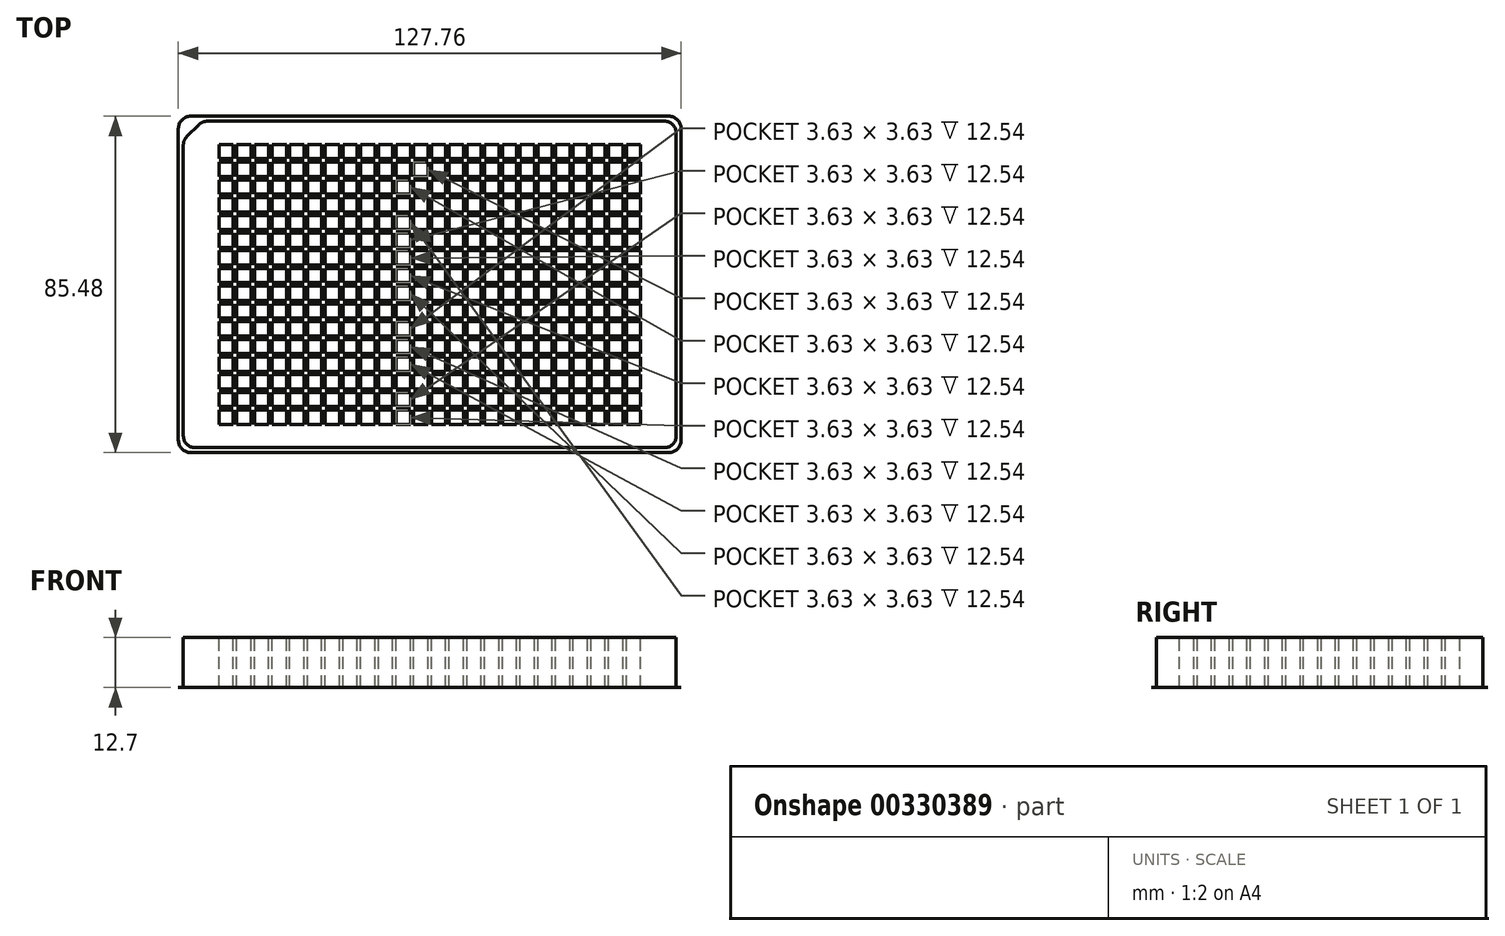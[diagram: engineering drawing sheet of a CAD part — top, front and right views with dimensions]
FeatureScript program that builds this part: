
annotation { "Feature Type Name" : "Feature", "Feature Type Description" : "" }
export const myFeature = defineFeature(function(context is Context, id is Id, definition is map)
    precondition{}
    {
        {
            var Q0;
            Q0=qCreatedBy(makeId("Top.planeOp"),FACE);
            var sketch = newSketch(context, id + "F0", { "sketchPlane" : qUnion([Q0])});
            skLineSegment(sketch, "E0.bottom", {"start": v(-60.7, 42.74) * mm, "end": v(60.7, 42.74) * mm});
            skLineSegment(sketch, "E0.top", {"start": v(-60.7, -42.74) * mm, "end": v(60.7, -42.74) * mm});
            skLineSegment(sketch, "E0.left", {"start": v(-63.88, 39.56) * mm, "end": v(-63.88, -39.56) * mm});
            skLineSegment(sketch, "E0.right", {"start": v(63.88, 39.56) * mm, "end": v(63.88, -39.56) * mm});
            skLineSegment(sketch, "E1", {"start": v(-63.88, 42.74) * mm, "end": v(63.88, -42.74) * mm, "construction": true});
            skPoint(sketch, "E2.visualSharp", {"position": v(-63.88, 42.74) * mm});
            skArc(sketch, "E2.filletArc", {"start": v(-60.7, 42.74) * mm, "mid": v(-62.95, 41.8) * mm, "end": v(-63.88, 39.56) * mm});
            skPoint(sketch, "E3.visualSharp", {"position": v(-63.88, -42.74) * mm});
            skArc(sketch, "E3.filletArc", {"start": v(-63.88, -39.56) * mm, "mid": v(-62.95, -41.8) * mm, "end": v(-60.7, -42.74) * mm});
            skPoint(sketch, "E4.visualSharp", {"position": v(63.88, 42.74) * mm});
            skArc(sketch, "E4.filletArc", {"start": v(63.88, 39.56) * mm, "mid": v(62.95, 41.8) * mm, "end": v(60.7, 42.74) * mm});
            skPoint(sketch, "E5.visualSharp", {"position": v(63.88, -42.74) * mm});
            skArc(sketch, "E5.filletArc", {"start": v(60.7, -42.74) * mm, "mid": v(62.95, -41.8) * mm, "end": v(63.88, -39.56) * mm});
            skSolve(sketch);
        }
        {
            var Q0;
            Q0=makeQuery(id+"F0.imprint","IMPRINT",FACE,{"disambiguationData":[TD([[makeQuery(id+"F0.imprint","IMPRINT",EDGE,{"derivedFrom":sQuery(id+"F0.wireOp",EDGE,"E0.bottom")}),-1.0]])]});
            extrude(context, id + "F1", {"entities" : qUnion([Q0]), "depth" : 3 / 812.8 * mm});
        }
        {
            var Q0;
            Q0=qCreatedBy(makeId("Top.planeOp"),FACE);
            var sketch = newSketch(context, id + "F2", { "sketchPlane" : qUnion([Q0])});
            skLineSegment(sketch, "E6.bottom", {"start": v(59.61, -41.47) * mm, "end": v(-59.6, -41.47) * mm});
            skLineSegment(sketch, "E6.top", {"start": v(59.61, 41.47) * mm, "end": v(-56.54, 41.47) * mm});
            skLineSegment(sketch, "E6.left", {"start": v(62.61, -38.47) * mm, "end": v(62.61, 38.47) * mm});
            skLineSegment(sketch, "E6.right", {"start": v(-62.6, -38.47) * mm, "end": v(-62.61, 35.4) * mm});
            skPoint(sketch, "E7.visualSharp", {"position": v(-62.61, -41.47) * mm});
            skArc(sketch, "E7.filletArc", {"start": v(-62.6, -38.47) * mm, "mid": v(-61.73, -40.6) * mm, "end": v(-59.6, -41.47) * mm});
            skPoint(sketch, "E8.visualSharp", {"position": v(62.6, -41.47) * mm});
            skArc(sketch, "E8.filletArc", {"start": v(59.61, -41.47) * mm, "mid": v(61.73, -40.6) * mm, "end": v(62.61, -38.47) * mm});
            skPoint(sketch, "E9.visualSharp", {"position": v(62.61, 41.47) * mm});
            skArc(sketch, "E9.filletArc", {"start": v(62.61, 38.47) * mm, "mid": v(61.73, 40.6) * mm, "end": v(59.61, 41.47) * mm});
            skLineSegment(sketch, "E10", {"start": v(-61.73, 37.52) * mm, "end": v(-58.66, 40.6) * mm});
            skPoint(sketch, "E11.orphan", {"position": v(-62.61, 41.47) * mm});
            skPoint(sketch, "E12.visualSharp", {"position": v(-62.61, 36.64) * mm});
            skArc(sketch, "E12.filletArc", {"start": v(-61.73, 37.52) * mm, "mid": v(-62.38, 36.55) * mm, "end": v(-62.61, 35.4) * mm});
            skPoint(sketch, "E13.visualSharp", {"position": v(-57.78, 41.47) * mm});
            skArc(sketch, "E13.filletArc", {"start": v(-56.54, 41.47) * mm, "mid": v(-57.69, 41.24) * mm, "end": v(-58.66, 40.6) * mm});
            skSolve(sketch);
        }
        {
            var Q0;
            Q0=qSketchRegion(id+"F2",true);
            extrude(context, id + "F3", {"entities" : qUnion([Q0]), "operationType" : NewBodyOperationType.ADD, "depth" : 12.7 * mm});
        }
        {
            var Q0;
            Q0=makeQuery(id+"F3.opExtrude","CAP_FACE",FACE,{"disambiguationData":[OSD([sQuery(id+"F2.wireOp",EDGE,"E6.bottom"),sQuery(id+"F2.wireOp",EDGE,"E6.top"),sQuery(id+"F2.wireOp",EDGE,"E6.left"),sQuery(id+"F2.wireOp",EDGE,"E6.right"),sQuery(id+"F2.wireOp",EDGE,"E7.filletArc"),sQuery(id+"F2.wireOp",EDGE,"E8.filletArc"),sQuery(id+"F2.wireOp",EDGE,"E9.filletArc"),sQuery(id+"F2.wireOp",EDGE,"E10"),sQuery(id+"F2.wireOp",EDGE,"E12.filletArc"),sQuery(id+"F2.wireOp",EDGE,"E13.filletArc")])],"isStart":false});
            var sketch = newSketch(context, id + "F4", { "sketchPlane" : qUnion([Q0])});
            skLineSegment(sketch, "E14.rect.bottom", {"start": v(-49.94, 31.93) * mm, "end": v(-53.57, 31.93) * mm});
            skLineSegment(sketch, "E14.rect.top", {"start": v(-49.94, 35.56) * mm, "end": v(-53.57, 35.56) * mm});
            skLineSegment(sketch, "E14.rect.left", {"start": v(-49.94, 31.93) * mm, "end": v(-49.94, 35.56) * mm});
            skLineSegment(sketch, "E14.rect.right", {"start": v(-53.57, 31.93) * mm, "end": v(-53.57, 35.56) * mm});
            skPoint(sketch, "E14.rect.middle", {"position": v(-51.75, 33.75) * mm});
            skLineSegment(sketch, "E15.1.0.0", {"start": v(-49.94, 27.43) * mm, "end": v(-49.94, 31.06) * mm});
            skLineSegment(sketch, "E15.1.0.1", {"start": v(-49.94, 27.43) * mm, "end": v(-53.57, 27.43) * mm});
            skLineSegment(sketch, "E15.1.0.2", {"start": v(-53.57, 27.43) * mm, "end": v(-53.57, 31.06) * mm});
            skLineSegment(sketch, "E15.1.0.3", {"start": v(-49.94, 31.06) * mm, "end": v(-53.57, 31.06) * mm});
            skLineSegment(sketch, "E15.2.0.0", {"start": v(-49.94, 22.93) * mm, "end": v(-49.94, 26.56) * mm});
            skLineSegment(sketch, "E15.2.0.1", {"start": v(-49.94, 22.93) * mm, "end": v(-53.57, 22.93) * mm});
            skLineSegment(sketch, "E15.2.0.2", {"start": v(-53.57, 22.93) * mm, "end": v(-53.57, 26.56) * mm});
            skLineSegment(sketch, "E15.2.0.3", {"start": v(-49.94, 26.56) * mm, "end": v(-53.57, 26.56) * mm});
            skLineSegment(sketch, "E15.direction1", {"start": v(-49.94, 31.93) * mm, "end": v(-49.94, 27.43) * mm, "construction": true});
            skLineSegment(sketch, "E16.0.3.0", {"start": v(-49.94, 18.43) * mm, "end": v(-49.94, 22.06) * mm});
            skLineSegment(sketch, "E16.3.3.0", {"start": v(-49.94, 18.43) * mm, "end": v(-53.57, 18.43) * mm});
            skLineSegment(sketch, "E16.6.3.0", {"start": v(-53.57, 18.43) * mm, "end": v(-53.57, 22.06) * mm});
            skLineSegment(sketch, "E16.9.3.0", {"start": v(-49.94, 22.06) * mm, "end": v(-53.57, 22.06) * mm});
            skLineSegment(sketch, "E16.0.4.0", {"start": v(-49.94, 13.93) * mm, "end": v(-49.94, 17.56) * mm});
            skLineSegment(sketch, "E16.3.4.0", {"start": v(-49.94, 13.93) * mm, "end": v(-53.57, 13.93) * mm});
            skLineSegment(sketch, "E16.6.4.0", {"start": v(-53.57, 13.93) * mm, "end": v(-53.57, 17.56) * mm});
            skLineSegment(sketch, "E16.9.4.0", {"start": v(-49.94, 17.56) * mm, "end": v(-53.57, 17.56) * mm});
            skLineSegment(sketch, "E16.0.5.0", {"start": v(-49.94, 9.43) * mm, "end": v(-49.94, 13.06) * mm});
            skLineSegment(sketch, "E16.3.5.0", {"start": v(-49.94, 9.43) * mm, "end": v(-53.57, 9.43) * mm});
            skLineSegment(sketch, "E16.6.5.0", {"start": v(-53.57, 9.43) * mm, "end": v(-53.57, 13.06) * mm});
            skLineSegment(sketch, "E16.9.5.0", {"start": v(-49.94, 13.06) * mm, "end": v(-53.57, 13.06) * mm});
            skLineSegment(sketch, "E16.0.6.0", {"start": v(-49.94, 4.93) * mm, "end": v(-49.94, 8.56) * mm});
            skLineSegment(sketch, "E16.3.6.0", {"start": v(-49.94, 4.93) * mm, "end": v(-53.57, 4.93) * mm});
            skLineSegment(sketch, "E16.6.6.0", {"start": v(-53.57, 4.93) * mm, "end": v(-53.57, 8.56) * mm});
            skLineSegment(sketch, "E16.9.6.0", {"start": v(-49.94, 8.56) * mm, "end": v(-53.57, 8.56) * mm});
            skLineSegment(sketch, "E16.0.7.0", {"start": v(-49.94, 0.43) * mm, "end": v(-49.94, 4.06) * mm});
            skLineSegment(sketch, "E16.3.7.0", {"start": v(-49.94, 0.43) * mm, "end": v(-53.57, 0.43) * mm});
            skLineSegment(sketch, "E16.6.7.0", {"start": v(-53.57, 0.43) * mm, "end": v(-53.57, 4.06) * mm});
            skLineSegment(sketch, "E16.9.7.0", {"start": v(-49.94, 4.06) * mm, "end": v(-53.57, 4.06) * mm});
            skLineSegment(sketch, "E16.0.8.0", {"start": v(-49.94, -4.07) * mm, "end": v(-49.94, -0.44) * mm});
            skLineSegment(sketch, "E16.3.8.0", {"start": v(-49.94, -4.07) * mm, "end": v(-53.57, -4.07) * mm});
            skLineSegment(sketch, "E16.6.8.0", {"start": v(-53.57, -4.07) * mm, "end": v(-53.57, -0.44) * mm});
            skLineSegment(sketch, "E16.9.8.0", {"start": v(-49.94, -0.44) * mm, "end": v(-53.57, -0.44) * mm});
            skLineSegment(sketch, "E16.0.9.0", {"start": v(-49.94, -8.57) * mm, "end": v(-49.94, -4.94) * mm});
            skLineSegment(sketch, "E16.3.9.0", {"start": v(-49.94, -8.57) * mm, "end": v(-53.57, -8.57) * mm});
            skLineSegment(sketch, "E16.6.9.0", {"start": v(-53.57, -8.57) * mm, "end": v(-53.57, -4.94) * mm});
            skLineSegment(sketch, "E16.9.9.0", {"start": v(-49.94, -4.94) * mm, "end": v(-53.57, -4.94) * mm});
            skLineSegment(sketch, "E16.0.10.0", {"start": v(-49.94, -13.07) * mm, "end": v(-49.94, -9.44) * mm});
            skLineSegment(sketch, "E16.3.10.0", {"start": v(-49.94, -13.07) * mm, "end": v(-53.57, -13.07) * mm});
            skLineSegment(sketch, "E16.6.10.0", {"start": v(-53.57, -13.07) * mm, "end": v(-53.57, -9.44) * mm});
            skLineSegment(sketch, "E16.9.10.0", {"start": v(-49.94, -9.44) * mm, "end": v(-53.57, -9.44) * mm});
            skLineSegment(sketch, "E16.0.11.0", {"start": v(-49.94, -17.57) * mm, "end": v(-49.94, -13.94) * mm});
            skLineSegment(sketch, "E16.3.11.0", {"start": v(-49.94, -17.57) * mm, "end": v(-53.57, -17.57) * mm});
            skLineSegment(sketch, "E16.6.11.0", {"start": v(-53.57, -17.57) * mm, "end": v(-53.57, -13.94) * mm});
            skLineSegment(sketch, "E16.9.11.0", {"start": v(-49.94, -13.94) * mm, "end": v(-53.57, -13.94) * mm});
            skLineSegment(sketch, "E16.0.12.0", {"start": v(-49.94, -22.07) * mm, "end": v(-49.94, -18.44) * mm});
            skLineSegment(sketch, "E16.3.12.0", {"start": v(-49.94, -22.07) * mm, "end": v(-53.57, -22.07) * mm});
            skLineSegment(sketch, "E16.6.12.0", {"start": v(-53.57, -22.07) * mm, "end": v(-53.57, -18.44) * mm});
            skLineSegment(sketch, "E16.9.12.0", {"start": v(-49.94, -18.44) * mm, "end": v(-53.57, -18.44) * mm});
            skLineSegment(sketch, "E16.0.13.0", {"start": v(-49.94, -26.57) * mm, "end": v(-49.94, -22.94) * mm});
            skLineSegment(sketch, "E16.3.13.0", {"start": v(-49.94, -26.57) * mm, "end": v(-53.57, -26.57) * mm});
            skLineSegment(sketch, "E16.6.13.0", {"start": v(-53.57, -26.57) * mm, "end": v(-53.57, -22.94) * mm});
            skLineSegment(sketch, "E16.9.13.0", {"start": v(-49.94, -22.94) * mm, "end": v(-53.57, -22.94) * mm});
            skLineSegment(sketch, "E16.0.14.0", {"start": v(-49.94, -31.07) * mm, "end": v(-49.94, -27.44) * mm});
            skLineSegment(sketch, "E16.3.14.0", {"start": v(-49.94, -31.07) * mm, "end": v(-53.57, -31.07) * mm});
            skLineSegment(sketch, "E16.6.14.0", {"start": v(-53.57, -31.07) * mm, "end": v(-53.57, -27.44) * mm});
            skLineSegment(sketch, "E16.9.14.0", {"start": v(-49.94, -27.44) * mm, "end": v(-53.57, -27.44) * mm});
            skLineSegment(sketch, "E16.0.15.0", {"start": v(-49.94, -35.57) * mm, "end": v(-49.94, -31.94) * mm});
            skLineSegment(sketch, "E16.3.15.0", {"start": v(-49.94, -35.57) * mm, "end": v(-53.57, -35.57) * mm});
            skLineSegment(sketch, "E16.6.15.0", {"start": v(-53.57, -35.57) * mm, "end": v(-53.57, -31.94) * mm});
            skLineSegment(sketch, "E16.9.15.0", {"start": v(-49.94, -31.94) * mm, "end": v(-53.57, -31.94) * mm});
            skLineSegment(sketch, "E17.1.0.0", {"start": v(-49.07, 27.43) * mm, "end": v(-49.07, 31.06) * mm});
            skLineSegment(sketch, "E17.1.0.1", {"start": v(-45.44, 27.43) * mm, "end": v(-45.44, 31.06) * mm});
            skLineSegment(sketch, "E17.1.0.2", {"start": v(-45.44, -13.07) * mm, "end": v(-45.44, -9.44) * mm});
            skLineSegment(sketch, "E17.1.0.3", {"start": v(-49.07, 9.43) * mm, "end": v(-49.07, 13.06) * mm});
            skLineSegment(sketch, "E17.1.0.4", {"start": v(-49.07, -13.07) * mm, "end": v(-49.07, -9.44) * mm});
            skLineSegment(sketch, "E17.1.0.5", {"start": v(-49.07, -31.07) * mm, "end": v(-49.07, -27.44) * mm});
            skPoint(sketch, "E17.1.0.6", {"position": v(-47.25, 33.75) * mm});
            skLineSegment(sketch, "E17.1.0.7", {"start": v(-45.44, 9.43) * mm, "end": v(-45.44, 13.06) * mm});
            skLineSegment(sketch, "E17.1.0.8", {"start": v(-45.44, -31.07) * mm, "end": v(-45.44, -27.44) * mm});
            skLineSegment(sketch, "E17.1.0.9", {"start": v(-45.44, 31.93) * mm, "end": v(-45.44, 27.43) * mm, "construction": true});
            skLineSegment(sketch, "E17.1.0.10", {"start": v(-45.44, 31.06) * mm, "end": v(-49.07, 31.06) * mm});
            skLineSegment(sketch, "E17.1.0.11", {"start": v(-45.44, 4.93) * mm, "end": v(-49.07, 4.93) * mm});
            skLineSegment(sketch, "E17.1.0.12", {"start": v(-45.44, -13.07) * mm, "end": v(-49.07, -13.07) * mm});
            skLineSegment(sketch, "E17.1.0.13", {"start": v(-45.44, -31.07) * mm, "end": v(-49.07, -31.07) * mm});
            skLineSegment(sketch, "E17.1.0.14", {"start": v(-49.07, 31.93) * mm, "end": v(-49.07, 35.56) * mm});
            skLineSegment(sketch, "E17.1.0.15", {"start": v(-45.44, 31.93) * mm, "end": v(-45.44, 35.56) * mm});
            skLineSegment(sketch, "E17.1.0.16", {"start": v(-45.44, 31.93) * mm, "end": v(-49.07, 31.93) * mm});
            skLineSegment(sketch, "E17.1.0.17", {"start": v(-49.07, 18.43) * mm, "end": v(-49.07, 22.06) * mm});
            skLineSegment(sketch, "E17.1.0.18", {"start": v(-45.44, 13.06) * mm, "end": v(-49.07, 13.06) * mm});
            skLineSegment(sketch, "E17.1.0.19", {"start": v(-45.44, -4.94) * mm, "end": v(-49.07, -4.94) * mm});
            skLineSegment(sketch, "E17.1.0.20", {"start": v(-45.44, -22.94) * mm, "end": v(-49.07, -22.94) * mm});
            skLineSegment(sketch, "E17.1.0.21", {"start": v(-45.44, -26.57) * mm, "end": v(-45.44, -22.94) * mm});
            skLineSegment(sketch, "E17.1.0.22", {"start": v(-49.07, -8.57) * mm, "end": v(-49.07, -4.94) * mm});
            skLineSegment(sketch, "E17.1.0.23", {"start": v(-49.07, -26.57) * mm, "end": v(-49.07, -22.94) * mm});
            skLineSegment(sketch, "E17.1.0.24", {"start": v(-45.44, 17.56) * mm, "end": v(-49.07, 17.56) * mm});
            skLineSegment(sketch, "E17.1.0.25", {"start": v(-45.44, -0.44) * mm, "end": v(-49.07, -0.44) * mm});
            skLineSegment(sketch, "E17.1.0.26", {"start": v(-45.44, -9.44) * mm, "end": v(-49.07, -9.44) * mm});
            skLineSegment(sketch, "E17.1.0.27", {"start": v(-49.07, -22.07) * mm, "end": v(-49.07, -18.44) * mm});
            skLineSegment(sketch, "E17.1.0.28", {"start": v(-49.07, 13.93) * mm, "end": v(-49.07, 17.56) * mm});
            skLineSegment(sketch, "E17.1.0.29", {"start": v(-49.07, -4.07) * mm, "end": v(-49.07, -0.44) * mm});
            skLineSegment(sketch, "E17.1.0.30", {"start": v(-45.44, 13.93) * mm, "end": v(-49.07, 13.93) * mm});
            skLineSegment(sketch, "E17.1.0.31", {"start": v(-45.44, -4.07) * mm, "end": v(-49.07, -4.07) * mm});
            skLineSegment(sketch, "E17.1.0.32", {"start": v(-45.44, -17.57) * mm, "end": v(-49.07, -17.57) * mm});
            skLineSegment(sketch, "E17.1.0.33", {"start": v(-45.44, -27.44) * mm, "end": v(-49.07, -27.44) * mm});
            skLineSegment(sketch, "E17.1.0.34", {"start": v(-45.44, -35.57) * mm, "end": v(-49.07, -35.57) * mm});
            skLineSegment(sketch, "E17.1.0.35", {"start": v(-45.44, 0.43) * mm, "end": v(-49.07, 0.43) * mm});
            skLineSegment(sketch, "E17.1.0.36", {"start": v(-45.44, 13.93) * mm, "end": v(-45.44, 17.56) * mm});
            skLineSegment(sketch, "E17.1.0.37", {"start": v(-45.44, -22.07) * mm, "end": v(-45.44, -18.44) * mm});
            skLineSegment(sketch, "E17.1.0.38", {"start": v(-45.44, -17.57) * mm, "end": v(-45.44, -13.94) * mm});
            skLineSegment(sketch, "E17.1.0.39", {"start": v(-49.07, 4.93) * mm, "end": v(-49.07, 8.56) * mm});
            skLineSegment(sketch, "E17.1.0.40", {"start": v(-45.44, 26.56) * mm, "end": v(-49.07, 26.56) * mm});
            skLineSegment(sketch, "E17.1.0.41", {"start": v(-45.44, 9.43) * mm, "end": v(-49.07, 9.43) * mm});
            skLineSegment(sketch, "E17.1.0.42", {"start": v(-49.07, 22.93) * mm, "end": v(-49.07, 26.56) * mm});
            skLineSegment(sketch, "E17.1.0.43", {"start": v(-45.44, -13.94) * mm, "end": v(-49.07, -13.94) * mm});
            skLineSegment(sketch, "E17.1.0.44", {"start": v(-45.44, -31.94) * mm, "end": v(-49.07, -31.94) * mm});
            skLineSegment(sketch, "E17.1.0.45", {"start": v(-45.44, 22.06) * mm, "end": v(-49.07, 22.06) * mm});
            skLineSegment(sketch, "E17.1.0.46", {"start": v(-45.44, 4.06) * mm, "end": v(-49.07, 4.06) * mm});
            skLineSegment(sketch, "E17.1.0.47", {"start": v(-49.07, 0.43) * mm, "end": v(-49.07, 4.06) * mm});
            skLineSegment(sketch, "E17.1.0.48", {"start": v(-49.07, -35.57) * mm, "end": v(-49.07, -31.94) * mm});
            skLineSegment(sketch, "E17.1.0.49", {"start": v(-45.44, 0.43) * mm, "end": v(-45.44, 4.06) * mm});
            skLineSegment(sketch, "E17.1.0.50", {"start": v(-45.44, -26.57) * mm, "end": v(-49.07, -26.57) * mm});
            skLineSegment(sketch, "E17.1.0.51", {"start": v(-45.44, -35.57) * mm, "end": v(-45.44, -31.94) * mm});
            skLineSegment(sketch, "E17.1.0.52", {"start": v(-45.44, -4.07) * mm, "end": v(-45.44, -0.44) * mm});
            skLineSegment(sketch, "E17.1.0.53", {"start": v(-45.44, -22.07) * mm, "end": v(-49.07, -22.07) * mm});
            skLineSegment(sketch, "E17.1.0.54", {"start": v(-45.44, 18.43) * mm, "end": v(-45.44, 22.06) * mm});
            skLineSegment(sketch, "E17.1.0.55", {"start": v(-45.44, -18.44) * mm, "end": v(-49.07, -18.44) * mm});
            skLineSegment(sketch, "E17.1.0.56", {"start": v(-45.44, -8.57) * mm, "end": v(-45.44, -4.94) * mm});
            skLineSegment(sketch, "E17.1.0.57", {"start": v(-45.44, 18.43) * mm, "end": v(-49.07, 18.43) * mm});
            skLineSegment(sketch, "E17.1.0.58", {"start": v(-45.44, 35.56) * mm, "end": v(-49.07, 35.56) * mm});
            skLineSegment(sketch, "E17.1.0.59", {"start": v(-45.44, 4.93) * mm, "end": v(-45.44, 8.56) * mm});
            skLineSegment(sketch, "E17.1.0.60", {"start": v(-45.44, 27.43) * mm, "end": v(-49.07, 27.43) * mm});
            skLineSegment(sketch, "E17.1.0.61", {"start": v(-45.44, -8.57) * mm, "end": v(-49.07, -8.57) * mm});
            skLineSegment(sketch, "E17.1.0.62", {"start": v(-45.44, 8.56) * mm, "end": v(-49.07, 8.56) * mm});
            skLineSegment(sketch, "E17.1.0.63", {"start": v(-49.07, -17.57) * mm, "end": v(-49.07, -13.94) * mm});
            skLineSegment(sketch, "E17.1.0.64", {"start": v(-45.44, 22.93) * mm, "end": v(-49.07, 22.93) * mm});
            skLineSegment(sketch, "E17.1.0.65", {"start": v(-45.44, 22.93) * mm, "end": v(-45.44, 26.56) * mm});
            skLineSegment(sketch, "E17.2.0.0", {"start": v(-44.57, 27.43) * mm, "end": v(-44.57, 31.06) * mm});
            skLineSegment(sketch, "E17.2.0.1", {"start": v(-40.94, 27.43) * mm, "end": v(-40.94, 31.06) * mm});
            skLineSegment(sketch, "E17.2.0.2", {"start": v(-40.94, -13.07) * mm, "end": v(-40.94, -9.44) * mm});
            skLineSegment(sketch, "E17.2.0.3", {"start": v(-44.57, 9.43) * mm, "end": v(-44.57, 13.06) * mm});
            skLineSegment(sketch, "E17.2.0.4", {"start": v(-44.56, -13.07) * mm, "end": v(-44.56, -9.44) * mm});
            skLineSegment(sketch, "E17.2.0.5", {"start": v(-44.56, -31.07) * mm, "end": v(-44.56, -27.44) * mm});
            skPoint(sketch, "E17.2.0.6", {"position": v(-42.75, 33.75) * mm});
            skLineSegment(sketch, "E17.2.0.7", {"start": v(-40.94, 9.43) * mm, "end": v(-40.94, 13.06) * mm});
            skLineSegment(sketch, "E17.2.0.8", {"start": v(-40.94, -31.07) * mm, "end": v(-40.94, -27.44) * mm});
            skLineSegment(sketch, "E17.2.0.9", {"start": v(-40.94, 31.93) * mm, "end": v(-40.94, 27.43) * mm, "construction": true});
            skLineSegment(sketch, "E17.2.0.10", {"start": v(-40.94, 31.06) * mm, "end": v(-44.57, 31.06) * mm});
            skLineSegment(sketch, "E17.2.0.11", {"start": v(-40.94, 4.93) * mm, "end": v(-44.57, 4.93) * mm});
            skLineSegment(sketch, "E17.2.0.12", {"start": v(-40.94, -13.07) * mm, "end": v(-44.57, -13.07) * mm});
            skLineSegment(sketch, "E17.2.0.13", {"start": v(-40.94, -31.07) * mm, "end": v(-44.57, -31.07) * mm});
            skLineSegment(sketch, "E17.2.0.14", {"start": v(-44.57, 31.93) * mm, "end": v(-44.57, 35.56) * mm});
            skLineSegment(sketch, "E17.2.0.15", {"start": v(-40.94, 31.93) * mm, "end": v(-40.94, 35.56) * mm});
            skLineSegment(sketch, "E17.2.0.16", {"start": v(-40.94, 31.93) * mm, "end": v(-44.57, 31.93) * mm});
            skLineSegment(sketch, "E17.2.0.17", {"start": v(-44.57, 18.43) * mm, "end": v(-44.57, 22.06) * mm});
            skLineSegment(sketch, "E17.2.0.18", {"start": v(-40.94, 13.06) * mm, "end": v(-44.57, 13.06) * mm});
            skLineSegment(sketch, "E17.2.0.19", {"start": v(-40.94, -4.94) * mm, "end": v(-44.57, -4.94) * mm});
            skLineSegment(sketch, "E17.2.0.20", {"start": v(-40.94, -22.94) * mm, "end": v(-44.57, -22.94) * mm});
            skLineSegment(sketch, "E17.2.0.21", {"start": v(-40.94, -26.57) * mm, "end": v(-40.94, -22.94) * mm});
            skLineSegment(sketch, "E17.2.0.22", {"start": v(-44.56, -8.57) * mm, "end": v(-44.56, -4.94) * mm});
            skLineSegment(sketch, "E17.2.0.23", {"start": v(-44.56, -26.57) * mm, "end": v(-44.56, -22.94) * mm});
            skLineSegment(sketch, "E17.2.0.24", {"start": v(-40.94, 17.56) * mm, "end": v(-44.57, 17.56) * mm});
            skLineSegment(sketch, "E17.2.0.25", {"start": v(-40.94, -0.44) * mm, "end": v(-44.57, -0.44) * mm});
            skLineSegment(sketch, "E17.2.0.26", {"start": v(-40.94, -9.44) * mm, "end": v(-44.57, -9.44) * mm});
            skLineSegment(sketch, "E17.2.0.27", {"start": v(-44.56, -22.07) * mm, "end": v(-44.56, -18.44) * mm});
            skLineSegment(sketch, "E17.2.0.28", {"start": v(-44.57, 13.93) * mm, "end": v(-44.57, 17.56) * mm});
            skLineSegment(sketch, "E17.2.0.29", {"start": v(-44.56, -4.07) * mm, "end": v(-44.56, -0.44) * mm});
            skLineSegment(sketch, "E17.2.0.30", {"start": v(-40.94, 13.93) * mm, "end": v(-44.57, 13.93) * mm});
            skLineSegment(sketch, "E17.2.0.31", {"start": v(-40.94, -4.07) * mm, "end": v(-44.57, -4.07) * mm});
            skLineSegment(sketch, "E17.2.0.32", {"start": v(-40.94, -17.57) * mm, "end": v(-44.57, -17.57) * mm});
            skLineSegment(sketch, "E17.2.0.33", {"start": v(-40.94, -27.44) * mm, "end": v(-44.57, -27.44) * mm});
            skLineSegment(sketch, "E17.2.0.34", {"start": v(-40.94, -35.57) * mm, "end": v(-44.57, -35.57) * mm});
            skLineSegment(sketch, "E17.2.0.35", {"start": v(-40.94, 0.43) * mm, "end": v(-44.57, 0.43) * mm});
            skLineSegment(sketch, "E17.2.0.36", {"start": v(-40.94, 13.93) * mm, "end": v(-40.94, 17.56) * mm});
            skLineSegment(sketch, "E17.2.0.37", {"start": v(-40.94, -22.07) * mm, "end": v(-40.94, -18.44) * mm});
            skLineSegment(sketch, "E17.2.0.38", {"start": v(-40.94, -17.57) * mm, "end": v(-40.94, -13.94) * mm});
            skLineSegment(sketch, "E17.2.0.39", {"start": v(-44.57, 4.93) * mm, "end": v(-44.57, 8.56) * mm});
            skLineSegment(sketch, "E17.2.0.40", {"start": v(-40.94, 26.56) * mm, "end": v(-44.57, 26.56) * mm});
            skLineSegment(sketch, "E17.2.0.41", {"start": v(-40.94, 9.43) * mm, "end": v(-44.57, 9.43) * mm});
            skLineSegment(sketch, "E17.2.0.42", {"start": v(-44.57, 22.93) * mm, "end": v(-44.57, 26.56) * mm});
            skLineSegment(sketch, "E17.2.0.43", {"start": v(-40.94, -13.94) * mm, "end": v(-44.57, -13.94) * mm});
            skLineSegment(sketch, "E17.2.0.44", {"start": v(-40.94, -31.94) * mm, "end": v(-44.57, -31.94) * mm});
            skLineSegment(sketch, "E17.2.0.45", {"start": v(-40.94, 22.06) * mm, "end": v(-44.57, 22.06) * mm});
            skLineSegment(sketch, "E17.2.0.46", {"start": v(-40.94, 4.06) * mm, "end": v(-44.57, 4.06) * mm});
            skLineSegment(sketch, "E17.2.0.47", {"start": v(-44.56, 0.43) * mm, "end": v(-44.56, 4.06) * mm});
            skLineSegment(sketch, "E17.2.0.48", {"start": v(-44.56, -35.57) * mm, "end": v(-44.56, -31.94) * mm});
            skLineSegment(sketch, "E17.2.0.49", {"start": v(-40.94, 0.43) * mm, "end": v(-40.94, 4.06) * mm});
            skLineSegment(sketch, "E17.2.0.50", {"start": v(-40.94, -26.57) * mm, "end": v(-44.57, -26.57) * mm});
            skLineSegment(sketch, "E17.2.0.51", {"start": v(-40.94, -35.57) * mm, "end": v(-40.94, -31.94) * mm});
            skLineSegment(sketch, "E17.2.0.52", {"start": v(-40.94, -4.07) * mm, "end": v(-40.94, -0.44) * mm});
            skLineSegment(sketch, "E17.2.0.53", {"start": v(-40.94, -22.07) * mm, "end": v(-44.57, -22.07) * mm});
            skLineSegment(sketch, "E17.2.0.54", {"start": v(-40.94, 18.43) * mm, "end": v(-40.94, 22.06) * mm});
            skLineSegment(sketch, "E17.2.0.55", {"start": v(-40.94, -18.44) * mm, "end": v(-44.57, -18.44) * mm});
            skLineSegment(sketch, "E17.2.0.56", {"start": v(-40.94, -8.57) * mm, "end": v(-40.94, -4.94) * mm});
            skLineSegment(sketch, "E17.2.0.57", {"start": v(-40.94, 18.43) * mm, "end": v(-44.57, 18.43) * mm});
            skLineSegment(sketch, "E17.2.0.58", {"start": v(-40.94, 35.56) * mm, "end": v(-44.57, 35.56) * mm});
            skLineSegment(sketch, "E17.2.0.59", {"start": v(-40.94, 4.93) * mm, "end": v(-40.94, 8.56) * mm});
            skLineSegment(sketch, "E17.2.0.60", {"start": v(-40.94, 27.43) * mm, "end": v(-44.57, 27.43) * mm});
            skLineSegment(sketch, "E17.2.0.61", {"start": v(-40.94, -8.57) * mm, "end": v(-44.57, -8.57) * mm});
            skLineSegment(sketch, "E17.2.0.62", {"start": v(-40.94, 8.56) * mm, "end": v(-44.57, 8.56) * mm});
            skLineSegment(sketch, "E17.2.0.63", {"start": v(-44.56, -17.57) * mm, "end": v(-44.56, -13.94) * mm});
            skLineSegment(sketch, "E17.2.0.64", {"start": v(-40.94, 22.93) * mm, "end": v(-44.57, 22.93) * mm});
            skLineSegment(sketch, "E17.2.0.65", {"start": v(-40.94, 22.93) * mm, "end": v(-40.94, 26.56) * mm});
            skLineSegment(sketch, "E17.3.0.0", {"start": v(-40.07, 27.43) * mm, "end": v(-40.07, 31.06) * mm});
            skLineSegment(sketch, "E17.3.0.1", {"start": v(-36.43, 27.43) * mm, "end": v(-36.43, 31.06) * mm});
            skLineSegment(sketch, "E17.3.0.2", {"start": v(-36.43, -13.07) * mm, "end": v(-36.43, -9.44) * mm});
            skLineSegment(sketch, "E17.3.0.3", {"start": v(-40.07, 9.43) * mm, "end": v(-40.07, 13.06) * mm});
            skLineSegment(sketch, "E17.3.0.4", {"start": v(-40.06, -13.07) * mm, "end": v(-40.06, -9.44) * mm});
            skLineSegment(sketch, "E17.3.0.5", {"start": v(-40.06, -31.07) * mm, "end": v(-40.06, -27.44) * mm});
            skPoint(sketch, "E17.3.0.6", {"position": v(-38.25, 33.75) * mm});
            skLineSegment(sketch, "E17.3.0.7", {"start": v(-36.44, 9.43) * mm, "end": v(-36.44, 13.06) * mm});
            skLineSegment(sketch, "E17.3.0.8", {"start": v(-36.43, -31.07) * mm, "end": v(-36.43, -27.44) * mm});
            skLineSegment(sketch, "E17.3.0.9", {"start": v(-36.44, 31.93) * mm, "end": v(-36.44, 27.43) * mm, "construction": true});
            skLineSegment(sketch, "E17.3.0.10", {"start": v(-36.44, 31.06) * mm, "end": v(-40.07, 31.06) * mm});
            skLineSegment(sketch, "E17.3.0.11", {"start": v(-36.44, 4.93) * mm, "end": v(-40.07, 4.93) * mm});
            skLineSegment(sketch, "E17.3.0.12", {"start": v(-36.44, -13.07) * mm, "end": v(-40.07, -13.07) * mm});
            skLineSegment(sketch, "E17.3.0.13", {"start": v(-36.44, -31.07) * mm, "end": v(-40.07, -31.07) * mm});
            skLineSegment(sketch, "E17.3.0.14", {"start": v(-40.07, 31.93) * mm, "end": v(-40.07, 35.56) * mm});
            skLineSegment(sketch, "E17.3.0.15", {"start": v(-36.44, 31.93) * mm, "end": v(-36.44, 35.56) * mm});
            skLineSegment(sketch, "E17.3.0.16", {"start": v(-36.44, 31.93) * mm, "end": v(-40.07, 31.93) * mm});
            skLineSegment(sketch, "E17.3.0.17", {"start": v(-40.07, 18.43) * mm, "end": v(-40.07, 22.06) * mm});
            skLineSegment(sketch, "E17.3.0.18", {"start": v(-36.44, 13.06) * mm, "end": v(-40.07, 13.06) * mm});
            skLineSegment(sketch, "E17.3.0.19", {"start": v(-36.44, -4.94) * mm, "end": v(-40.07, -4.94) * mm});
            skLineSegment(sketch, "E17.3.0.20", {"start": v(-36.44, -22.94) * mm, "end": v(-40.07, -22.94) * mm});
            skLineSegment(sketch, "E17.3.0.21", {"start": v(-36.43, -26.57) * mm, "end": v(-36.43, -22.94) * mm});
            skLineSegment(sketch, "E17.3.0.22", {"start": v(-40.06, -8.57) * mm, "end": v(-40.06, -4.94) * mm});
            skLineSegment(sketch, "E17.3.0.23", {"start": v(-40.06, -26.57) * mm, "end": v(-40.06, -22.94) * mm});
            skLineSegment(sketch, "E17.3.0.24", {"start": v(-36.44, 17.56) * mm, "end": v(-40.07, 17.56) * mm});
            skLineSegment(sketch, "E17.3.0.25", {"start": v(-36.44, -0.44) * mm, "end": v(-40.07, -0.44) * mm});
            skLineSegment(sketch, "E17.3.0.26", {"start": v(-36.44, -9.44) * mm, "end": v(-40.07, -9.44) * mm});
            skLineSegment(sketch, "E17.3.0.27", {"start": v(-40.06, -22.07) * mm, "end": v(-40.06, -18.44) * mm});
            skLineSegment(sketch, "E17.3.0.28", {"start": v(-40.07, 13.93) * mm, "end": v(-40.07, 17.56) * mm});
            skLineSegment(sketch, "E17.3.0.29", {"start": v(-40.06, -4.07) * mm, "end": v(-40.06, -0.44) * mm});
            skLineSegment(sketch, "E17.3.0.30", {"start": v(-36.44, 13.93) * mm, "end": v(-40.07, 13.93) * mm});
            skLineSegment(sketch, "E17.3.0.31", {"start": v(-36.44, -4.07) * mm, "end": v(-40.07, -4.07) * mm});
            skLineSegment(sketch, "E17.3.0.32", {"start": v(-36.44, -17.57) * mm, "end": v(-40.07, -17.57) * mm});
            skLineSegment(sketch, "E17.3.0.33", {"start": v(-36.44, -27.44) * mm, "end": v(-40.07, -27.44) * mm});
            skLineSegment(sketch, "E17.3.0.34", {"start": v(-36.44, -35.57) * mm, "end": v(-40.07, -35.57) * mm});
            skLineSegment(sketch, "E17.3.0.35", {"start": v(-36.44, 0.43) * mm, "end": v(-40.07, 0.43) * mm});
            skLineSegment(sketch, "E17.3.0.36", {"start": v(-36.44, 13.93) * mm, "end": v(-36.44, 17.56) * mm});
            skLineSegment(sketch, "E17.3.0.37", {"start": v(-36.43, -22.07) * mm, "end": v(-36.43, -18.44) * mm});
            skLineSegment(sketch, "E17.3.0.38", {"start": v(-36.43, -17.57) * mm, "end": v(-36.43, -13.94) * mm});
            skLineSegment(sketch, "E17.3.0.39", {"start": v(-40.07, 4.93) * mm, "end": v(-40.07, 8.56) * mm});
            skLineSegment(sketch, "E17.3.0.40", {"start": v(-36.44, 26.56) * mm, "end": v(-40.07, 26.56) * mm});
            skLineSegment(sketch, "E17.3.0.41", {"start": v(-36.44, 9.43) * mm, "end": v(-40.07, 9.43) * mm});
            skLineSegment(sketch, "E17.3.0.42", {"start": v(-40.07, 22.93) * mm, "end": v(-40.07, 26.56) * mm});
            skLineSegment(sketch, "E17.3.0.43", {"start": v(-36.44, -13.94) * mm, "end": v(-40.07, -13.94) * mm});
            skLineSegment(sketch, "E17.3.0.44", {"start": v(-36.44, -31.94) * mm, "end": v(-40.07, -31.94) * mm});
            skLineSegment(sketch, "E17.3.0.45", {"start": v(-36.44, 22.06) * mm, "end": v(-40.07, 22.06) * mm});
            skLineSegment(sketch, "E17.3.0.46", {"start": v(-36.44, 4.06) * mm, "end": v(-40.07, 4.06) * mm});
            skLineSegment(sketch, "E17.3.0.47", {"start": v(-40.06, 0.43) * mm, "end": v(-40.06, 4.06) * mm});
            skLineSegment(sketch, "E17.3.0.48", {"start": v(-40.06, -35.57) * mm, "end": v(-40.06, -31.94) * mm});
            skLineSegment(sketch, "E17.3.0.49", {"start": v(-36.43, 0.43) * mm, "end": v(-36.43, 4.06) * mm});
            skLineSegment(sketch, "E17.3.0.50", {"start": v(-36.44, -26.57) * mm, "end": v(-40.07, -26.57) * mm});
            skLineSegment(sketch, "E17.3.0.51", {"start": v(-36.43, -35.57) * mm, "end": v(-36.43, -31.94) * mm});
            skLineSegment(sketch, "E17.3.0.52", {"start": v(-36.43, -4.07) * mm, "end": v(-36.43, -0.44) * mm});
            skLineSegment(sketch, "E17.3.0.53", {"start": v(-36.44, -22.07) * mm, "end": v(-40.07, -22.07) * mm});
            skLineSegment(sketch, "E17.3.0.54", {"start": v(-36.44, 18.43) * mm, "end": v(-36.44, 22.06) * mm});
            skLineSegment(sketch, "E17.3.0.55", {"start": v(-36.44, -18.44) * mm, "end": v(-40.07, -18.44) * mm});
            skLineSegment(sketch, "E17.3.0.56", {"start": v(-36.43, -8.57) * mm, "end": v(-36.43, -4.94) * mm});
            skLineSegment(sketch, "E17.3.0.57", {"start": v(-36.44, 18.43) * mm, "end": v(-40.07, 18.43) * mm});
            skLineSegment(sketch, "E17.3.0.58", {"start": v(-36.44, 35.56) * mm, "end": v(-40.07, 35.56) * mm});
            skLineSegment(sketch, "E17.3.0.59", {"start": v(-36.44, 4.93) * mm, "end": v(-36.44, 8.56) * mm});
            skLineSegment(sketch, "E17.3.0.60", {"start": v(-36.44, 27.43) * mm, "end": v(-40.07, 27.43) * mm});
            skLineSegment(sketch, "E17.3.0.61", {"start": v(-36.44, -8.57) * mm, "end": v(-40.07, -8.57) * mm});
            skLineSegment(sketch, "E17.3.0.62", {"start": v(-36.44, 8.56) * mm, "end": v(-40.07, 8.56) * mm});
            skLineSegment(sketch, "E17.3.0.63", {"start": v(-40.06, -17.57) * mm, "end": v(-40.06, -13.94) * mm});
            skLineSegment(sketch, "E17.3.0.64", {"start": v(-36.44, 22.93) * mm, "end": v(-40.07, 22.93) * mm});
            skLineSegment(sketch, "E17.3.0.65", {"start": v(-36.44, 22.93) * mm, "end": v(-36.44, 26.56) * mm});
            skLineSegment(sketch, "E17.4.0.0", {"start": v(-35.56, 27.43) * mm, "end": v(-35.56, 31.06) * mm});
            skLineSegment(sketch, "E17.4.0.1", {"start": v(-31.93, 27.43) * mm, "end": v(-31.93, 31.06) * mm});
            skLineSegment(sketch, "E17.4.0.2", {"start": v(-31.93, -13.07) * mm, "end": v(-31.93, -9.44) * mm});
            skLineSegment(sketch, "E17.4.0.3", {"start": v(-35.56, 9.43) * mm, "end": v(-35.56, 13.06) * mm});
            skLineSegment(sketch, "E17.4.0.4", {"start": v(-35.56, -13.07) * mm, "end": v(-35.56, -9.44) * mm});
            skLineSegment(sketch, "E17.4.0.5", {"start": v(-35.56, -31.07) * mm, "end": v(-35.56, -27.44) * mm});
            skPoint(sketch, "E17.4.0.6", {"position": v(-33.75, 33.75) * mm});
            skLineSegment(sketch, "E17.4.0.7", {"start": v(-31.93, 9.43) * mm, "end": v(-31.93, 13.06) * mm});
            skLineSegment(sketch, "E17.4.0.8", {"start": v(-31.93, -31.07) * mm, "end": v(-31.93, -27.44) * mm});
            skLineSegment(sketch, "E17.4.0.9", {"start": v(-31.93, 31.93) * mm, "end": v(-31.93, 27.43) * mm, "construction": true});
            skLineSegment(sketch, "E17.4.0.10", {"start": v(-31.93, 31.06) * mm, "end": v(-35.56, 31.06) * mm});
            skLineSegment(sketch, "E17.4.0.11", {"start": v(-31.94, 4.93) * mm, "end": v(-35.57, 4.93) * mm});
            skLineSegment(sketch, "E17.4.0.12", {"start": v(-31.93, -13.07) * mm, "end": v(-35.56, -13.07) * mm});
            skLineSegment(sketch, "E17.4.0.13", {"start": v(-31.93, -31.07) * mm, "end": v(-35.56, -31.07) * mm});
            skLineSegment(sketch, "E17.4.0.14", {"start": v(-35.56, 31.93) * mm, "end": v(-35.56, 35.56) * mm});
            skLineSegment(sketch, "E17.4.0.15", {"start": v(-31.93, 31.93) * mm, "end": v(-31.93, 35.56) * mm});
            skLineSegment(sketch, "E17.4.0.16", {"start": v(-31.94, 31.93) * mm, "end": v(-35.57, 31.93) * mm});
            skLineSegment(sketch, "E17.4.0.17", {"start": v(-35.56, 18.43) * mm, "end": v(-35.56, 22.06) * mm});
            skLineSegment(sketch, "E17.4.0.18", {"start": v(-31.94, 13.06) * mm, "end": v(-35.57, 13.06) * mm});
            skLineSegment(sketch, "E17.4.0.19", {"start": v(-31.93, -4.94) * mm, "end": v(-35.56, -4.94) * mm});
            skLineSegment(sketch, "E17.4.0.20", {"start": v(-31.93, -22.94) * mm, "end": v(-35.56, -22.94) * mm});
            skLineSegment(sketch, "E17.4.0.21", {"start": v(-31.93, -26.57) * mm, "end": v(-31.93, -22.94) * mm});
            skLineSegment(sketch, "E17.4.0.22", {"start": v(-35.56, -8.57) * mm, "end": v(-35.56, -4.94) * mm});
            skLineSegment(sketch, "E17.4.0.23", {"start": v(-35.56, -26.57) * mm, "end": v(-35.56, -22.94) * mm});
            skLineSegment(sketch, "E17.4.0.24", {"start": v(-31.94, 17.56) * mm, "end": v(-35.57, 17.56) * mm});
            skLineSegment(sketch, "E17.4.0.25", {"start": v(-31.93, -0.44) * mm, "end": v(-35.56, -0.44) * mm});
            skLineSegment(sketch, "E17.4.0.26", {"start": v(-31.93, -9.44) * mm, "end": v(-35.56, -9.44) * mm});
            skLineSegment(sketch, "E17.4.0.27", {"start": v(-35.56, -22.07) * mm, "end": v(-35.56, -18.44) * mm});
            skLineSegment(sketch, "E17.4.0.28", {"start": v(-35.56, 13.93) * mm, "end": v(-35.56, 17.56) * mm});
            skLineSegment(sketch, "E17.4.0.29", {"start": v(-35.56, -4.07) * mm, "end": v(-35.56, -0.44) * mm});
            skLineSegment(sketch, "E17.4.0.30", {"start": v(-31.94, 13.93) * mm, "end": v(-35.57, 13.93) * mm});
            skLineSegment(sketch, "E17.4.0.31", {"start": v(-31.93, -4.07) * mm, "end": v(-35.56, -4.07) * mm});
            skLineSegment(sketch, "E17.4.0.32", {"start": v(-31.93, -17.57) * mm, "end": v(-35.56, -17.57) * mm});
            skLineSegment(sketch, "E17.4.0.33", {"start": v(-31.93, -27.44) * mm, "end": v(-35.56, -27.44) * mm});
            skLineSegment(sketch, "E17.4.0.34", {"start": v(-31.93, -35.57) * mm, "end": v(-35.56, -35.57) * mm});
            skLineSegment(sketch, "E17.4.0.35", {"start": v(-31.93, 0.43) * mm, "end": v(-35.56, 0.43) * mm});
            skLineSegment(sketch, "E17.4.0.36", {"start": v(-31.93, 13.93) * mm, "end": v(-31.93, 17.56) * mm});
            skLineSegment(sketch, "E17.4.0.37", {"start": v(-31.93, -22.07) * mm, "end": v(-31.93, -18.44) * mm});
            skLineSegment(sketch, "E17.4.0.38", {"start": v(-31.93, -17.57) * mm, "end": v(-31.93, -13.94) * mm});
            skLineSegment(sketch, "E17.4.0.39", {"start": v(-35.56, 4.93) * mm, "end": v(-35.56, 8.56) * mm});
            skLineSegment(sketch, "E17.4.0.40", {"start": v(-31.93, 26.56) * mm, "end": v(-35.56, 26.56) * mm});
            skLineSegment(sketch, "E17.4.0.41", {"start": v(-31.94, 9.43) * mm, "end": v(-35.57, 9.43) * mm});
            skLineSegment(sketch, "E17.4.0.42", {"start": v(-35.56, 22.93) * mm, "end": v(-35.56, 26.56) * mm});
            skLineSegment(sketch, "E17.4.0.43", {"start": v(-31.93, -13.94) * mm, "end": v(-35.56, -13.94) * mm});
            skLineSegment(sketch, "E17.4.0.44", {"start": v(-31.93, -31.94) * mm, "end": v(-35.56, -31.94) * mm});
            skLineSegment(sketch, "E17.4.0.45", {"start": v(-31.94, 22.06) * mm, "end": v(-35.57, 22.06) * mm});
            skLineSegment(sketch, "E17.4.0.46", {"start": v(-31.93, 4.06) * mm, "end": v(-35.56, 4.06) * mm});
            skLineSegment(sketch, "E17.4.0.47", {"start": v(-35.56, 0.43) * mm, "end": v(-35.56, 4.06) * mm});
            skLineSegment(sketch, "E17.4.0.48", {"start": v(-35.56, -35.57) * mm, "end": v(-35.56, -31.94) * mm});
            skLineSegment(sketch, "E17.4.0.49", {"start": v(-31.93, 0.43) * mm, "end": v(-31.93, 4.06) * mm});
            skLineSegment(sketch, "E17.4.0.50", {"start": v(-31.93, -26.57) * mm, "end": v(-35.56, -26.57) * mm});
            skLineSegment(sketch, "E17.4.0.51", {"start": v(-31.93, -35.57) * mm, "end": v(-31.93, -31.94) * mm});
            skLineSegment(sketch, "E17.4.0.52", {"start": v(-31.93, -4.07) * mm, "end": v(-31.93, -0.44) * mm});
            skLineSegment(sketch, "E17.4.0.53", {"start": v(-31.93, -22.07) * mm, "end": v(-35.56, -22.07) * mm});
            skLineSegment(sketch, "E17.4.0.54", {"start": v(-31.93, 18.43) * mm, "end": v(-31.93, 22.06) * mm});
            skLineSegment(sketch, "E17.4.0.55", {"start": v(-31.93, -18.44) * mm, "end": v(-35.56, -18.44) * mm});
            skLineSegment(sketch, "E17.4.0.56", {"start": v(-31.93, -8.57) * mm, "end": v(-31.93, -4.94) * mm});
            skLineSegment(sketch, "E17.4.0.57", {"start": v(-31.94, 18.43) * mm, "end": v(-35.57, 18.43) * mm});
            skLineSegment(sketch, "E17.4.0.58", {"start": v(-31.94, 35.56) * mm, "end": v(-35.57, 35.56) * mm});
            skLineSegment(sketch, "E17.4.0.59", {"start": v(-31.93, 4.93) * mm, "end": v(-31.93, 8.56) * mm});
            skLineSegment(sketch, "E17.4.0.60", {"start": v(-31.93, 27.43) * mm, "end": v(-35.56, 27.43) * mm});
            skLineSegment(sketch, "E17.4.0.61", {"start": v(-31.93, -8.57) * mm, "end": v(-35.56, -8.57) * mm});
            skLineSegment(sketch, "E17.4.0.62", {"start": v(-31.94, 8.56) * mm, "end": v(-35.57, 8.56) * mm});
            skLineSegment(sketch, "E17.4.0.63", {"start": v(-35.56, -17.57) * mm, "end": v(-35.56, -13.94) * mm});
            skLineSegment(sketch, "E17.4.0.64", {"start": v(-31.93, 22.93) * mm, "end": v(-35.56, 22.93) * mm});
            skLineSegment(sketch, "E17.4.0.65", {"start": v(-31.93, 22.93) * mm, "end": v(-31.93, 26.56) * mm});
            skLineSegment(sketch, "E17.5.0.0", {"start": v(-31.06, 27.43) * mm, "end": v(-31.06, 31.06) * mm});
            skLineSegment(sketch, "E17.5.0.1", {"start": v(-27.43, 27.43) * mm, "end": v(-27.43, 31.06) * mm});
            skLineSegment(sketch, "E17.5.0.2", {"start": v(-27.43, -13.07) * mm, "end": v(-27.43, -9.44) * mm});
            skLineSegment(sketch, "E17.5.0.3", {"start": v(-31.06, 9.43) * mm, "end": v(-31.06, 13.06) * mm});
            skLineSegment(sketch, "E17.5.0.4", {"start": v(-31.06, -13.07) * mm, "end": v(-31.06, -9.44) * mm});
            skLineSegment(sketch, "E17.5.0.5", {"start": v(-31.06, -31.07) * mm, "end": v(-31.06, -27.44) * mm});
            skPoint(sketch, "E17.5.0.6", {"position": v(-29.25, 33.75) * mm});
            skLineSegment(sketch, "E17.5.0.7", {"start": v(-27.43, 9.43) * mm, "end": v(-27.43, 13.06) * mm});
            skLineSegment(sketch, "E17.5.0.8", {"start": v(-27.43, -31.07) * mm, "end": v(-27.43, -27.44) * mm});
            skLineSegment(sketch, "E17.5.0.9", {"start": v(-27.43, 31.93) * mm, "end": v(-27.43, 27.43) * mm, "construction": true});
            skLineSegment(sketch, "E17.5.0.10", {"start": v(-27.43, 31.06) * mm, "end": v(-31.06, 31.06) * mm});
            skLineSegment(sketch, "E17.5.0.11", {"start": v(-27.44, 4.93) * mm, "end": v(-31.07, 4.93) * mm});
            skLineSegment(sketch, "E17.5.0.12", {"start": v(-27.43, -13.07) * mm, "end": v(-31.06, -13.07) * mm});
            skLineSegment(sketch, "E17.5.0.13", {"start": v(-27.43, -31.07) * mm, "end": v(-31.06, -31.07) * mm});
            skLineSegment(sketch, "E17.5.0.14", {"start": v(-31.06, 31.93) * mm, "end": v(-31.06, 35.56) * mm});
            skLineSegment(sketch, "E17.5.0.15", {"start": v(-27.43, 31.93) * mm, "end": v(-27.43, 35.56) * mm});
            skLineSegment(sketch, "E17.5.0.16", {"start": v(-27.44, 31.93) * mm, "end": v(-31.07, 31.93) * mm});
            skLineSegment(sketch, "E17.5.0.17", {"start": v(-31.06, 18.43) * mm, "end": v(-31.06, 22.06) * mm});
            skLineSegment(sketch, "E17.5.0.18", {"start": v(-27.44, 13.06) * mm, "end": v(-31.07, 13.06) * mm});
            skLineSegment(sketch, "E17.5.0.19", {"start": v(-27.43, -4.94) * mm, "end": v(-31.06, -4.94) * mm});
            skLineSegment(sketch, "E17.5.0.20", {"start": v(-27.43, -22.94) * mm, "end": v(-31.06, -22.94) * mm});
            skLineSegment(sketch, "E17.5.0.21", {"start": v(-27.43, -26.57) * mm, "end": v(-27.43, -22.94) * mm});
            skLineSegment(sketch, "E17.5.0.22", {"start": v(-31.06, -8.57) * mm, "end": v(-31.06, -4.94) * mm});
            skLineSegment(sketch, "E17.5.0.23", {"start": v(-31.06, -26.57) * mm, "end": v(-31.06, -22.94) * mm});
            skLineSegment(sketch, "E17.5.0.24", {"start": v(-27.44, 17.56) * mm, "end": v(-31.07, 17.56) * mm});
            skLineSegment(sketch, "E17.5.0.25", {"start": v(-27.43, -0.44) * mm, "end": v(-31.06, -0.44) * mm});
            skLineSegment(sketch, "E17.5.0.26", {"start": v(-27.43, -9.44) * mm, "end": v(-31.06, -9.44) * mm});
            skLineSegment(sketch, "E17.5.0.27", {"start": v(-31.06, -22.07) * mm, "end": v(-31.06, -18.44) * mm});
            skLineSegment(sketch, "E17.5.0.28", {"start": v(-31.06, 13.93) * mm, "end": v(-31.06, 17.56) * mm});
            skLineSegment(sketch, "E17.5.0.29", {"start": v(-31.06, -4.07) * mm, "end": v(-31.06, -0.44) * mm});
            skLineSegment(sketch, "E17.5.0.30", {"start": v(-27.44, 13.93) * mm, "end": v(-31.07, 13.93) * mm});
            skLineSegment(sketch, "E17.5.0.31", {"start": v(-27.43, -4.07) * mm, "end": v(-31.06, -4.07) * mm});
            skLineSegment(sketch, "E17.5.0.32", {"start": v(-27.43, -17.57) * mm, "end": v(-31.06, -17.57) * mm});
            skLineSegment(sketch, "E17.5.0.33", {"start": v(-27.43, -27.44) * mm, "end": v(-31.06, -27.44) * mm});
            skLineSegment(sketch, "E17.5.0.34", {"start": v(-27.43, -35.57) * mm, "end": v(-31.06, -35.57) * mm});
            skLineSegment(sketch, "E17.5.0.35", {"start": v(-27.43, 0.43) * mm, "end": v(-31.06, 0.43) * mm});
            skLineSegment(sketch, "E17.5.0.36", {"start": v(-27.43, 13.93) * mm, "end": v(-27.43, 17.56) * mm});
            skLineSegment(sketch, "E17.5.0.37", {"start": v(-27.43, -22.07) * mm, "end": v(-27.43, -18.44) * mm});
            skLineSegment(sketch, "E17.5.0.38", {"start": v(-27.43, -17.57) * mm, "end": v(-27.43, -13.94) * mm});
            skLineSegment(sketch, "E17.5.0.39", {"start": v(-31.06, 4.93) * mm, "end": v(-31.06, 8.56) * mm});
            skLineSegment(sketch, "E17.5.0.40", {"start": v(-27.43, 26.56) * mm, "end": v(-31.06, 26.56) * mm});
            skLineSegment(sketch, "E17.5.0.41", {"start": v(-27.44, 9.43) * mm, "end": v(-31.07, 9.43) * mm});
            skLineSegment(sketch, "E17.5.0.42", {"start": v(-31.06, 22.93) * mm, "end": v(-31.06, 26.56) * mm});
            skLineSegment(sketch, "E17.5.0.43", {"start": v(-27.43, -13.94) * mm, "end": v(-31.06, -13.94) * mm});
            skLineSegment(sketch, "E17.5.0.44", {"start": v(-27.43, -31.94) * mm, "end": v(-31.06, -31.94) * mm});
            skLineSegment(sketch, "E17.5.0.45", {"start": v(-27.44, 22.06) * mm, "end": v(-31.07, 22.06) * mm});
            skLineSegment(sketch, "E17.5.0.46", {"start": v(-27.43, 4.06) * mm, "end": v(-31.06, 4.06) * mm});
            skLineSegment(sketch, "E17.5.0.47", {"start": v(-31.06, 0.43) * mm, "end": v(-31.06, 4.06) * mm});
            skLineSegment(sketch, "E17.5.0.48", {"start": v(-31.06, -35.57) * mm, "end": v(-31.06, -31.94) * mm});
            skLineSegment(sketch, "E17.5.0.49", {"start": v(-27.43, 0.43) * mm, "end": v(-27.43, 4.06) * mm});
            skLineSegment(sketch, "E17.5.0.50", {"start": v(-27.43, -26.57) * mm, "end": v(-31.06, -26.57) * mm});
            skLineSegment(sketch, "E17.5.0.51", {"start": v(-27.43, -35.57) * mm, "end": v(-27.43, -31.94) * mm});
            skLineSegment(sketch, "E17.5.0.52", {"start": v(-27.43, -4.07) * mm, "end": v(-27.43, -0.44) * mm});
            skLineSegment(sketch, "E17.5.0.53", {"start": v(-27.43, -22.07) * mm, "end": v(-31.06, -22.07) * mm});
            skLineSegment(sketch, "E17.5.0.54", {"start": v(-27.43, 18.43) * mm, "end": v(-27.43, 22.06) * mm});
            skLineSegment(sketch, "E17.5.0.55", {"start": v(-27.43, -18.44) * mm, "end": v(-31.06, -18.44) * mm});
            skLineSegment(sketch, "E17.5.0.56", {"start": v(-27.43, -8.57) * mm, "end": v(-27.43, -4.94) * mm});
            skLineSegment(sketch, "E17.5.0.57", {"start": v(-27.44, 18.43) * mm, "end": v(-31.07, 18.43) * mm});
            skLineSegment(sketch, "E17.5.0.58", {"start": v(-27.44, 35.56) * mm, "end": v(-31.07, 35.56) * mm});
            skLineSegment(sketch, "E17.5.0.59", {"start": v(-27.43, 4.93) * mm, "end": v(-27.43, 8.56) * mm});
            skLineSegment(sketch, "E17.5.0.60", {"start": v(-27.43, 27.43) * mm, "end": v(-31.06, 27.43) * mm});
            skLineSegment(sketch, "E17.5.0.61", {"start": v(-27.43, -8.57) * mm, "end": v(-31.06, -8.57) * mm});
            skLineSegment(sketch, "E17.5.0.62", {"start": v(-27.44, 8.56) * mm, "end": v(-31.07, 8.56) * mm});
            skLineSegment(sketch, "E17.5.0.63", {"start": v(-31.06, -17.57) * mm, "end": v(-31.06, -13.94) * mm});
            skLineSegment(sketch, "E17.5.0.64", {"start": v(-27.43, 22.93) * mm, "end": v(-31.06, 22.93) * mm});
            skLineSegment(sketch, "E17.5.0.65", {"start": v(-27.43, 22.93) * mm, "end": v(-27.43, 26.56) * mm});
            skLineSegment(sketch, "E17.6.0.0", {"start": v(-26.56, 27.43) * mm, "end": v(-26.56, 31.06) * mm});
            skLineSegment(sketch, "E17.6.0.1", {"start": v(-22.93, 27.43) * mm, "end": v(-22.93, 31.06) * mm});
            skLineSegment(sketch, "E17.6.0.2", {"start": v(-22.93, -13.07) * mm, "end": v(-22.93, -9.44) * mm});
            skLineSegment(sketch, "E17.6.0.3", {"start": v(-26.56, 9.43) * mm, "end": v(-26.56, 13.06) * mm});
            skLineSegment(sketch, "E17.6.0.4", {"start": v(-26.56, -13.07) * mm, "end": v(-26.56, -9.44) * mm});
            skLineSegment(sketch, "E17.6.0.5", {"start": v(-26.56, -31.07) * mm, "end": v(-26.56, -27.44) * mm});
            skPoint(sketch, "E17.6.0.6", {"position": v(-24.75, 33.75) * mm});
            skLineSegment(sketch, "E17.6.0.7", {"start": v(-22.93, 9.43) * mm, "end": v(-22.93, 13.06) * mm});
            skLineSegment(sketch, "E17.6.0.8", {"start": v(-22.93, -31.07) * mm, "end": v(-22.93, -27.44) * mm});
            skLineSegment(sketch, "E17.6.0.9", {"start": v(-22.93, 31.93) * mm, "end": v(-22.93, 27.43) * mm, "construction": true});
            skLineSegment(sketch, "E17.6.0.10", {"start": v(-22.93, 31.06) * mm, "end": v(-26.56, 31.06) * mm});
            skLineSegment(sketch, "E17.6.0.11", {"start": v(-22.93, 4.93) * mm, "end": v(-26.56, 4.93) * mm});
            skLineSegment(sketch, "E17.6.0.12", {"start": v(-22.93, -13.07) * mm, "end": v(-26.56, -13.07) * mm});
            skLineSegment(sketch, "E17.6.0.13", {"start": v(-22.93, -31.07) * mm, "end": v(-26.56, -31.07) * mm});
            skLineSegment(sketch, "E17.6.0.14", {"start": v(-26.56, 31.93) * mm, "end": v(-26.56, 35.56) * mm});
            skLineSegment(sketch, "E17.6.0.15", {"start": v(-22.93, 31.93) * mm, "end": v(-22.93, 35.56) * mm});
            skLineSegment(sketch, "E17.6.0.16", {"start": v(-22.93, 31.93) * mm, "end": v(-26.56, 31.93) * mm});
            skLineSegment(sketch, "E17.6.0.17", {"start": v(-26.56, 18.43) * mm, "end": v(-26.56, 22.06) * mm});
            skLineSegment(sketch, "E17.6.0.18", {"start": v(-22.93, 13.06) * mm, "end": v(-26.56, 13.06) * mm});
            skLineSegment(sketch, "E17.6.0.19", {"start": v(-22.93, -4.94) * mm, "end": v(-26.56, -4.94) * mm});
            skLineSegment(sketch, "E17.6.0.20", {"start": v(-22.93, -22.94) * mm, "end": v(-26.56, -22.94) * mm});
            skLineSegment(sketch, "E17.6.0.21", {"start": v(-22.93, -26.57) * mm, "end": v(-22.93, -22.94) * mm});
            skLineSegment(sketch, "E17.6.0.22", {"start": v(-26.56, -8.57) * mm, "end": v(-26.56, -4.94) * mm});
            skLineSegment(sketch, "E17.6.0.23", {"start": v(-26.56, -26.57) * mm, "end": v(-26.56, -22.94) * mm});
            skLineSegment(sketch, "E17.6.0.24", {"start": v(-22.93, 17.56) * mm, "end": v(-26.56, 17.56) * mm});
            skLineSegment(sketch, "E17.6.0.25", {"start": v(-22.93, -0.44) * mm, "end": v(-26.56, -0.44) * mm});
            skLineSegment(sketch, "E17.6.0.26", {"start": v(-22.93, -9.44) * mm, "end": v(-26.56, -9.44) * mm});
            skLineSegment(sketch, "E17.6.0.27", {"start": v(-26.56, -22.07) * mm, "end": v(-26.56, -18.44) * mm});
            skLineSegment(sketch, "E17.6.0.28", {"start": v(-26.56, 13.93) * mm, "end": v(-26.56, 17.56) * mm});
            skLineSegment(sketch, "E17.6.0.29", {"start": v(-26.56, -4.07) * mm, "end": v(-26.56, -0.44) * mm});
            skLineSegment(sketch, "E17.6.0.30", {"start": v(-22.93, 13.93) * mm, "end": v(-26.56, 13.93) * mm});
            skLineSegment(sketch, "E17.6.0.31", {"start": v(-22.93, -4.07) * mm, "end": v(-26.56, -4.07) * mm});
            skLineSegment(sketch, "E17.6.0.32", {"start": v(-22.93, -17.57) * mm, "end": v(-26.56, -17.57) * mm});
            skLineSegment(sketch, "E17.6.0.33", {"start": v(-22.93, -27.44) * mm, "end": v(-26.56, -27.44) * mm});
            skLineSegment(sketch, "E17.6.0.34", {"start": v(-22.93, -35.57) * mm, "end": v(-26.56, -35.57) * mm});
            skLineSegment(sketch, "E17.6.0.35", {"start": v(-22.93, 0.43) * mm, "end": v(-26.56, 0.43) * mm});
            skLineSegment(sketch, "E17.6.0.36", {"start": v(-22.93, 13.93) * mm, "end": v(-22.93, 17.56) * mm});
            skLineSegment(sketch, "E17.6.0.37", {"start": v(-22.93, -22.07) * mm, "end": v(-22.93, -18.44) * mm});
            skLineSegment(sketch, "E17.6.0.38", {"start": v(-22.93, -17.57) * mm, "end": v(-22.93, -13.94) * mm});
            skLineSegment(sketch, "E17.6.0.39", {"start": v(-26.56, 4.93) * mm, "end": v(-26.56, 8.56) * mm});
            skLineSegment(sketch, "E17.6.0.40", {"start": v(-22.93, 26.56) * mm, "end": v(-26.56, 26.56) * mm});
            skLineSegment(sketch, "E17.6.0.41", {"start": v(-22.93, 9.43) * mm, "end": v(-26.56, 9.43) * mm});
            skLineSegment(sketch, "E17.6.0.42", {"start": v(-26.56, 22.93) * mm, "end": v(-26.56, 26.56) * mm});
            skLineSegment(sketch, "E17.6.0.43", {"start": v(-22.93, -13.94) * mm, "end": v(-26.56, -13.94) * mm});
            skLineSegment(sketch, "E17.6.0.44", {"start": v(-22.93, -31.94) * mm, "end": v(-26.56, -31.94) * mm});
            skLineSegment(sketch, "E17.6.0.45", {"start": v(-22.93, 22.06) * mm, "end": v(-26.56, 22.06) * mm});
            skLineSegment(sketch, "E17.6.0.46", {"start": v(-22.93, 4.06) * mm, "end": v(-26.56, 4.06) * mm});
            skLineSegment(sketch, "E17.6.0.47", {"start": v(-26.56, 0.43) * mm, "end": v(-26.56, 4.06) * mm});
            skLineSegment(sketch, "E17.6.0.48", {"start": v(-26.56, -35.57) * mm, "end": v(-26.56, -31.94) * mm});
            skLineSegment(sketch, "E17.6.0.49", {"start": v(-22.93, 0.43) * mm, "end": v(-22.93, 4.06) * mm});
            skLineSegment(sketch, "E17.6.0.50", {"start": v(-22.93, -26.57) * mm, "end": v(-26.56, -26.57) * mm});
            skLineSegment(sketch, "E17.6.0.51", {"start": v(-22.93, -35.57) * mm, "end": v(-22.93, -31.94) * mm});
            skLineSegment(sketch, "E17.6.0.52", {"start": v(-22.93, -4.07) * mm, "end": v(-22.93, -0.44) * mm});
            skLineSegment(sketch, "E17.6.0.53", {"start": v(-22.93, -22.07) * mm, "end": v(-26.56, -22.07) * mm});
            skLineSegment(sketch, "E17.6.0.54", {"start": v(-22.93, 18.43) * mm, "end": v(-22.93, 22.06) * mm});
            skLineSegment(sketch, "E17.6.0.55", {"start": v(-22.93, -18.44) * mm, "end": v(-26.56, -18.44) * mm});
            skLineSegment(sketch, "E17.6.0.56", {"start": v(-22.93, -8.57) * mm, "end": v(-22.93, -4.94) * mm});
            skLineSegment(sketch, "E17.6.0.57", {"start": v(-22.93, 18.43) * mm, "end": v(-26.56, 18.43) * mm});
            skLineSegment(sketch, "E17.6.0.58", {"start": v(-22.93, 35.56) * mm, "end": v(-26.56, 35.56) * mm});
            skLineSegment(sketch, "E17.6.0.59", {"start": v(-22.93, 4.93) * mm, "end": v(-22.93, 8.56) * mm});
            skLineSegment(sketch, "E17.6.0.60", {"start": v(-22.93, 27.43) * mm, "end": v(-26.56, 27.43) * mm});
            skLineSegment(sketch, "E17.6.0.61", {"start": v(-22.93, -8.57) * mm, "end": v(-26.56, -8.57) * mm});
            skLineSegment(sketch, "E17.6.0.62", {"start": v(-22.93, 8.56) * mm, "end": v(-26.56, 8.56) * mm});
            skLineSegment(sketch, "E17.6.0.63", {"start": v(-26.56, -17.57) * mm, "end": v(-26.56, -13.94) * mm});
            skLineSegment(sketch, "E17.6.0.64", {"start": v(-22.93, 22.93) * mm, "end": v(-26.56, 22.93) * mm});
            skLineSegment(sketch, "E17.6.0.65", {"start": v(-22.93, 22.93) * mm, "end": v(-22.93, 26.56) * mm});
            skLineSegment(sketch, "E17.7.0.0", {"start": v(-22.06, 27.43) * mm, "end": v(-22.06, 31.06) * mm});
            skLineSegment(sketch, "E17.7.0.1", {"start": v(-18.43, 27.43) * mm, "end": v(-18.43, 31.06) * mm});
            skLineSegment(sketch, "E17.7.0.2", {"start": v(-18.43, -13.07) * mm, "end": v(-18.43, -9.44) * mm});
            skLineSegment(sketch, "E17.7.0.3", {"start": v(-22.06, 9.43) * mm, "end": v(-22.06, 13.06) * mm});
            skLineSegment(sketch, "E17.7.0.4", {"start": v(-22.06, -13.07) * mm, "end": v(-22.06, -9.44) * mm});
            skLineSegment(sketch, "E17.7.0.5", {"start": v(-22.06, -31.07) * mm, "end": v(-22.06, -27.44) * mm});
            skPoint(sketch, "E17.7.0.6", {"position": v(-20.25, 33.75) * mm});
            skLineSegment(sketch, "E17.7.0.7", {"start": v(-18.43, 9.43) * mm, "end": v(-18.43, 13.06) * mm});
            skLineSegment(sketch, "E17.7.0.8", {"start": v(-18.43, -31.07) * mm, "end": v(-18.43, -27.44) * mm});
            skLineSegment(sketch, "E17.7.0.9", {"start": v(-18.43, 31.93) * mm, "end": v(-18.43, 27.43) * mm, "construction": true});
            skLineSegment(sketch, "E17.7.0.10", {"start": v(-18.43, 31.06) * mm, "end": v(-22.06, 31.06) * mm});
            skLineSegment(sketch, "E17.7.0.11", {"start": v(-18.43, 4.93) * mm, "end": v(-22.06, 4.93) * mm});
            skLineSegment(sketch, "E17.7.0.12", {"start": v(-18.43, -13.07) * mm, "end": v(-22.06, -13.07) * mm});
            skLineSegment(sketch, "E17.7.0.13", {"start": v(-18.43, -31.07) * mm, "end": v(-22.06, -31.07) * mm});
            skLineSegment(sketch, "E17.7.0.14", {"start": v(-22.06, 31.93) * mm, "end": v(-22.06, 35.56) * mm});
            skLineSegment(sketch, "E17.7.0.15", {"start": v(-18.43, 31.93) * mm, "end": v(-18.43, 35.56) * mm});
            skLineSegment(sketch, "E17.7.0.16", {"start": v(-18.43, 31.93) * mm, "end": v(-22.06, 31.93) * mm});
            skLineSegment(sketch, "E17.7.0.17", {"start": v(-22.06, 18.43) * mm, "end": v(-22.06, 22.06) * mm});
            skLineSegment(sketch, "E17.7.0.18", {"start": v(-18.43, 13.06) * mm, "end": v(-22.06, 13.06) * mm});
            skLineSegment(sketch, "E17.7.0.19", {"start": v(-18.43, -4.94) * mm, "end": v(-22.06, -4.94) * mm});
            skLineSegment(sketch, "E17.7.0.20", {"start": v(-18.43, -22.94) * mm, "end": v(-22.06, -22.94) * mm});
            skLineSegment(sketch, "E17.7.0.21", {"start": v(-18.43, -26.57) * mm, "end": v(-18.43, -22.94) * mm});
            skLineSegment(sketch, "E17.7.0.22", {"start": v(-22.06, -8.57) * mm, "end": v(-22.06, -4.94) * mm});
            skLineSegment(sketch, "E17.7.0.23", {"start": v(-22.06, -26.57) * mm, "end": v(-22.06, -22.94) * mm});
            skLineSegment(sketch, "E17.7.0.24", {"start": v(-18.43, 17.56) * mm, "end": v(-22.06, 17.56) * mm});
            skLineSegment(sketch, "E17.7.0.25", {"start": v(-18.43, -0.44) * mm, "end": v(-22.06, -0.44) * mm});
            skLineSegment(sketch, "E17.7.0.26", {"start": v(-18.43, -9.44) * mm, "end": v(-22.06, -9.44) * mm});
            skLineSegment(sketch, "E17.7.0.27", {"start": v(-22.06, -22.07) * mm, "end": v(-22.06, -18.44) * mm});
            skLineSegment(sketch, "E17.7.0.28", {"start": v(-22.06, 13.93) * mm, "end": v(-22.06, 17.56) * mm});
            skLineSegment(sketch, "E17.7.0.29", {"start": v(-22.06, -4.07) * mm, "end": v(-22.06, -0.44) * mm});
            skLineSegment(sketch, "E17.7.0.30", {"start": v(-18.43, 13.93) * mm, "end": v(-22.06, 13.93) * mm});
            skLineSegment(sketch, "E17.7.0.31", {"start": v(-18.43, -4.07) * mm, "end": v(-22.06, -4.07) * mm});
            skLineSegment(sketch, "E17.7.0.32", {"start": v(-18.43, -17.57) * mm, "end": v(-22.06, -17.57) * mm});
            skLineSegment(sketch, "E17.7.0.33", {"start": v(-18.43, -27.44) * mm, "end": v(-22.06, -27.44) * mm});
            skLineSegment(sketch, "E17.7.0.34", {"start": v(-18.43, -35.57) * mm, "end": v(-22.06, -35.57) * mm});
            skLineSegment(sketch, "E17.7.0.35", {"start": v(-18.43, 0.43) * mm, "end": v(-22.06, 0.43) * mm});
            skLineSegment(sketch, "E17.7.0.36", {"start": v(-18.43, 13.93) * mm, "end": v(-18.43, 17.56) * mm});
            skLineSegment(sketch, "E17.7.0.37", {"start": v(-18.43, -22.07) * mm, "end": v(-18.43, -18.44) * mm});
            skLineSegment(sketch, "E17.7.0.38", {"start": v(-18.43, -17.57) * mm, "end": v(-18.43, -13.94) * mm});
            skLineSegment(sketch, "E17.7.0.39", {"start": v(-22.06, 4.93) * mm, "end": v(-22.06, 8.56) * mm});
            skLineSegment(sketch, "E17.7.0.40", {"start": v(-18.43, 26.56) * mm, "end": v(-22.06, 26.56) * mm});
            skLineSegment(sketch, "E17.7.0.41", {"start": v(-18.43, 9.43) * mm, "end": v(-22.06, 9.43) * mm});
            skLineSegment(sketch, "E17.7.0.42", {"start": v(-22.06, 22.93) * mm, "end": v(-22.06, 26.56) * mm});
            skLineSegment(sketch, "E17.7.0.43", {"start": v(-18.43, -13.94) * mm, "end": v(-22.06, -13.94) * mm});
            skLineSegment(sketch, "E17.7.0.44", {"start": v(-18.43, -31.94) * mm, "end": v(-22.06, -31.94) * mm});
            skLineSegment(sketch, "E17.7.0.45", {"start": v(-18.43, 22.06) * mm, "end": v(-22.06, 22.06) * mm});
            skLineSegment(sketch, "E17.7.0.46", {"start": v(-18.43, 4.06) * mm, "end": v(-22.06, 4.06) * mm});
            skLineSegment(sketch, "E17.7.0.47", {"start": v(-22.06, 0.43) * mm, "end": v(-22.06, 4.06) * mm});
            skLineSegment(sketch, "E17.7.0.48", {"start": v(-22.06, -35.57) * mm, "end": v(-22.06, -31.94) * mm});
            skLineSegment(sketch, "E17.7.0.49", {"start": v(-18.43, 0.43) * mm, "end": v(-18.43, 4.06) * mm});
            skLineSegment(sketch, "E17.7.0.50", {"start": v(-18.43, -26.57) * mm, "end": v(-22.06, -26.57) * mm});
            skLineSegment(sketch, "E17.7.0.51", {"start": v(-18.43, -35.57) * mm, "end": v(-18.43, -31.94) * mm});
            skLineSegment(sketch, "E17.7.0.52", {"start": v(-18.43, -4.07) * mm, "end": v(-18.43, -0.44) * mm});
            skLineSegment(sketch, "E17.7.0.53", {"start": v(-18.43, -22.07) * mm, "end": v(-22.06, -22.07) * mm});
            skLineSegment(sketch, "E17.7.0.54", {"start": v(-18.43, 18.43) * mm, "end": v(-18.43, 22.06) * mm});
            skLineSegment(sketch, "E17.7.0.55", {"start": v(-18.43, -18.44) * mm, "end": v(-22.06, -18.44) * mm});
            skLineSegment(sketch, "E17.7.0.56", {"start": v(-18.43, -8.57) * mm, "end": v(-18.43, -4.94) * mm});
            skLineSegment(sketch, "E17.7.0.57", {"start": v(-18.43, 18.43) * mm, "end": v(-22.06, 18.43) * mm});
            skLineSegment(sketch, "E17.7.0.58", {"start": v(-18.43, 35.56) * mm, "end": v(-22.06, 35.56) * mm});
            skLineSegment(sketch, "E17.7.0.59", {"start": v(-18.43, 4.93) * mm, "end": v(-18.43, 8.56) * mm});
            skLineSegment(sketch, "E17.7.0.60", {"start": v(-18.43, 27.43) * mm, "end": v(-22.06, 27.43) * mm});
            skLineSegment(sketch, "E17.7.0.61", {"start": v(-18.43, -8.57) * mm, "end": v(-22.06, -8.57) * mm});
            skLineSegment(sketch, "E17.7.0.62", {"start": v(-18.43, 8.56) * mm, "end": v(-22.06, 8.56) * mm});
            skLineSegment(sketch, "E17.7.0.63", {"start": v(-22.06, -17.57) * mm, "end": v(-22.06, -13.94) * mm});
            skLineSegment(sketch, "E17.7.0.64", {"start": v(-18.43, 22.93) * mm, "end": v(-22.06, 22.93) * mm});
            skLineSegment(sketch, "E17.7.0.65", {"start": v(-18.43, 22.93) * mm, "end": v(-18.43, 26.56) * mm});
            skLineSegment(sketch, "E17.8.0.0", {"start": v(-17.56, 27.43) * mm, "end": v(-17.56, 31.06) * mm});
            skLineSegment(sketch, "E17.8.0.1", {"start": v(-13.93, 27.43) * mm, "end": v(-13.93, 31.06) * mm});
            skLineSegment(sketch, "E17.8.0.2", {"start": v(-13.93, -13.07) * mm, "end": v(-13.93, -9.44) * mm});
            skLineSegment(sketch, "E17.8.0.3", {"start": v(-17.56, 9.43) * mm, "end": v(-17.56, 13.06) * mm});
            skLineSegment(sketch, "E17.8.0.4", {"start": v(-17.56, -13.07) * mm, "end": v(-17.56, -9.44) * mm});
            skLineSegment(sketch, "E17.8.0.5", {"start": v(-17.56, -31.07) * mm, "end": v(-17.56, -27.44) * mm});
            skPoint(sketch, "E17.8.0.6", {"position": v(-15.75, 33.75) * mm});
            skLineSegment(sketch, "E17.8.0.7", {"start": v(-13.93, 9.43) * mm, "end": v(-13.93, 13.06) * mm});
            skLineSegment(sketch, "E17.8.0.8", {"start": v(-13.93, -31.07) * mm, "end": v(-13.93, -27.44) * mm});
            skLineSegment(sketch, "E17.8.0.9", {"start": v(-13.93, 31.93) * mm, "end": v(-13.93, 27.43) * mm, "construction": true});
            skLineSegment(sketch, "E17.8.0.10", {"start": v(-13.93, 31.06) * mm, "end": v(-17.56, 31.06) * mm});
            skLineSegment(sketch, "E17.8.0.11", {"start": v(-13.93, 4.93) * mm, "end": v(-17.56, 4.93) * mm});
            skLineSegment(sketch, "E17.8.0.12", {"start": v(-13.93, -13.07) * mm, "end": v(-17.56, -13.07) * mm});
            skLineSegment(sketch, "E17.8.0.13", {"start": v(-13.93, -31.07) * mm, "end": v(-17.56, -31.07) * mm});
            skLineSegment(sketch, "E17.8.0.14", {"start": v(-17.56, 31.93) * mm, "end": v(-17.56, 35.56) * mm});
            skLineSegment(sketch, "E17.8.0.15", {"start": v(-13.93, 31.93) * mm, "end": v(-13.93, 35.56) * mm});
            skLineSegment(sketch, "E17.8.0.16", {"start": v(-13.93, 31.93) * mm, "end": v(-17.56, 31.93) * mm});
            skLineSegment(sketch, "E17.8.0.17", {"start": v(-17.56, 18.43) * mm, "end": v(-17.56, 22.06) * mm});
            skLineSegment(sketch, "E17.8.0.18", {"start": v(-13.93, 13.06) * mm, "end": v(-17.56, 13.06) * mm});
            skLineSegment(sketch, "E17.8.0.19", {"start": v(-13.93, -4.94) * mm, "end": v(-17.56, -4.94) * mm});
            skLineSegment(sketch, "E17.8.0.20", {"start": v(-13.93, -22.94) * mm, "end": v(-17.56, -22.94) * mm});
            skLineSegment(sketch, "E17.8.0.21", {"start": v(-13.93, -26.57) * mm, "end": v(-13.93, -22.94) * mm});
            skLineSegment(sketch, "E17.8.0.22", {"start": v(-17.56, -8.57) * mm, "end": v(-17.56, -4.94) * mm});
            skLineSegment(sketch, "E17.8.0.23", {"start": v(-17.56, -26.57) * mm, "end": v(-17.56, -22.94) * mm});
            skLineSegment(sketch, "E17.8.0.24", {"start": v(-13.93, 17.56) * mm, "end": v(-17.56, 17.56) * mm});
            skLineSegment(sketch, "E17.8.0.25", {"start": v(-13.93, -0.44) * mm, "end": v(-17.56, -0.44) * mm});
            skLineSegment(sketch, "E17.8.0.26", {"start": v(-13.93, -9.44) * mm, "end": v(-17.56, -9.44) * mm});
            skLineSegment(sketch, "E17.8.0.27", {"start": v(-17.56, -22.07) * mm, "end": v(-17.56, -18.44) * mm});
            skLineSegment(sketch, "E17.8.0.28", {"start": v(-17.56, 13.93) * mm, "end": v(-17.56, 17.56) * mm});
            skLineSegment(sketch, "E17.8.0.29", {"start": v(-17.56, -4.07) * mm, "end": v(-17.56, -0.44) * mm});
            skLineSegment(sketch, "E17.8.0.30", {"start": v(-13.93, 13.93) * mm, "end": v(-17.56, 13.93) * mm});
            skLineSegment(sketch, "E17.8.0.31", {"start": v(-13.93, -4.07) * mm, "end": v(-17.56, -4.07) * mm});
            skLineSegment(sketch, "E17.8.0.32", {"start": v(-13.93, -17.57) * mm, "end": v(-17.56, -17.57) * mm});
            skLineSegment(sketch, "E17.8.0.33", {"start": v(-13.93, -27.44) * mm, "end": v(-17.56, -27.44) * mm});
            skLineSegment(sketch, "E17.8.0.34", {"start": v(-13.93, -35.57) * mm, "end": v(-17.56, -35.57) * mm});
            skLineSegment(sketch, "E17.8.0.35", {"start": v(-13.93, 0.43) * mm, "end": v(-17.56, 0.43) * mm});
            skLineSegment(sketch, "E17.8.0.36", {"start": v(-13.93, 13.93) * mm, "end": v(-13.93, 17.56) * mm});
            skLineSegment(sketch, "E17.8.0.37", {"start": v(-13.93, -22.07) * mm, "end": v(-13.93, -18.44) * mm});
            skLineSegment(sketch, "E17.8.0.38", {"start": v(-13.93, -17.57) * mm, "end": v(-13.93, -13.94) * mm});
            skLineSegment(sketch, "E17.8.0.39", {"start": v(-17.56, 4.93) * mm, "end": v(-17.56, 8.56) * mm});
            skLineSegment(sketch, "E17.8.0.40", {"start": v(-13.93, 26.56) * mm, "end": v(-17.56, 26.56) * mm});
            skLineSegment(sketch, "E17.8.0.41", {"start": v(-13.93, 9.43) * mm, "end": v(-17.56, 9.43) * mm});
            skLineSegment(sketch, "E17.8.0.42", {"start": v(-17.56, 22.93) * mm, "end": v(-17.56, 26.56) * mm});
            skLineSegment(sketch, "E17.8.0.43", {"start": v(-13.93, -13.94) * mm, "end": v(-17.56, -13.94) * mm});
            skLineSegment(sketch, "E17.8.0.44", {"start": v(-13.93, -31.94) * mm, "end": v(-17.56, -31.94) * mm});
            skLineSegment(sketch, "E17.8.0.45", {"start": v(-13.93, 22.06) * mm, "end": v(-17.56, 22.06) * mm});
            skLineSegment(sketch, "E17.8.0.46", {"start": v(-13.93, 4.06) * mm, "end": v(-17.56, 4.06) * mm});
            skLineSegment(sketch, "E17.8.0.47", {"start": v(-17.56, 0.43) * mm, "end": v(-17.56, 4.06) * mm});
            skLineSegment(sketch, "E17.8.0.48", {"start": v(-17.56, -35.57) * mm, "end": v(-17.56, -31.94) * mm});
            skLineSegment(sketch, "E17.8.0.49", {"start": v(-13.93, 0.43) * mm, "end": v(-13.93, 4.06) * mm});
            skLineSegment(sketch, "E17.8.0.50", {"start": v(-13.93, -26.57) * mm, "end": v(-17.56, -26.57) * mm});
            skLineSegment(sketch, "E17.8.0.51", {"start": v(-13.93, -35.57) * mm, "end": v(-13.93, -31.94) * mm});
            skLineSegment(sketch, "E17.8.0.52", {"start": v(-13.93, -4.07) * mm, "end": v(-13.93, -0.44) * mm});
            skLineSegment(sketch, "E17.8.0.53", {"start": v(-13.93, -22.07) * mm, "end": v(-17.56, -22.07) * mm});
            skLineSegment(sketch, "E17.8.0.54", {"start": v(-13.93, 18.43) * mm, "end": v(-13.93, 22.06) * mm});
            skLineSegment(sketch, "E17.8.0.55", {"start": v(-13.93, -18.44) * mm, "end": v(-17.56, -18.44) * mm});
            skLineSegment(sketch, "E17.8.0.56", {"start": v(-13.93, -8.57) * mm, "end": v(-13.93, -4.94) * mm});
            skLineSegment(sketch, "E17.8.0.57", {"start": v(-13.93, 18.43) * mm, "end": v(-17.56, 18.43) * mm});
            skLineSegment(sketch, "E17.8.0.58", {"start": v(-13.93, 35.56) * mm, "end": v(-17.56, 35.56) * mm});
            skLineSegment(sketch, "E17.8.0.59", {"start": v(-13.93, 4.93) * mm, "end": v(-13.93, 8.56) * mm});
            skLineSegment(sketch, "E17.8.0.60", {"start": v(-13.93, 27.43) * mm, "end": v(-17.56, 27.43) * mm});
            skLineSegment(sketch, "E17.8.0.61", {"start": v(-13.93, -8.57) * mm, "end": v(-17.56, -8.57) * mm});
            skLineSegment(sketch, "E17.8.0.62", {"start": v(-13.93, 8.56) * mm, "end": v(-17.56, 8.56) * mm});
            skLineSegment(sketch, "E17.8.0.63", {"start": v(-17.56, -17.57) * mm, "end": v(-17.56, -13.94) * mm});
            skLineSegment(sketch, "E17.8.0.64", {"start": v(-13.93, 22.93) * mm, "end": v(-17.56, 22.93) * mm});
            skLineSegment(sketch, "E17.8.0.65", {"start": v(-13.93, 22.93) * mm, "end": v(-13.93, 26.56) * mm});
            skLineSegment(sketch, "E17.9.0.0", {"start": v(-13.06, 27.43) * mm, "end": v(-13.06, 31.06) * mm});
            skLineSegment(sketch, "E17.9.0.1", {"start": v(-9.43, 27.43) * mm, "end": v(-9.43, 31.06) * mm});
            skLineSegment(sketch, "E17.9.0.2", {"start": v(-9.43, -13.07) * mm, "end": v(-9.43, -9.44) * mm});
            skLineSegment(sketch, "E17.9.0.3", {"start": v(-13.06, 9.43) * mm, "end": v(-13.06, 13.06) * mm});
            skLineSegment(sketch, "E17.9.0.4", {"start": v(-13.06, -13.07) * mm, "end": v(-13.06, -9.44) * mm});
            skLineSegment(sketch, "E17.9.0.5", {"start": v(-13.06, -31.07) * mm, "end": v(-13.06, -27.44) * mm});
            skPoint(sketch, "E17.9.0.6", {"position": v(-11.25, 33.75) * mm});
            skLineSegment(sketch, "E17.9.0.7", {"start": v(-9.43, 9.43) * mm, "end": v(-9.43, 13.06) * mm});
            skLineSegment(sketch, "E17.9.0.8", {"start": v(-9.43, -31.07) * mm, "end": v(-9.43, -27.44) * mm});
            skLineSegment(sketch, "E17.9.0.9", {"start": v(-9.43, 31.93) * mm, "end": v(-9.43, 27.43) * mm, "construction": true});
            skLineSegment(sketch, "E17.9.0.10", {"start": v(-9.43, 31.06) * mm, "end": v(-13.06, 31.06) * mm});
            skLineSegment(sketch, "E17.9.0.11", {"start": v(-9.43, 4.93) * mm, "end": v(-13.06, 4.93) * mm});
            skLineSegment(sketch, "E17.9.0.12", {"start": v(-9.43, -13.07) * mm, "end": v(-13.06, -13.07) * mm});
            skLineSegment(sketch, "E17.9.0.13", {"start": v(-9.43, -31.07) * mm, "end": v(-13.06, -31.07) * mm});
            skLineSegment(sketch, "E17.9.0.14", {"start": v(-13.06, 31.93) * mm, "end": v(-13.06, 35.56) * mm});
            skLineSegment(sketch, "E17.9.0.15", {"start": v(-9.43, 31.93) * mm, "end": v(-9.43, 35.56) * mm});
            skLineSegment(sketch, "E17.9.0.16", {"start": v(-9.43, 31.93) * mm, "end": v(-13.06, 31.93) * mm});
            skLineSegment(sketch, "E17.9.0.17", {"start": v(-13.06, 18.43) * mm, "end": v(-13.06, 22.06) * mm});
            skLineSegment(sketch, "E17.9.0.18", {"start": v(-9.43, 13.06) * mm, "end": v(-13.06, 13.06) * mm});
            skLineSegment(sketch, "E17.9.0.19", {"start": v(-9.43, -4.94) * mm, "end": v(-13.06, -4.94) * mm});
            skLineSegment(sketch, "E17.9.0.20", {"start": v(-9.43, -22.94) * mm, "end": v(-13.06, -22.94) * mm});
            skLineSegment(sketch, "E17.9.0.21", {"start": v(-9.43, -26.57) * mm, "end": v(-9.43, -22.94) * mm});
            skLineSegment(sketch, "E17.9.0.22", {"start": v(-13.06, -8.57) * mm, "end": v(-13.06, -4.94) * mm});
            skLineSegment(sketch, "E17.9.0.23", {"start": v(-13.06, -26.57) * mm, "end": v(-13.06, -22.94) * mm});
            skLineSegment(sketch, "E17.9.0.24", {"start": v(-9.43, 17.56) * mm, "end": v(-13.06, 17.56) * mm});
            skLineSegment(sketch, "E17.9.0.25", {"start": v(-9.43, -0.44) * mm, "end": v(-13.06, -0.44) * mm});
            skLineSegment(sketch, "E17.9.0.26", {"start": v(-9.43, -9.44) * mm, "end": v(-13.06, -9.44) * mm});
            skLineSegment(sketch, "E17.9.0.27", {"start": v(-13.06, -22.07) * mm, "end": v(-13.06, -18.44) * mm});
            skLineSegment(sketch, "E17.9.0.28", {"start": v(-13.06, 13.93) * mm, "end": v(-13.06, 17.56) * mm});
            skLineSegment(sketch, "E17.9.0.29", {"start": v(-13.06, -4.07) * mm, "end": v(-13.06, -0.44) * mm});
            skLineSegment(sketch, "E17.9.0.30", {"start": v(-9.43, 13.93) * mm, "end": v(-13.06, 13.93) * mm});
            skLineSegment(sketch, "E17.9.0.31", {"start": v(-9.43, -4.07) * mm, "end": v(-13.06, -4.07) * mm});
            skLineSegment(sketch, "E17.9.0.32", {"start": v(-9.43, -17.57) * mm, "end": v(-13.06, -17.57) * mm});
            skLineSegment(sketch, "E17.9.0.33", {"start": v(-9.43, -27.44) * mm, "end": v(-13.06, -27.44) * mm});
            skLineSegment(sketch, "E17.9.0.34", {"start": v(-9.43, -35.57) * mm, "end": v(-13.06, -35.57) * mm});
            skLineSegment(sketch, "E17.9.0.35", {"start": v(-9.43, 0.43) * mm, "end": v(-13.06, 0.43) * mm});
            skLineSegment(sketch, "E17.9.0.36", {"start": v(-9.43, 13.93) * mm, "end": v(-9.43, 17.56) * mm});
            skLineSegment(sketch, "E17.9.0.37", {"start": v(-9.43, -22.07) * mm, "end": v(-9.43, -18.44) * mm});
            skLineSegment(sketch, "E17.9.0.38", {"start": v(-9.43, -17.57) * mm, "end": v(-9.43, -13.94) * mm});
            skLineSegment(sketch, "E17.9.0.39", {"start": v(-13.06, 4.93) * mm, "end": v(-13.06, 8.56) * mm});
            skLineSegment(sketch, "E17.9.0.40", {"start": v(-9.43, 26.56) * mm, "end": v(-13.06, 26.56) * mm});
            skLineSegment(sketch, "E17.9.0.41", {"start": v(-9.43, 9.43) * mm, "end": v(-13.06, 9.43) * mm});
            skLineSegment(sketch, "E17.9.0.42", {"start": v(-13.06, 22.93) * mm, "end": v(-13.06, 26.56) * mm});
            skLineSegment(sketch, "E17.9.0.43", {"start": v(-9.43, -13.94) * mm, "end": v(-13.06, -13.94) * mm});
            skLineSegment(sketch, "E17.9.0.44", {"start": v(-9.43, -31.94) * mm, "end": v(-13.06, -31.94) * mm});
            skLineSegment(sketch, "E17.9.0.45", {"start": v(-9.43, 22.06) * mm, "end": v(-13.06, 22.06) * mm});
            skLineSegment(sketch, "E17.9.0.46", {"start": v(-9.43, 4.06) * mm, "end": v(-13.06, 4.06) * mm});
            skLineSegment(sketch, "E17.9.0.47", {"start": v(-13.06, 0.43) * mm, "end": v(-13.06, 4.06) * mm});
            skLineSegment(sketch, "E17.9.0.48", {"start": v(-13.06, -35.57) * mm, "end": v(-13.06, -31.94) * mm});
            skLineSegment(sketch, "E17.9.0.49", {"start": v(-9.43, 0.43) * mm, "end": v(-9.43, 4.06) * mm});
            skLineSegment(sketch, "E17.9.0.50", {"start": v(-9.43, -26.57) * mm, "end": v(-13.06, -26.57) * mm});
            skLineSegment(sketch, "E17.9.0.51", {"start": v(-9.43, -35.57) * mm, "end": v(-9.43, -31.94) * mm});
            skLineSegment(sketch, "E17.9.0.52", {"start": v(-9.43, -4.07) * mm, "end": v(-9.43, -0.44) * mm});
            skLineSegment(sketch, "E17.9.0.53", {"start": v(-9.43, -22.07) * mm, "end": v(-13.06, -22.07) * mm});
            skLineSegment(sketch, "E17.9.0.54", {"start": v(-9.43, 18.43) * mm, "end": v(-9.43, 22.06) * mm});
            skLineSegment(sketch, "E17.9.0.55", {"start": v(-9.43, -18.44) * mm, "end": v(-13.06, -18.44) * mm});
            skLineSegment(sketch, "E17.9.0.56", {"start": v(-9.43, -8.57) * mm, "end": v(-9.43, -4.94) * mm});
            skLineSegment(sketch, "E17.9.0.57", {"start": v(-9.43, 18.43) * mm, "end": v(-13.06, 18.43) * mm});
            skLineSegment(sketch, "E17.9.0.58", {"start": v(-9.43, 35.56) * mm, "end": v(-13.06, 35.56) * mm});
            skLineSegment(sketch, "E17.9.0.59", {"start": v(-9.43, 4.93) * mm, "end": v(-9.43, 8.56) * mm});
            skLineSegment(sketch, "E17.9.0.60", {"start": v(-9.43, 27.43) * mm, "end": v(-13.06, 27.43) * mm});
            skLineSegment(sketch, "E17.9.0.61", {"start": v(-9.43, -8.57) * mm, "end": v(-13.06, -8.57) * mm});
            skLineSegment(sketch, "E17.9.0.62", {"start": v(-9.43, 8.56) * mm, "end": v(-13.06, 8.56) * mm});
            skLineSegment(sketch, "E17.9.0.63", {"start": v(-13.06, -17.57) * mm, "end": v(-13.06, -13.94) * mm});
            skLineSegment(sketch, "E17.9.0.64", {"start": v(-9.43, 22.93) * mm, "end": v(-13.06, 22.93) * mm});
            skLineSegment(sketch, "E17.9.0.65", {"start": v(-9.43, 22.93) * mm, "end": v(-9.43, 26.56) * mm});
            skLineSegment(sketch, "E17.10.0.0", {"start": v(-8.56, 27.43) * mm, "end": v(-8.56, 31.06) * mm});
            skLineSegment(sketch, "E17.10.0.1", {"start": v(-4.93, 27.43) * mm, "end": v(-4.93, 31.06) * mm});
            skLineSegment(sketch, "E17.10.0.2", {"start": v(-4.93, -13.07) * mm, "end": v(-4.93, -9.44) * mm});
            skLineSegment(sketch, "E17.10.0.3", {"start": v(-8.56, 9.43) * mm, "end": v(-8.56, 13.06) * mm});
            skLineSegment(sketch, "E17.10.0.4", {"start": v(-8.56, -13.07) * mm, "end": v(-8.56, -9.44) * mm});
            skLineSegment(sketch, "E17.10.0.5", {"start": v(-8.56, -31.07) * mm, "end": v(-8.56, -27.44) * mm});
            skPoint(sketch, "E17.10.0.6", {"position": v(-6.75, 33.75) * mm});
            skLineSegment(sketch, "E17.10.0.7", {"start": v(-4.93, 9.43) * mm, "end": v(-4.93, 13.06) * mm});
            skLineSegment(sketch, "E17.10.0.8", {"start": v(-4.93, -31.07) * mm, "end": v(-4.93, -27.44) * mm});
            skLineSegment(sketch, "E17.10.0.9", {"start": v(-4.93, 31.93) * mm, "end": v(-4.93, 27.43) * mm, "construction": true});
            skLineSegment(sketch, "E17.10.0.10", {"start": v(-4.93, 31.06) * mm, "end": v(-8.56, 31.06) * mm});
            skLineSegment(sketch, "E17.10.0.11", {"start": v(-4.93, 4.93) * mm, "end": v(-8.56, 4.93) * mm});
            skLineSegment(sketch, "E17.10.0.12", {"start": v(-4.93, -13.07) * mm, "end": v(-8.56, -13.07) * mm});
            skLineSegment(sketch, "E17.10.0.13", {"start": v(-4.93, -31.07) * mm, "end": v(-8.56, -31.07) * mm});
            skLineSegment(sketch, "E17.10.0.14", {"start": v(-8.56, 31.93) * mm, "end": v(-8.56, 35.56) * mm});
            skLineSegment(sketch, "E17.10.0.15", {"start": v(-4.93, 31.93) * mm, "end": v(-4.93, 35.56) * mm});
            skLineSegment(sketch, "E17.10.0.16", {"start": v(-4.93, 31.93) * mm, "end": v(-8.56, 31.93) * mm});
            skLineSegment(sketch, "E17.10.0.17", {"start": v(-8.56, 18.43) * mm, "end": v(-8.56, 22.06) * mm});
            skLineSegment(sketch, "E17.10.0.18", {"start": v(-4.93, 13.06) * mm, "end": v(-8.56, 13.06) * mm});
            skLineSegment(sketch, "E17.10.0.19", {"start": v(-4.93, -4.94) * mm, "end": v(-8.56, -4.94) * mm});
            skLineSegment(sketch, "E17.10.0.20", {"start": v(-4.93, -22.94) * mm, "end": v(-8.56, -22.94) * mm});
            skLineSegment(sketch, "E17.10.0.21", {"start": v(-4.93, -26.57) * mm, "end": v(-4.93, -22.94) * mm});
            skLineSegment(sketch, "E17.10.0.22", {"start": v(-8.56, -8.57) * mm, "end": v(-8.56, -4.94) * mm});
            skLineSegment(sketch, "E17.10.0.23", {"start": v(-8.56, -26.57) * mm, "end": v(-8.56, -22.94) * mm});
            skLineSegment(sketch, "E17.10.0.24", {"start": v(-4.93, 17.56) * mm, "end": v(-8.56, 17.56) * mm});
            skLineSegment(sketch, "E17.10.0.25", {"start": v(-4.93, -0.44) * mm, "end": v(-8.56, -0.44) * mm});
            skLineSegment(sketch, "E17.10.0.26", {"start": v(-4.93, -9.44) * mm, "end": v(-8.56, -9.44) * mm});
            skLineSegment(sketch, "E17.10.0.27", {"start": v(-8.56, -22.07) * mm, "end": v(-8.56, -18.44) * mm});
            skLineSegment(sketch, "E17.10.0.28", {"start": v(-8.56, 13.93) * mm, "end": v(-8.56, 17.56) * mm});
            skLineSegment(sketch, "E17.10.0.29", {"start": v(-8.56, -4.07) * mm, "end": v(-8.56, -0.44) * mm});
            skLineSegment(sketch, "E17.10.0.30", {"start": v(-4.93, 13.93) * mm, "end": v(-8.56, 13.93) * mm});
            skLineSegment(sketch, "E17.10.0.31", {"start": v(-4.93, -4.07) * mm, "end": v(-8.56, -4.07) * mm});
            skLineSegment(sketch, "E17.10.0.32", {"start": v(-4.93, -17.57) * mm, "end": v(-8.56, -17.57) * mm});
            skLineSegment(sketch, "E17.10.0.33", {"start": v(-4.93, -27.44) * mm, "end": v(-8.56, -27.44) * mm});
            skLineSegment(sketch, "E17.10.0.34", {"start": v(-4.93, -35.57) * mm, "end": v(-8.56, -35.57) * mm});
            skLineSegment(sketch, "E17.10.0.35", {"start": v(-4.93, 0.43) * mm, "end": v(-8.56, 0.43) * mm});
            skLineSegment(sketch, "E17.10.0.36", {"start": v(-4.93, 13.93) * mm, "end": v(-4.93, 17.56) * mm});
            skLineSegment(sketch, "E17.10.0.37", {"start": v(-4.93, -22.07) * mm, "end": v(-4.93, -18.44) * mm});
            skLineSegment(sketch, "E17.10.0.38", {"start": v(-4.93, -17.57) * mm, "end": v(-4.93, -13.94) * mm});
            skLineSegment(sketch, "E17.10.0.39", {"start": v(-8.56, 4.93) * mm, "end": v(-8.56, 8.56) * mm});
            skLineSegment(sketch, "E17.10.0.40", {"start": v(-4.93, 26.56) * mm, "end": v(-8.56, 26.56) * mm});
            skLineSegment(sketch, "E17.10.0.41", {"start": v(-4.93, 9.43) * mm, "end": v(-8.56, 9.43) * mm});
            skLineSegment(sketch, "E17.10.0.42", {"start": v(-8.56, 22.93) * mm, "end": v(-8.56, 26.56) * mm});
            skLineSegment(sketch, "E17.10.0.43", {"start": v(-4.93, -13.94) * mm, "end": v(-8.56, -13.94) * mm});
            skLineSegment(sketch, "E17.10.0.44", {"start": v(-4.93, -31.94) * mm, "end": v(-8.56, -31.94) * mm});
            skLineSegment(sketch, "E17.10.0.45", {"start": v(-4.93, 22.06) * mm, "end": v(-8.56, 22.06) * mm});
            skLineSegment(sketch, "E17.10.0.46", {"start": v(-4.93, 4.06) * mm, "end": v(-8.56, 4.06) * mm});
            skLineSegment(sketch, "E17.10.0.47", {"start": v(-8.56, 0.43) * mm, "end": v(-8.56, 4.06) * mm});
            skLineSegment(sketch, "E17.10.0.48", {"start": v(-8.56, -35.57) * mm, "end": v(-8.56, -31.94) * mm});
            skLineSegment(sketch, "E17.10.0.49", {"start": v(-4.93, 0.43) * mm, "end": v(-4.93, 4.06) * mm});
            skLineSegment(sketch, "E17.10.0.50", {"start": v(-4.93, -26.57) * mm, "end": v(-8.56, -26.57) * mm});
            skLineSegment(sketch, "E17.10.0.51", {"start": v(-4.93, -35.57) * mm, "end": v(-4.93, -31.94) * mm});
            skLineSegment(sketch, "E17.10.0.52", {"start": v(-4.93, -4.07) * mm, "end": v(-4.93, -0.44) * mm});
            skLineSegment(sketch, "E17.10.0.53", {"start": v(-4.93, -22.07) * mm, "end": v(-8.56, -22.07) * mm});
            skLineSegment(sketch, "E17.10.0.54", {"start": v(-4.93, 18.43) * mm, "end": v(-4.93, 22.06) * mm});
            skLineSegment(sketch, "E17.10.0.55", {"start": v(-4.93, -18.44) * mm, "end": v(-8.56, -18.44) * mm});
            skLineSegment(sketch, "E17.10.0.56", {"start": v(-4.93, -8.57) * mm, "end": v(-4.93, -4.94) * mm});
            skLineSegment(sketch, "E17.10.0.57", {"start": v(-4.93, 18.43) * mm, "end": v(-8.56, 18.43) * mm});
            skLineSegment(sketch, "E17.10.0.58", {"start": v(-4.93, 35.56) * mm, "end": v(-8.56, 35.56) * mm});
            skLineSegment(sketch, "E17.10.0.59", {"start": v(-4.93, 4.93) * mm, "end": v(-4.93, 8.56) * mm});
            skLineSegment(sketch, "E17.10.0.60", {"start": v(-4.93, 27.43) * mm, "end": v(-8.56, 27.43) * mm});
            skLineSegment(sketch, "E17.10.0.61", {"start": v(-4.93, -8.57) * mm, "end": v(-8.56, -8.57) * mm});
            skLineSegment(sketch, "E17.10.0.62", {"start": v(-4.93, 8.56) * mm, "end": v(-8.56, 8.56) * mm});
            skLineSegment(sketch, "E17.10.0.63", {"start": v(-8.56, -17.57) * mm, "end": v(-8.56, -13.94) * mm});
            skLineSegment(sketch, "E17.10.0.64", {"start": v(-4.93, 22.93) * mm, "end": v(-8.56, 22.93) * mm});
            skLineSegment(sketch, "E17.10.0.65", {"start": v(-4.93, 22.93) * mm, "end": v(-4.93, 26.56) * mm});
            skLineSegment(sketch, "E17.11.0.0", {"start": v(-4.06, 27.43) * mm, "end": v(-4.06, 31.06) * mm});
            skLineSegment(sketch, "E17.11.0.1", {"start": v(-0.43, 27.43) * mm, "end": v(-0.43, 31.06) * mm});
            skLineSegment(sketch, "E17.11.0.2", {"start": v(-0.43, -13.07) * mm, "end": v(-0.43, -9.44) * mm});
            skLineSegment(sketch, "E17.11.0.3", {"start": v(-4.06, 9.43) * mm, "end": v(-4.06, 13.06) * mm});
            skLineSegment(sketch, "E17.11.0.4", {"start": v(-4.06, -13.07) * mm, "end": v(-4.06, -9.44) * mm});
            skLineSegment(sketch, "E17.11.0.5", {"start": v(-4.06, -31.07) * mm, "end": v(-4.06, -27.44) * mm});
            skPoint(sketch, "E17.11.0.6", {"position": v(-2.25, 33.75) * mm});
            skLineSegment(sketch, "E17.11.0.7", {"start": v(-0.43, 9.43) * mm, "end": v(-0.43, 13.06) * mm});
            skLineSegment(sketch, "E17.11.0.8", {"start": v(-0.43, -31.07) * mm, "end": v(-0.43, -27.44) * mm});
            skLineSegment(sketch, "E17.11.0.9", {"start": v(-0.43, 31.93) * mm, "end": v(-0.43, 27.43) * mm, "construction": true});
            skLineSegment(sketch, "E17.11.0.10", {"start": v(-0.43, 31.06) * mm, "end": v(-4.06, 31.06) * mm});
            skLineSegment(sketch, "E17.11.0.11", {"start": v(-0.43, 4.93) * mm, "end": v(-4.06, 4.93) * mm});
            skLineSegment(sketch, "E17.11.0.12", {"start": v(-0.43, -13.07) * mm, "end": v(-4.06, -13.07) * mm});
            skLineSegment(sketch, "E17.11.0.13", {"start": v(-0.43, -31.07) * mm, "end": v(-4.06, -31.07) * mm});
            skLineSegment(sketch, "E17.11.0.14", {"start": v(-4.06, 31.93) * mm, "end": v(-4.06, 35.56) * mm});
            skLineSegment(sketch, "E17.11.0.15", {"start": v(-0.43, 31.93) * mm, "end": v(-0.43, 35.56) * mm});
            skLineSegment(sketch, "E17.11.0.16", {"start": v(-0.43, 31.93) * mm, "end": v(-4.06, 31.93) * mm});
            skLineSegment(sketch, "E17.11.0.17", {"start": v(-4.06, 18.43) * mm, "end": v(-4.06, 22.06) * mm});
            skLineSegment(sketch, "E17.11.0.18", {"start": v(-0.43, 13.06) * mm, "end": v(-4.06, 13.06) * mm});
            skLineSegment(sketch, "E17.11.0.19", {"start": v(-0.43, -4.94) * mm, "end": v(-4.06, -4.94) * mm});
            skLineSegment(sketch, "E17.11.0.20", {"start": v(-0.43, -22.94) * mm, "end": v(-4.06, -22.94) * mm});
            skLineSegment(sketch, "E17.11.0.21", {"start": v(-0.43, -26.57) * mm, "end": v(-0.43, -22.94) * mm});
            skLineSegment(sketch, "E17.11.0.22", {"start": v(-4.06, -8.57) * mm, "end": v(-4.06, -4.94) * mm});
            skLineSegment(sketch, "E17.11.0.23", {"start": v(-4.06, -26.57) * mm, "end": v(-4.06, -22.94) * mm});
            skLineSegment(sketch, "E17.11.0.24", {"start": v(-0.43, 17.56) * mm, "end": v(-4.06, 17.56) * mm});
            skLineSegment(sketch, "E17.11.0.25", {"start": v(-0.43, -0.44) * mm, "end": v(-4.06, -0.44) * mm});
            skLineSegment(sketch, "E17.11.0.26", {"start": v(-0.43, -9.44) * mm, "end": v(-4.06, -9.44) * mm});
            skLineSegment(sketch, "E17.11.0.27", {"start": v(-4.06, -22.07) * mm, "end": v(-4.06, -18.44) * mm});
            skLineSegment(sketch, "E17.11.0.28", {"start": v(-4.06, 13.93) * mm, "end": v(-4.06, 17.56) * mm});
            skLineSegment(sketch, "E17.11.0.29", {"start": v(-4.06, -4.07) * mm, "end": v(-4.06, -0.44) * mm});
            skLineSegment(sketch, "E17.11.0.30", {"start": v(-0.43, 13.93) * mm, "end": v(-4.06, 13.93) * mm});
            skLineSegment(sketch, "E17.11.0.31", {"start": v(-0.43, -4.07) * mm, "end": v(-4.06, -4.07) * mm});
            skLineSegment(sketch, "E17.11.0.32", {"start": v(-0.43, -17.57) * mm, "end": v(-4.06, -17.57) * mm});
            skLineSegment(sketch, "E17.11.0.33", {"start": v(-0.43, -27.44) * mm, "end": v(-4.06, -27.44) * mm});
            skLineSegment(sketch, "E17.11.0.34", {"start": v(-0.43, -35.57) * mm, "end": v(-4.06, -35.57) * mm});
            skLineSegment(sketch, "E17.11.0.35", {"start": v(-0.43, 0.43) * mm, "end": v(-4.06, 0.43) * mm});
            skLineSegment(sketch, "E17.11.0.36", {"start": v(-0.43, 13.93) * mm, "end": v(-0.43, 17.56) * mm});
            skLineSegment(sketch, "E17.11.0.37", {"start": v(-0.43, -22.07) * mm, "end": v(-0.43, -18.44) * mm});
            skLineSegment(sketch, "E17.11.0.38", {"start": v(-0.43, -17.57) * mm, "end": v(-0.43, -13.94) * mm});
            skLineSegment(sketch, "E17.11.0.39", {"start": v(-4.06, 4.93) * mm, "end": v(-4.06, 8.56) * mm});
            skLineSegment(sketch, "E17.11.0.40", {"start": v(-0.43, 26.56) * mm, "end": v(-4.06, 26.56) * mm});
            skLineSegment(sketch, "E17.11.0.41", {"start": v(-0.43, 9.43) * mm, "end": v(-4.06, 9.43) * mm});
            skLineSegment(sketch, "E17.11.0.42", {"start": v(-4.06, 22.93) * mm, "end": v(-4.06, 26.56) * mm});
            skLineSegment(sketch, "E17.11.0.43", {"start": v(-0.43, -13.94) * mm, "end": v(-4.06, -13.94) * mm});
            skLineSegment(sketch, "E17.11.0.44", {"start": v(-0.43, -31.94) * mm, "end": v(-4.06, -31.94) * mm});
            skLineSegment(sketch, "E17.11.0.45", {"start": v(-0.43, 22.06) * mm, "end": v(-4.06, 22.06) * mm});
            skLineSegment(sketch, "E17.11.0.46", {"start": v(-0.43, 4.06) * mm, "end": v(-4.06, 4.06) * mm});
            skLineSegment(sketch, "E17.11.0.47", {"start": v(-4.06, 0.43) * mm, "end": v(-4.06, 4.06) * mm});
            skLineSegment(sketch, "E17.11.0.48", {"start": v(-4.06, -35.57) * mm, "end": v(-4.06, -31.94) * mm});
            skLineSegment(sketch, "E17.11.0.49", {"start": v(-0.43, 0.43) * mm, "end": v(-0.43, 4.06) * mm});
            skLineSegment(sketch, "E17.11.0.50", {"start": v(-0.43, -26.57) * mm, "end": v(-4.06, -26.57) * mm});
            skLineSegment(sketch, "E17.11.0.51", {"start": v(-0.43, -35.57) * mm, "end": v(-0.43, -31.94) * mm});
            skLineSegment(sketch, "E17.11.0.52", {"start": v(-0.43, -4.07) * mm, "end": v(-0.43, -0.44) * mm});
            skLineSegment(sketch, "E17.11.0.53", {"start": v(-0.43, -22.07) * mm, "end": v(-4.06, -22.07) * mm});
            skLineSegment(sketch, "E17.11.0.54", {"start": v(-0.43, 18.43) * mm, "end": v(-0.43, 22.06) * mm});
            skLineSegment(sketch, "E17.11.0.55", {"start": v(-0.43, -18.44) * mm, "end": v(-4.06, -18.44) * mm});
            skLineSegment(sketch, "E17.11.0.56", {"start": v(-0.43, -8.57) * mm, "end": v(-0.43, -4.94) * mm});
            skLineSegment(sketch, "E17.11.0.57", {"start": v(-0.43, 18.43) * mm, "end": v(-4.06, 18.43) * mm});
            skLineSegment(sketch, "E17.11.0.58", {"start": v(-0.43, 35.56) * mm, "end": v(-4.06, 35.56) * mm});
            skLineSegment(sketch, "E17.11.0.59", {"start": v(-0.43, 4.93) * mm, "end": v(-0.43, 8.56) * mm});
            skLineSegment(sketch, "E17.11.0.60", {"start": v(-0.43, 27.43) * mm, "end": v(-4.06, 27.43) * mm});
            skLineSegment(sketch, "E17.11.0.61", {"start": v(-0.43, -8.57) * mm, "end": v(-4.06, -8.57) * mm});
            skLineSegment(sketch, "E17.11.0.62", {"start": v(-0.43, 8.56) * mm, "end": v(-4.06, 8.56) * mm});
            skLineSegment(sketch, "E17.11.0.63", {"start": v(-4.06, -17.57) * mm, "end": v(-4.06, -13.94) * mm});
            skLineSegment(sketch, "E17.11.0.64", {"start": v(-0.43, 22.93) * mm, "end": v(-4.06, 22.93) * mm});
            skLineSegment(sketch, "E17.11.0.65", {"start": v(-0.43, 22.93) * mm, "end": v(-0.43, 26.56) * mm});
            skLineSegment(sketch, "E17.12.0.0", {"start": v(0.44, 27.43) * mm, "end": v(0.44, 31.06) * mm});
            skLineSegment(sketch, "E17.12.0.1", {"start": v(4.07, 27.43) * mm, "end": v(4.07, 31.06) * mm});
            skLineSegment(sketch, "E17.12.0.2", {"start": v(4.07, -13.07) * mm, "end": v(4.07, -9.44) * mm});
            skLineSegment(sketch, "E17.12.0.3", {"start": v(0.44, 9.43) * mm, "end": v(0.44, 13.06) * mm});
            skLineSegment(sketch, "E17.12.0.4", {"start": v(0.44, -13.07) * mm, "end": v(0.44, -9.44) * mm});
            skLineSegment(sketch, "E17.12.0.5", {"start": v(0.44, -31.07) * mm, "end": v(0.44, -27.44) * mm});
            skPoint(sketch, "E17.12.0.6", {"position": v(2.25, 33.75) * mm});
            skLineSegment(sketch, "E17.12.0.7", {"start": v(4.07, 9.43) * mm, "end": v(4.07, 13.06) * mm});
            skLineSegment(sketch, "E17.12.0.8", {"start": v(4.07, -31.07) * mm, "end": v(4.07, -27.44) * mm});
            skLineSegment(sketch, "E17.12.0.9", {"start": v(4.07, 31.93) * mm, "end": v(4.07, 27.43) * mm, "construction": true});
            skLineSegment(sketch, "E17.12.0.10", {"start": v(4.07, 31.06) * mm, "end": v(0.44, 31.06) * mm});
            skLineSegment(sketch, "E17.12.0.11", {"start": v(4.07, 4.93) * mm, "end": v(0.44, 4.93) * mm});
            skLineSegment(sketch, "E17.12.0.12", {"start": v(4.07, -13.07) * mm, "end": v(0.44, -13.07) * mm});
            skLineSegment(sketch, "E17.12.0.13", {"start": v(4.07, -31.07) * mm, "end": v(0.44, -31.07) * mm});
            skLineSegment(sketch, "E17.12.0.14", {"start": v(0.44, 31.93) * mm, "end": v(0.44, 35.56) * mm});
            skLineSegment(sketch, "E17.12.0.15", {"start": v(4.07, 31.93) * mm, "end": v(4.07, 35.56) * mm});
            skLineSegment(sketch, "E17.12.0.16", {"start": v(4.07, 31.93) * mm, "end": v(0.44, 31.93) * mm});
            skLineSegment(sketch, "E17.12.0.17", {"start": v(0.44, 18.43) * mm, "end": v(0.44, 22.06) * mm});
            skLineSegment(sketch, "E17.12.0.18", {"start": v(4.07, 13.06) * mm, "end": v(0.44, 13.06) * mm});
            skLineSegment(sketch, "E17.12.0.19", {"start": v(4.07, -4.94) * mm, "end": v(0.44, -4.94) * mm});
            skLineSegment(sketch, "E17.12.0.20", {"start": v(4.07, -22.94) * mm, "end": v(0.44, -22.94) * mm});
            skLineSegment(sketch, "E17.12.0.21", {"start": v(4.07, -26.57) * mm, "end": v(4.07, -22.94) * mm});
            skLineSegment(sketch, "E17.12.0.22", {"start": v(0.44, -8.57) * mm, "end": v(0.44, -4.94) * mm});
            skLineSegment(sketch, "E17.12.0.23", {"start": v(0.44, -26.57) * mm, "end": v(0.44, -22.94) * mm});
            skLineSegment(sketch, "E17.12.0.24", {"start": v(4.07, 17.56) * mm, "end": v(0.44, 17.56) * mm});
            skLineSegment(sketch, "E17.12.0.25", {"start": v(4.07, -0.44) * mm, "end": v(0.44, -0.44) * mm});
            skLineSegment(sketch, "E17.12.0.26", {"start": v(4.07, -9.44) * mm, "end": v(0.44, -9.44) * mm});
            skLineSegment(sketch, "E17.12.0.27", {"start": v(0.44, -22.07) * mm, "end": v(0.44, -18.44) * mm});
            skLineSegment(sketch, "E17.12.0.28", {"start": v(0.44, 13.93) * mm, "end": v(0.44, 17.56) * mm});
            skLineSegment(sketch, "E17.12.0.29", {"start": v(0.44, -4.07) * mm, "end": v(0.44, -0.44) * mm});
            skLineSegment(sketch, "E17.12.0.30", {"start": v(4.07, 13.93) * mm, "end": v(0.44, 13.93) * mm});
            skLineSegment(sketch, "E17.12.0.31", {"start": v(4.07, -4.07) * mm, "end": v(0.44, -4.07) * mm});
            skLineSegment(sketch, "E17.12.0.32", {"start": v(4.07, -17.57) * mm, "end": v(0.44, -17.57) * mm});
            skLineSegment(sketch, "E17.12.0.33", {"start": v(4.07, -27.44) * mm, "end": v(0.44, -27.44) * mm});
            skLineSegment(sketch, "E17.12.0.34", {"start": v(4.07, -35.57) * mm, "end": v(0.44, -35.57) * mm});
            skLineSegment(sketch, "E17.12.0.35", {"start": v(4.07, 0.43) * mm, "end": v(0.44, 0.43) * mm});
            skLineSegment(sketch, "E17.12.0.36", {"start": v(4.07, 13.93) * mm, "end": v(4.07, 17.56) * mm});
            skLineSegment(sketch, "E17.12.0.37", {"start": v(4.07, -22.07) * mm, "end": v(4.07, -18.44) * mm});
            skLineSegment(sketch, "E17.12.0.38", {"start": v(4.07, -17.57) * mm, "end": v(4.07, -13.94) * mm});
            skLineSegment(sketch, "E17.12.0.39", {"start": v(0.44, 4.93) * mm, "end": v(0.44, 8.56) * mm});
            skLineSegment(sketch, "E17.12.0.40", {"start": v(4.07, 26.56) * mm, "end": v(0.44, 26.56) * mm});
            skLineSegment(sketch, "E17.12.0.41", {"start": v(4.07, 9.43) * mm, "end": v(0.44, 9.43) * mm});
            skLineSegment(sketch, "E17.12.0.42", {"start": v(0.44, 22.93) * mm, "end": v(0.44, 26.56) * mm});
            skLineSegment(sketch, "E17.12.0.43", {"start": v(4.07, -13.94) * mm, "end": v(0.44, -13.94) * mm});
            skLineSegment(sketch, "E17.12.0.44", {"start": v(4.07, -31.94) * mm, "end": v(0.44, -31.94) * mm});
            skLineSegment(sketch, "E17.12.0.45", {"start": v(4.07, 22.06) * mm, "end": v(0.44, 22.06) * mm});
            skLineSegment(sketch, "E17.12.0.46", {"start": v(4.07, 4.06) * mm, "end": v(0.44, 4.06) * mm});
            skLineSegment(sketch, "E17.12.0.47", {"start": v(0.44, 0.43) * mm, "end": v(0.44, 4.06) * mm});
            skLineSegment(sketch, "E17.12.0.48", {"start": v(0.44, -35.57) * mm, "end": v(0.44, -31.94) * mm});
            skLineSegment(sketch, "E17.12.0.49", {"start": v(4.07, 0.43) * mm, "end": v(4.07, 4.06) * mm});
            skLineSegment(sketch, "E17.12.0.50", {"start": v(4.07, -26.57) * mm, "end": v(0.44, -26.57) * mm});
            skLineSegment(sketch, "E17.12.0.51", {"start": v(4.07, -35.57) * mm, "end": v(4.07, -31.94) * mm});
            skLineSegment(sketch, "E17.12.0.52", {"start": v(4.07, -4.07) * mm, "end": v(4.07, -0.44) * mm});
            skLineSegment(sketch, "E17.12.0.53", {"start": v(4.07, -22.07) * mm, "end": v(0.44, -22.07) * mm});
            skLineSegment(sketch, "E17.12.0.54", {"start": v(4.07, 18.43) * mm, "end": v(4.07, 22.06) * mm});
            skLineSegment(sketch, "E17.12.0.55", {"start": v(4.07, -18.44) * mm, "end": v(0.44, -18.44) * mm});
            skLineSegment(sketch, "E17.12.0.56", {"start": v(4.07, -8.57) * mm, "end": v(4.07, -4.94) * mm});
            skLineSegment(sketch, "E17.12.0.57", {"start": v(4.07, 18.43) * mm, "end": v(0.44, 18.43) * mm});
            skLineSegment(sketch, "E17.12.0.58", {"start": v(4.07, 35.56) * mm, "end": v(0.44, 35.56) * mm});
            skLineSegment(sketch, "E17.12.0.59", {"start": v(4.07, 4.93) * mm, "end": v(4.07, 8.56) * mm});
            skLineSegment(sketch, "E17.12.0.60", {"start": v(4.07, 27.43) * mm, "end": v(0.44, 27.43) * mm});
            skLineSegment(sketch, "E17.12.0.61", {"start": v(4.07, -8.57) * mm, "end": v(0.44, -8.57) * mm});
            skLineSegment(sketch, "E17.12.0.62", {"start": v(4.07, 8.56) * mm, "end": v(0.44, 8.56) * mm});
            skLineSegment(sketch, "E17.12.0.63", {"start": v(0.44, -17.57) * mm, "end": v(0.44, -13.94) * mm});
            skLineSegment(sketch, "E17.12.0.64", {"start": v(4.07, 22.93) * mm, "end": v(0.44, 22.93) * mm});
            skLineSegment(sketch, "E17.12.0.65", {"start": v(4.07, 22.93) * mm, "end": v(4.07, 26.56) * mm});
            skLineSegment(sketch, "E17.13.0.0", {"start": v(4.94, 27.43) * mm, "end": v(4.94, 31.06) * mm});
            skLineSegment(sketch, "E17.13.0.1", {"start": v(8.57, 27.43) * mm, "end": v(8.57, 31.06) * mm});
            skLineSegment(sketch, "E17.13.0.2", {"start": v(8.57, -13.07) * mm, "end": v(8.57, -9.44) * mm});
            skLineSegment(sketch, "E17.13.0.3", {"start": v(4.94, 9.43) * mm, "end": v(4.94, 13.06) * mm});
            skLineSegment(sketch, "E17.13.0.4", {"start": v(4.94, -13.07) * mm, "end": v(4.94, -9.44) * mm});
            skLineSegment(sketch, "E17.13.0.5", {"start": v(4.94, -31.07) * mm, "end": v(4.94, -27.44) * mm});
            skPoint(sketch, "E17.13.0.6", {"position": v(6.75, 33.75) * mm});
            skLineSegment(sketch, "E17.13.0.7", {"start": v(8.57, 9.43) * mm, "end": v(8.57, 13.06) * mm});
            skLineSegment(sketch, "E17.13.0.8", {"start": v(8.57, -31.07) * mm, "end": v(8.57, -27.44) * mm});
            skLineSegment(sketch, "E17.13.0.9", {"start": v(8.57, 31.93) * mm, "end": v(8.57, 27.43) * mm, "construction": true});
            skLineSegment(sketch, "E17.13.0.10", {"start": v(8.57, 31.06) * mm, "end": v(4.94, 31.06) * mm});
            skLineSegment(sketch, "E17.13.0.11", {"start": v(8.57, 4.93) * mm, "end": v(4.94, 4.93) * mm});
            skLineSegment(sketch, "E17.13.0.12", {"start": v(8.57, -13.07) * mm, "end": v(4.94, -13.07) * mm});
            skLineSegment(sketch, "E17.13.0.13", {"start": v(8.57, -31.07) * mm, "end": v(4.94, -31.07) * mm});
            skLineSegment(sketch, "E17.13.0.14", {"start": v(4.94, 31.93) * mm, "end": v(4.94, 35.56) * mm});
            skLineSegment(sketch, "E17.13.0.15", {"start": v(8.57, 31.93) * mm, "end": v(8.57, 35.56) * mm});
            skLineSegment(sketch, "E17.13.0.16", {"start": v(8.57, 31.93) * mm, "end": v(4.94, 31.93) * mm});
            skLineSegment(sketch, "E17.13.0.17", {"start": v(4.94, 18.43) * mm, "end": v(4.94, 22.06) * mm});
            skLineSegment(sketch, "E17.13.0.18", {"start": v(8.57, 13.06) * mm, "end": v(4.94, 13.06) * mm});
            skLineSegment(sketch, "E17.13.0.19", {"start": v(8.57, -4.94) * mm, "end": v(4.94, -4.94) * mm});
            skLineSegment(sketch, "E17.13.0.20", {"start": v(8.57, -22.94) * mm, "end": v(4.94, -22.94) * mm});
            skLineSegment(sketch, "E17.13.0.21", {"start": v(8.57, -26.57) * mm, "end": v(8.57, -22.94) * mm});
            skLineSegment(sketch, "E17.13.0.22", {"start": v(4.94, -8.57) * mm, "end": v(4.94, -4.94) * mm});
            skLineSegment(sketch, "E17.13.0.23", {"start": v(4.94, -26.57) * mm, "end": v(4.94, -22.94) * mm});
            skLineSegment(sketch, "E17.13.0.24", {"start": v(8.57, 17.56) * mm, "end": v(4.94, 17.56) * mm});
            skLineSegment(sketch, "E17.13.0.25", {"start": v(8.57, -0.44) * mm, "end": v(4.94, -0.44) * mm});
            skLineSegment(sketch, "E17.13.0.26", {"start": v(8.57, -9.44) * mm, "end": v(4.94, -9.44) * mm});
            skLineSegment(sketch, "E17.13.0.27", {"start": v(4.94, -22.07) * mm, "end": v(4.94, -18.44) * mm});
            skLineSegment(sketch, "E17.13.0.28", {"start": v(4.94, 13.93) * mm, "end": v(4.94, 17.56) * mm});
            skLineSegment(sketch, "E17.13.0.29", {"start": v(4.94, -4.07) * mm, "end": v(4.94, -0.44) * mm});
            skLineSegment(sketch, "E17.13.0.30", {"start": v(8.57, 13.93) * mm, "end": v(4.94, 13.93) * mm});
            skLineSegment(sketch, "E17.13.0.31", {"start": v(8.57, -4.07) * mm, "end": v(4.94, -4.07) * mm});
            skLineSegment(sketch, "E17.13.0.32", {"start": v(8.57, -17.57) * mm, "end": v(4.94, -17.57) * mm});
            skLineSegment(sketch, "E17.13.0.33", {"start": v(8.57, -27.44) * mm, "end": v(4.94, -27.44) * mm});
            skLineSegment(sketch, "E17.13.0.34", {"start": v(8.57, -35.57) * mm, "end": v(4.94, -35.57) * mm});
            skLineSegment(sketch, "E17.13.0.35", {"start": v(8.57, 0.43) * mm, "end": v(4.94, 0.43) * mm});
            skLineSegment(sketch, "E17.13.0.36", {"start": v(8.57, 13.93) * mm, "end": v(8.57, 17.56) * mm});
            skLineSegment(sketch, "E17.13.0.37", {"start": v(8.57, -22.07) * mm, "end": v(8.57, -18.44) * mm});
            skLineSegment(sketch, "E17.13.0.38", {"start": v(8.57, -17.57) * mm, "end": v(8.57, -13.94) * mm});
            skLineSegment(sketch, "E17.13.0.39", {"start": v(4.94, 4.93) * mm, "end": v(4.94, 8.56) * mm});
            skLineSegment(sketch, "E17.13.0.40", {"start": v(8.57, 26.56) * mm, "end": v(4.94, 26.56) * mm});
            skLineSegment(sketch, "E17.13.0.41", {"start": v(8.57, 9.43) * mm, "end": v(4.94, 9.43) * mm});
            skLineSegment(sketch, "E17.13.0.42", {"start": v(4.94, 22.93) * mm, "end": v(4.94, 26.56) * mm});
            skLineSegment(sketch, "E17.13.0.43", {"start": v(8.57, -13.94) * mm, "end": v(4.94, -13.94) * mm});
            skLineSegment(sketch, "E17.13.0.44", {"start": v(8.57, -31.94) * mm, "end": v(4.94, -31.94) * mm});
            skLineSegment(sketch, "E17.13.0.45", {"start": v(8.57, 22.06) * mm, "end": v(4.94, 22.06) * mm});
            skLineSegment(sketch, "E17.13.0.46", {"start": v(8.57, 4.06) * mm, "end": v(4.94, 4.06) * mm});
            skLineSegment(sketch, "E17.13.0.47", {"start": v(4.94, 0.43) * mm, "end": v(4.94, 4.06) * mm});
            skLineSegment(sketch, "E17.13.0.48", {"start": v(4.94, -35.57) * mm, "end": v(4.94, -31.94) * mm});
            skLineSegment(sketch, "E17.13.0.49", {"start": v(8.57, 0.43) * mm, "end": v(8.57, 4.06) * mm});
            skLineSegment(sketch, "E17.13.0.50", {"start": v(8.57, -26.57) * mm, "end": v(4.94, -26.57) * mm});
            skLineSegment(sketch, "E17.13.0.51", {"start": v(8.57, -35.57) * mm, "end": v(8.57, -31.94) * mm});
            skLineSegment(sketch, "E17.13.0.52", {"start": v(8.57, -4.07) * mm, "end": v(8.57, -0.44) * mm});
            skLineSegment(sketch, "E17.13.0.53", {"start": v(8.57, -22.07) * mm, "end": v(4.94, -22.07) * mm});
            skLineSegment(sketch, "E17.13.0.54", {"start": v(8.57, 18.43) * mm, "end": v(8.57, 22.06) * mm});
            skLineSegment(sketch, "E17.13.0.55", {"start": v(8.57, -18.44) * mm, "end": v(4.94, -18.44) * mm});
            skLineSegment(sketch, "E17.13.0.56", {"start": v(8.57, -8.57) * mm, "end": v(8.57, -4.94) * mm});
            skLineSegment(sketch, "E17.13.0.57", {"start": v(8.57, 18.43) * mm, "end": v(4.94, 18.43) * mm});
            skLineSegment(sketch, "E17.13.0.58", {"start": v(8.57, 35.56) * mm, "end": v(4.94, 35.56) * mm});
            skLineSegment(sketch, "E17.13.0.59", {"start": v(8.57, 4.93) * mm, "end": v(8.57, 8.56) * mm});
            skLineSegment(sketch, "E17.13.0.60", {"start": v(8.57, 27.43) * mm, "end": v(4.94, 27.43) * mm});
            skLineSegment(sketch, "E17.13.0.61", {"start": v(8.57, -8.57) * mm, "end": v(4.94, -8.57) * mm});
            skLineSegment(sketch, "E17.13.0.62", {"start": v(8.57, 8.56) * mm, "end": v(4.94, 8.56) * mm});
            skLineSegment(sketch, "E17.13.0.63", {"start": v(4.94, -17.57) * mm, "end": v(4.94, -13.94) * mm});
            skLineSegment(sketch, "E17.13.0.64", {"start": v(8.57, 22.93) * mm, "end": v(4.94, 22.93) * mm});
            skLineSegment(sketch, "E17.13.0.65", {"start": v(8.57, 22.93) * mm, "end": v(8.57, 26.56) * mm});
            skLineSegment(sketch, "E17.14.0.0", {"start": v(9.44, 27.43) * mm, "end": v(9.44, 31.06) * mm});
            skLineSegment(sketch, "E17.14.0.1", {"start": v(13.07, 27.43) * mm, "end": v(13.07, 31.06) * mm});
            skLineSegment(sketch, "E17.14.0.2", {"start": v(13.07, -13.07) * mm, "end": v(13.07, -9.44) * mm});
            skLineSegment(sketch, "E17.14.0.3", {"start": v(9.44, 9.43) * mm, "end": v(9.44, 13.06) * mm});
            skLineSegment(sketch, "E17.14.0.4", {"start": v(9.44, -13.07) * mm, "end": v(9.44, -9.44) * mm});
            skLineSegment(sketch, "E17.14.0.5", {"start": v(9.44, -31.07) * mm, "end": v(9.44, -27.44) * mm});
            skPoint(sketch, "E17.14.0.6", {"position": v(11.25, 33.75) * mm});
            skLineSegment(sketch, "E17.14.0.7", {"start": v(13.07, 9.43) * mm, "end": v(13.07, 13.06) * mm});
            skLineSegment(sketch, "E17.14.0.8", {"start": v(13.07, -31.07) * mm, "end": v(13.07, -27.44) * mm});
            skLineSegment(sketch, "E17.14.0.9", {"start": v(13.07, 31.93) * mm, "end": v(13.07, 27.43) * mm, "construction": true});
            skLineSegment(sketch, "E17.14.0.10", {"start": v(13.07, 31.06) * mm, "end": v(9.44, 31.06) * mm});
            skLineSegment(sketch, "E17.14.0.11", {"start": v(13.07, 4.93) * mm, "end": v(9.44, 4.93) * mm});
            skLineSegment(sketch, "E17.14.0.12", {"start": v(13.07, -13.07) * mm, "end": v(9.44, -13.07) * mm});
            skLineSegment(sketch, "E17.14.0.13", {"start": v(13.07, -31.07) * mm, "end": v(9.44, -31.07) * mm});
            skLineSegment(sketch, "E17.14.0.14", {"start": v(9.44, 31.93) * mm, "end": v(9.44, 35.56) * mm});
            skLineSegment(sketch, "E17.14.0.15", {"start": v(13.07, 31.93) * mm, "end": v(13.07, 35.56) * mm});
            skLineSegment(sketch, "E17.14.0.16", {"start": v(13.07, 31.93) * mm, "end": v(9.44, 31.93) * mm});
            skLineSegment(sketch, "E17.14.0.17", {"start": v(9.44, 18.43) * mm, "end": v(9.44, 22.06) * mm});
            skLineSegment(sketch, "E17.14.0.18", {"start": v(13.07, 13.06) * mm, "end": v(9.44, 13.06) * mm});
            skLineSegment(sketch, "E17.14.0.19", {"start": v(13.07, -4.94) * mm, "end": v(9.44, -4.94) * mm});
            skLineSegment(sketch, "E17.14.0.20", {"start": v(13.07, -22.94) * mm, "end": v(9.44, -22.94) * mm});
            skLineSegment(sketch, "E17.14.0.21", {"start": v(13.07, -26.57) * mm, "end": v(13.07, -22.94) * mm});
            skLineSegment(sketch, "E17.14.0.22", {"start": v(9.44, -8.57) * mm, "end": v(9.44, -4.94) * mm});
            skLineSegment(sketch, "E17.14.0.23", {"start": v(9.44, -26.57) * mm, "end": v(9.44, -22.94) * mm});
            skLineSegment(sketch, "E17.14.0.24", {"start": v(13.07, 17.56) * mm, "end": v(9.44, 17.56) * mm});
            skLineSegment(sketch, "E17.14.0.25", {"start": v(13.07, -0.44) * mm, "end": v(9.44, -0.44) * mm});
            skLineSegment(sketch, "E17.14.0.26", {"start": v(13.07, -9.44) * mm, "end": v(9.44, -9.44) * mm});
            skLineSegment(sketch, "E17.14.0.27", {"start": v(9.44, -22.07) * mm, "end": v(9.44, -18.44) * mm});
            skLineSegment(sketch, "E17.14.0.28", {"start": v(9.44, 13.93) * mm, "end": v(9.44, 17.56) * mm});
            skLineSegment(sketch, "E17.14.0.29", {"start": v(9.44, -4.07) * mm, "end": v(9.44, -0.44) * mm});
            skLineSegment(sketch, "E17.14.0.30", {"start": v(13.07, 13.93) * mm, "end": v(9.44, 13.93) * mm});
            skLineSegment(sketch, "E17.14.0.31", {"start": v(13.07, -4.07) * mm, "end": v(9.44, -4.07) * mm});
            skLineSegment(sketch, "E17.14.0.32", {"start": v(13.07, -17.57) * mm, "end": v(9.44, -17.57) * mm});
            skLineSegment(sketch, "E17.14.0.33", {"start": v(13.07, -27.44) * mm, "end": v(9.44, -27.44) * mm});
            skLineSegment(sketch, "E17.14.0.34", {"start": v(13.07, -35.57) * mm, "end": v(9.44, -35.57) * mm});
            skLineSegment(sketch, "E17.14.0.35", {"start": v(13.07, 0.43) * mm, "end": v(9.44, 0.43) * mm});
            skLineSegment(sketch, "E17.14.0.36", {"start": v(13.07, 13.93) * mm, "end": v(13.07, 17.56) * mm});
            skLineSegment(sketch, "E17.14.0.37", {"start": v(13.07, -22.07) * mm, "end": v(13.07, -18.44) * mm});
            skLineSegment(sketch, "E17.14.0.38", {"start": v(13.07, -17.57) * mm, "end": v(13.07, -13.94) * mm});
            skLineSegment(sketch, "E17.14.0.39", {"start": v(9.44, 4.93) * mm, "end": v(9.44, 8.56) * mm});
            skLineSegment(sketch, "E17.14.0.40", {"start": v(13.07, 26.56) * mm, "end": v(9.44, 26.56) * mm});
            skLineSegment(sketch, "E17.14.0.41", {"start": v(13.07, 9.43) * mm, "end": v(9.44, 9.43) * mm});
            skLineSegment(sketch, "E17.14.0.42", {"start": v(9.44, 22.93) * mm, "end": v(9.44, 26.56) * mm});
            skLineSegment(sketch, "E17.14.0.43", {"start": v(13.07, -13.94) * mm, "end": v(9.44, -13.94) * mm});
            skLineSegment(sketch, "E17.14.0.44", {"start": v(13.07, -31.94) * mm, "end": v(9.44, -31.94) * mm});
            skLineSegment(sketch, "E17.14.0.45", {"start": v(13.07, 22.06) * mm, "end": v(9.44, 22.06) * mm});
            skLineSegment(sketch, "E17.14.0.46", {"start": v(13.07, 4.06) * mm, "end": v(9.44, 4.06) * mm});
            skLineSegment(sketch, "E17.14.0.47", {"start": v(9.44, 0.43) * mm, "end": v(9.44, 4.06) * mm});
            skLineSegment(sketch, "E17.14.0.48", {"start": v(9.44, -35.57) * mm, "end": v(9.44, -31.94) * mm});
            skLineSegment(sketch, "E17.14.0.49", {"start": v(13.07, 0.43) * mm, "end": v(13.07, 4.06) * mm});
            skLineSegment(sketch, "E17.14.0.50", {"start": v(13.07, -26.57) * mm, "end": v(9.44, -26.57) * mm});
            skLineSegment(sketch, "E17.14.0.51", {"start": v(13.07, -35.57) * mm, "end": v(13.07, -31.94) * mm});
            skLineSegment(sketch, "E17.14.0.52", {"start": v(13.07, -4.07) * mm, "end": v(13.07, -0.44) * mm});
            skLineSegment(sketch, "E17.14.0.53", {"start": v(13.07, -22.07) * mm, "end": v(9.44, -22.07) * mm});
            skLineSegment(sketch, "E17.14.0.54", {"start": v(13.07, 18.43) * mm, "end": v(13.07, 22.06) * mm});
            skLineSegment(sketch, "E17.14.0.55", {"start": v(13.07, -18.44) * mm, "end": v(9.44, -18.44) * mm});
            skLineSegment(sketch, "E17.14.0.56", {"start": v(13.07, -8.57) * mm, "end": v(13.07, -4.94) * mm});
            skLineSegment(sketch, "E17.14.0.57", {"start": v(13.07, 18.43) * mm, "end": v(9.44, 18.43) * mm});
            skLineSegment(sketch, "E17.14.0.58", {"start": v(13.07, 35.56) * mm, "end": v(9.44, 35.56) * mm});
            skLineSegment(sketch, "E17.14.0.59", {"start": v(13.07, 4.93) * mm, "end": v(13.07, 8.56) * mm});
            skLineSegment(sketch, "E17.14.0.60", {"start": v(13.07, 27.43) * mm, "end": v(9.44, 27.43) * mm});
            skLineSegment(sketch, "E17.14.0.61", {"start": v(13.07, -8.57) * mm, "end": v(9.44, -8.57) * mm});
            skLineSegment(sketch, "E17.14.0.62", {"start": v(13.07, 8.56) * mm, "end": v(9.44, 8.56) * mm});
            skLineSegment(sketch, "E17.14.0.63", {"start": v(9.44, -17.57) * mm, "end": v(9.44, -13.94) * mm});
            skLineSegment(sketch, "E17.14.0.64", {"start": v(13.07, 22.93) * mm, "end": v(9.44, 22.93) * mm});
            skLineSegment(sketch, "E17.14.0.65", {"start": v(13.07, 22.93) * mm, "end": v(13.07, 26.56) * mm});
            skLineSegment(sketch, "E17.15.0.0", {"start": v(13.94, 27.43) * mm, "end": v(13.94, 31.06) * mm});
            skLineSegment(sketch, "E17.15.0.1", {"start": v(17.57, 27.43) * mm, "end": v(17.57, 31.06) * mm});
            skLineSegment(sketch, "E17.15.0.2", {"start": v(17.57, -13.07) * mm, "end": v(17.57, -9.44) * mm});
            skLineSegment(sketch, "E17.15.0.3", {"start": v(13.94, 9.43) * mm, "end": v(13.94, 13.06) * mm});
            skLineSegment(sketch, "E17.15.0.4", {"start": v(13.94, -13.07) * mm, "end": v(13.94, -9.44) * mm});
            skLineSegment(sketch, "E17.15.0.5", {"start": v(13.94, -31.07) * mm, "end": v(13.94, -27.44) * mm});
            skPoint(sketch, "E17.15.0.6", {"position": v(15.75, 33.75) * mm});
            skLineSegment(sketch, "E17.15.0.7", {"start": v(17.57, 9.43) * mm, "end": v(17.57, 13.06) * mm});
            skLineSegment(sketch, "E17.15.0.8", {"start": v(17.57, -31.07) * mm, "end": v(17.57, -27.44) * mm});
            skLineSegment(sketch, "E17.15.0.9", {"start": v(17.57, 31.93) * mm, "end": v(17.57, 27.43) * mm, "construction": true});
            skLineSegment(sketch, "E17.15.0.10", {"start": v(17.57, 31.06) * mm, "end": v(13.94, 31.06) * mm});
            skLineSegment(sketch, "E17.15.0.11", {"start": v(17.57, 4.93) * mm, "end": v(13.94, 4.93) * mm});
            skLineSegment(sketch, "E17.15.0.12", {"start": v(17.57, -13.07) * mm, "end": v(13.94, -13.07) * mm});
            skLineSegment(sketch, "E17.15.0.13", {"start": v(17.57, -31.07) * mm, "end": v(13.94, -31.07) * mm});
            skLineSegment(sketch, "E17.15.0.14", {"start": v(13.94, 31.93) * mm, "end": v(13.94, 35.56) * mm});
            skLineSegment(sketch, "E17.15.0.15", {"start": v(17.57, 31.93) * mm, "end": v(17.57, 35.56) * mm});
            skLineSegment(sketch, "E17.15.0.16", {"start": v(17.57, 31.93) * mm, "end": v(13.94, 31.93) * mm});
            skLineSegment(sketch, "E17.15.0.17", {"start": v(13.94, 18.43) * mm, "end": v(13.94, 22.06) * mm});
            skLineSegment(sketch, "E17.15.0.18", {"start": v(17.57, 13.06) * mm, "end": v(13.94, 13.06) * mm});
            skLineSegment(sketch, "E17.15.0.19", {"start": v(17.57, -4.94) * mm, "end": v(13.94, -4.94) * mm});
            skLineSegment(sketch, "E17.15.0.20", {"start": v(17.57, -22.94) * mm, "end": v(13.94, -22.94) * mm});
            skLineSegment(sketch, "E17.15.0.21", {"start": v(17.57, -26.57) * mm, "end": v(17.57, -22.94) * mm});
            skLineSegment(sketch, "E17.15.0.22", {"start": v(13.94, -8.57) * mm, "end": v(13.94, -4.94) * mm});
            skLineSegment(sketch, "E17.15.0.23", {"start": v(13.94, -26.57) * mm, "end": v(13.94, -22.94) * mm});
            skLineSegment(sketch, "E17.15.0.24", {"start": v(17.57, 17.56) * mm, "end": v(13.94, 17.56) * mm});
            skLineSegment(sketch, "E17.15.0.25", {"start": v(17.57, -0.44) * mm, "end": v(13.94, -0.44) * mm});
            skLineSegment(sketch, "E17.15.0.26", {"start": v(17.57, -9.44) * mm, "end": v(13.94, -9.44) * mm});
            skLineSegment(sketch, "E17.15.0.27", {"start": v(13.94, -22.07) * mm, "end": v(13.94, -18.44) * mm});
            skLineSegment(sketch, "E17.15.0.28", {"start": v(13.94, 13.93) * mm, "end": v(13.94, 17.56) * mm});
            skLineSegment(sketch, "E17.15.0.29", {"start": v(13.94, -4.07) * mm, "end": v(13.94, -0.44) * mm});
            skLineSegment(sketch, "E17.15.0.30", {"start": v(17.57, 13.93) * mm, "end": v(13.94, 13.93) * mm});
            skLineSegment(sketch, "E17.15.0.31", {"start": v(17.57, -4.07) * mm, "end": v(13.94, -4.07) * mm});
            skLineSegment(sketch, "E17.15.0.32", {"start": v(17.57, -17.57) * mm, "end": v(13.94, -17.57) * mm});
            skLineSegment(sketch, "E17.15.0.33", {"start": v(17.57, -27.44) * mm, "end": v(13.94, -27.44) * mm});
            skLineSegment(sketch, "E17.15.0.34", {"start": v(17.57, -35.57) * mm, "end": v(13.94, -35.57) * mm});
            skLineSegment(sketch, "E17.15.0.35", {"start": v(17.57, 0.43) * mm, "end": v(13.94, 0.43) * mm});
            skLineSegment(sketch, "E17.15.0.36", {"start": v(17.57, 13.93) * mm, "end": v(17.57, 17.56) * mm});
            skLineSegment(sketch, "E17.15.0.37", {"start": v(17.57, -22.07) * mm, "end": v(17.57, -18.44) * mm});
            skLineSegment(sketch, "E17.15.0.38", {"start": v(17.57, -17.57) * mm, "end": v(17.57, -13.94) * mm});
            skLineSegment(sketch, "E17.15.0.39", {"start": v(13.94, 4.93) * mm, "end": v(13.94, 8.56) * mm});
            skLineSegment(sketch, "E17.15.0.40", {"start": v(17.57, 26.56) * mm, "end": v(13.94, 26.56) * mm});
            skLineSegment(sketch, "E17.15.0.41", {"start": v(17.57, 9.43) * mm, "end": v(13.94, 9.43) * mm});
            skLineSegment(sketch, "E17.15.0.42", {"start": v(13.94, 22.93) * mm, "end": v(13.94, 26.56) * mm});
            skLineSegment(sketch, "E17.15.0.43", {"start": v(17.57, -13.94) * mm, "end": v(13.94, -13.94) * mm});
            skLineSegment(sketch, "E17.15.0.44", {"start": v(17.57, -31.94) * mm, "end": v(13.94, -31.94) * mm});
            skLineSegment(sketch, "E17.15.0.45", {"start": v(17.57, 22.06) * mm, "end": v(13.94, 22.06) * mm});
            skLineSegment(sketch, "E17.15.0.46", {"start": v(17.57, 4.06) * mm, "end": v(13.94, 4.06) * mm});
            skLineSegment(sketch, "E17.15.0.47", {"start": v(13.94, 0.43) * mm, "end": v(13.94, 4.06) * mm});
            skLineSegment(sketch, "E17.15.0.48", {"start": v(13.94, -35.57) * mm, "end": v(13.94, -31.94) * mm});
            skLineSegment(sketch, "E17.15.0.49", {"start": v(17.57, 0.43) * mm, "end": v(17.57, 4.06) * mm});
            skLineSegment(sketch, "E17.15.0.50", {"start": v(17.57, -26.57) * mm, "end": v(13.94, -26.57) * mm});
            skLineSegment(sketch, "E17.15.0.51", {"start": v(17.57, -35.57) * mm, "end": v(17.57, -31.94) * mm});
            skLineSegment(sketch, "E17.15.0.52", {"start": v(17.57, -4.07) * mm, "end": v(17.57, -0.44) * mm});
            skLineSegment(sketch, "E17.15.0.53", {"start": v(17.57, -22.07) * mm, "end": v(13.94, -22.07) * mm});
            skLineSegment(sketch, "E17.15.0.54", {"start": v(17.57, 18.43) * mm, "end": v(17.57, 22.06) * mm});
            skLineSegment(sketch, "E17.15.0.55", {"start": v(17.57, -18.44) * mm, "end": v(13.94, -18.44) * mm});
            skLineSegment(sketch, "E17.15.0.56", {"start": v(17.57, -8.57) * mm, "end": v(17.57, -4.94) * mm});
            skLineSegment(sketch, "E17.15.0.57", {"start": v(17.57, 18.43) * mm, "end": v(13.94, 18.43) * mm});
            skLineSegment(sketch, "E17.15.0.58", {"start": v(17.57, 35.56) * mm, "end": v(13.94, 35.56) * mm});
            skLineSegment(sketch, "E17.15.0.59", {"start": v(17.57, 4.93) * mm, "end": v(17.57, 8.56) * mm});
            skLineSegment(sketch, "E17.15.0.60", {"start": v(17.57, 27.43) * mm, "end": v(13.94, 27.43) * mm});
            skLineSegment(sketch, "E17.15.0.61", {"start": v(17.57, -8.57) * mm, "end": v(13.94, -8.57) * mm});
            skLineSegment(sketch, "E17.15.0.62", {"start": v(17.57, 8.56) * mm, "end": v(13.94, 8.56) * mm});
            skLineSegment(sketch, "E17.15.0.63", {"start": v(13.94, -17.57) * mm, "end": v(13.94, -13.94) * mm});
            skLineSegment(sketch, "E17.15.0.64", {"start": v(17.57, 22.93) * mm, "end": v(13.94, 22.93) * mm});
            skLineSegment(sketch, "E17.15.0.65", {"start": v(17.57, 22.93) * mm, "end": v(17.57, 26.56) * mm});
            skLineSegment(sketch, "E17.16.0.0", {"start": v(18.44, 27.43) * mm, "end": v(18.44, 31.06) * mm});
            skLineSegment(sketch, "E17.16.0.1", {"start": v(22.07, 27.43) * mm, "end": v(22.07, 31.06) * mm});
            skLineSegment(sketch, "E17.16.0.2", {"start": v(22.07, -13.07) * mm, "end": v(22.07, -9.44) * mm});
            skLineSegment(sketch, "E17.16.0.3", {"start": v(18.44, 9.43) * mm, "end": v(18.44, 13.06) * mm});
            skLineSegment(sketch, "E17.16.0.4", {"start": v(18.44, -13.07) * mm, "end": v(18.44, -9.44) * mm});
            skLineSegment(sketch, "E17.16.0.5", {"start": v(18.44, -31.07) * mm, "end": v(18.44, -27.44) * mm});
            skPoint(sketch, "E17.16.0.6", {"position": v(20.25, 33.75) * mm});
            skLineSegment(sketch, "E17.16.0.7", {"start": v(22.07, 9.43) * mm, "end": v(22.07, 13.06) * mm});
            skLineSegment(sketch, "E17.16.0.8", {"start": v(22.07, -31.07) * mm, "end": v(22.07, -27.44) * mm});
            skLineSegment(sketch, "E17.16.0.9", {"start": v(22.07, 31.93) * mm, "end": v(22.07, 27.43) * mm, "construction": true});
            skLineSegment(sketch, "E17.16.0.10", {"start": v(22.07, 31.06) * mm, "end": v(18.44, 31.06) * mm});
            skLineSegment(sketch, "E17.16.0.11", {"start": v(22.07, 4.93) * mm, "end": v(18.44, 4.93) * mm});
            skLineSegment(sketch, "E17.16.0.12", {"start": v(22.07, -13.07) * mm, "end": v(18.44, -13.07) * mm});
            skLineSegment(sketch, "E17.16.0.13", {"start": v(22.07, -31.07) * mm, "end": v(18.44, -31.07) * mm});
            skLineSegment(sketch, "E17.16.0.14", {"start": v(18.44, 31.93) * mm, "end": v(18.44, 35.56) * mm});
            skLineSegment(sketch, "E17.16.0.15", {"start": v(22.07, 31.93) * mm, "end": v(22.07, 35.56) * mm});
            skLineSegment(sketch, "E17.16.0.16", {"start": v(22.07, 31.93) * mm, "end": v(18.44, 31.93) * mm});
            skLineSegment(sketch, "E17.16.0.17", {"start": v(18.44, 18.43) * mm, "end": v(18.44, 22.06) * mm});
            skLineSegment(sketch, "E17.16.0.18", {"start": v(22.07, 13.06) * mm, "end": v(18.44, 13.06) * mm});
            skLineSegment(sketch, "E17.16.0.19", {"start": v(22.07, -4.94) * mm, "end": v(18.44, -4.94) * mm});
            skLineSegment(sketch, "E17.16.0.20", {"start": v(22.07, -22.94) * mm, "end": v(18.44, -22.94) * mm});
            skLineSegment(sketch, "E17.16.0.21", {"start": v(22.07, -26.57) * mm, "end": v(22.07, -22.94) * mm});
            skLineSegment(sketch, "E17.16.0.22", {"start": v(18.44, -8.57) * mm, "end": v(18.44, -4.94) * mm});
            skLineSegment(sketch, "E17.16.0.23", {"start": v(18.44, -26.57) * mm, "end": v(18.44, -22.94) * mm});
            skLineSegment(sketch, "E17.16.0.24", {"start": v(22.07, 17.56) * mm, "end": v(18.44, 17.56) * mm});
            skLineSegment(sketch, "E17.16.0.25", {"start": v(22.07, -0.44) * mm, "end": v(18.44, -0.44) * mm});
            skLineSegment(sketch, "E17.16.0.26", {"start": v(22.07, -9.44) * mm, "end": v(18.44, -9.44) * mm});
            skLineSegment(sketch, "E17.16.0.27", {"start": v(18.44, -22.07) * mm, "end": v(18.44, -18.44) * mm});
            skLineSegment(sketch, "E17.16.0.28", {"start": v(18.44, 13.93) * mm, "end": v(18.44, 17.56) * mm});
            skLineSegment(sketch, "E17.16.0.29", {"start": v(18.44, -4.07) * mm, "end": v(18.44, -0.44) * mm});
            skLineSegment(sketch, "E17.16.0.30", {"start": v(22.07, 13.93) * mm, "end": v(18.44, 13.93) * mm});
            skLineSegment(sketch, "E17.16.0.31", {"start": v(22.07, -4.07) * mm, "end": v(18.44, -4.07) * mm});
            skLineSegment(sketch, "E17.16.0.32", {"start": v(22.07, -17.57) * mm, "end": v(18.44, -17.57) * mm});
            skLineSegment(sketch, "E17.16.0.33", {"start": v(22.07, -27.44) * mm, "end": v(18.44, -27.44) * mm});
            skLineSegment(sketch, "E17.16.0.34", {"start": v(22.07, -35.57) * mm, "end": v(18.44, -35.57) * mm});
            skLineSegment(sketch, "E17.16.0.35", {"start": v(22.07, 0.43) * mm, "end": v(18.44, 0.43) * mm});
            skLineSegment(sketch, "E17.16.0.36", {"start": v(22.07, 13.93) * mm, "end": v(22.07, 17.56) * mm});
            skLineSegment(sketch, "E17.16.0.37", {"start": v(22.07, -22.07) * mm, "end": v(22.07, -18.44) * mm});
            skLineSegment(sketch, "E17.16.0.38", {"start": v(22.07, -17.57) * mm, "end": v(22.07, -13.94) * mm});
            skLineSegment(sketch, "E17.16.0.39", {"start": v(18.44, 4.93) * mm, "end": v(18.44, 8.56) * mm});
            skLineSegment(sketch, "E17.16.0.40", {"start": v(22.07, 26.56) * mm, "end": v(18.44, 26.56) * mm});
            skLineSegment(sketch, "E17.16.0.41", {"start": v(22.07, 9.43) * mm, "end": v(18.44, 9.43) * mm});
            skLineSegment(sketch, "E17.16.0.42", {"start": v(18.44, 22.93) * mm, "end": v(18.44, 26.56) * mm});
            skLineSegment(sketch, "E17.16.0.43", {"start": v(22.07, -13.94) * mm, "end": v(18.44, -13.94) * mm});
            skLineSegment(sketch, "E17.16.0.44", {"start": v(22.07, -31.94) * mm, "end": v(18.44, -31.94) * mm});
            skLineSegment(sketch, "E17.16.0.45", {"start": v(22.07, 22.06) * mm, "end": v(18.44, 22.06) * mm});
            skLineSegment(sketch, "E17.16.0.46", {"start": v(22.07, 4.06) * mm, "end": v(18.44, 4.06) * mm});
            skLineSegment(sketch, "E17.16.0.47", {"start": v(18.44, 0.43) * mm, "end": v(18.44, 4.06) * mm});
            skLineSegment(sketch, "E17.16.0.48", {"start": v(18.44, -35.57) * mm, "end": v(18.44, -31.94) * mm});
            skLineSegment(sketch, "E17.16.0.49", {"start": v(22.07, 0.43) * mm, "end": v(22.07, 4.06) * mm});
            skLineSegment(sketch, "E17.16.0.50", {"start": v(22.07, -26.57) * mm, "end": v(18.44, -26.57) * mm});
            skLineSegment(sketch, "E17.16.0.51", {"start": v(22.07, -35.57) * mm, "end": v(22.07, -31.94) * mm});
            skLineSegment(sketch, "E17.16.0.52", {"start": v(22.07, -4.07) * mm, "end": v(22.07, -0.44) * mm});
            skLineSegment(sketch, "E17.16.0.53", {"start": v(22.07, -22.07) * mm, "end": v(18.44, -22.07) * mm});
            skLineSegment(sketch, "E17.16.0.54", {"start": v(22.07, 18.43) * mm, "end": v(22.07, 22.06) * mm});
            skLineSegment(sketch, "E17.16.0.55", {"start": v(22.07, -18.44) * mm, "end": v(18.44, -18.44) * mm});
            skLineSegment(sketch, "E17.16.0.56", {"start": v(22.07, -8.57) * mm, "end": v(22.07, -4.94) * mm});
            skLineSegment(sketch, "E17.16.0.57", {"start": v(22.07, 18.43) * mm, "end": v(18.44, 18.43) * mm});
            skLineSegment(sketch, "E17.16.0.58", {"start": v(22.07, 35.56) * mm, "end": v(18.44, 35.56) * mm});
            skLineSegment(sketch, "E17.16.0.59", {"start": v(22.07, 4.93) * mm, "end": v(22.07, 8.56) * mm});
            skLineSegment(sketch, "E17.16.0.60", {"start": v(22.07, 27.43) * mm, "end": v(18.44, 27.43) * mm});
            skLineSegment(sketch, "E17.16.0.61", {"start": v(22.07, -8.57) * mm, "end": v(18.44, -8.57) * mm});
            skLineSegment(sketch, "E17.16.0.62", {"start": v(22.07, 8.56) * mm, "end": v(18.44, 8.56) * mm});
            skLineSegment(sketch, "E17.16.0.63", {"start": v(18.44, -17.57) * mm, "end": v(18.44, -13.94) * mm});
            skLineSegment(sketch, "E17.16.0.64", {"start": v(22.07, 22.93) * mm, "end": v(18.44, 22.93) * mm});
            skLineSegment(sketch, "E17.16.0.65", {"start": v(22.07, 22.93) * mm, "end": v(22.07, 26.56) * mm});
            skLineSegment(sketch, "E17.17.0.0", {"start": v(22.94, 27.43) * mm, "end": v(22.94, 31.06) * mm});
            skLineSegment(sketch, "E17.17.0.1", {"start": v(26.57, 27.43) * mm, "end": v(26.57, 31.06) * mm});
            skLineSegment(sketch, "E17.17.0.2", {"start": v(26.57, -13.07) * mm, "end": v(26.57, -9.44) * mm});
            skLineSegment(sketch, "E17.17.0.3", {"start": v(22.94, 9.43) * mm, "end": v(22.94, 13.06) * mm});
            skLineSegment(sketch, "E17.17.0.4", {"start": v(22.94, -13.07) * mm, "end": v(22.94, -9.44) * mm});
            skLineSegment(sketch, "E17.17.0.5", {"start": v(22.94, -31.07) * mm, "end": v(22.94, -27.44) * mm});
            skPoint(sketch, "E17.17.0.6", {"position": v(24.75, 33.75) * mm});
            skLineSegment(sketch, "E17.17.0.7", {"start": v(26.57, 9.43) * mm, "end": v(26.57, 13.06) * mm});
            skLineSegment(sketch, "E17.17.0.8", {"start": v(26.57, -31.07) * mm, "end": v(26.57, -27.44) * mm});
            skLineSegment(sketch, "E17.17.0.9", {"start": v(26.57, 31.93) * mm, "end": v(26.57, 27.43) * mm, "construction": true});
            skLineSegment(sketch, "E17.17.0.10", {"start": v(26.57, 31.06) * mm, "end": v(22.94, 31.06) * mm});
            skLineSegment(sketch, "E17.17.0.11", {"start": v(26.57, 4.93) * mm, "end": v(22.94, 4.93) * mm});
            skLineSegment(sketch, "E17.17.0.12", {"start": v(26.57, -13.07) * mm, "end": v(22.94, -13.07) * mm});
            skLineSegment(sketch, "E17.17.0.13", {"start": v(26.57, -31.07) * mm, "end": v(22.94, -31.07) * mm});
            skLineSegment(sketch, "E17.17.0.14", {"start": v(22.94, 31.93) * mm, "end": v(22.94, 35.56) * mm});
            skLineSegment(sketch, "E17.17.0.15", {"start": v(26.57, 31.93) * mm, "end": v(26.57, 35.56) * mm});
            skLineSegment(sketch, "E17.17.0.16", {"start": v(26.57, 31.93) * mm, "end": v(22.94, 31.93) * mm});
            skLineSegment(sketch, "E17.17.0.17", {"start": v(22.94, 18.43) * mm, "end": v(22.94, 22.06) * mm});
            skLineSegment(sketch, "E17.17.0.18", {"start": v(26.57, 13.06) * mm, "end": v(22.94, 13.06) * mm});
            skLineSegment(sketch, "E17.17.0.19", {"start": v(26.57, -4.94) * mm, "end": v(22.94, -4.94) * mm});
            skLineSegment(sketch, "E17.17.0.20", {"start": v(26.57, -22.94) * mm, "end": v(22.94, -22.94) * mm});
            skLineSegment(sketch, "E17.17.0.21", {"start": v(26.57, -26.57) * mm, "end": v(26.57, -22.94) * mm});
            skLineSegment(sketch, "E17.17.0.22", {"start": v(22.94, -8.57) * mm, "end": v(22.94, -4.94) * mm});
            skLineSegment(sketch, "E17.17.0.23", {"start": v(22.94, -26.57) * mm, "end": v(22.94, -22.94) * mm});
            skLineSegment(sketch, "E17.17.0.24", {"start": v(26.57, 17.56) * mm, "end": v(22.94, 17.56) * mm});
            skLineSegment(sketch, "E17.17.0.25", {"start": v(26.57, -0.44) * mm, "end": v(22.94, -0.44) * mm});
            skLineSegment(sketch, "E17.17.0.26", {"start": v(26.57, -9.44) * mm, "end": v(22.94, -9.44) * mm});
            skLineSegment(sketch, "E17.17.0.27", {"start": v(22.94, -22.07) * mm, "end": v(22.94, -18.44) * mm});
            skLineSegment(sketch, "E17.17.0.28", {"start": v(22.94, 13.93) * mm, "end": v(22.94, 17.56) * mm});
            skLineSegment(sketch, "E17.17.0.29", {"start": v(22.94, -4.07) * mm, "end": v(22.94, -0.44) * mm});
            skLineSegment(sketch, "E17.17.0.30", {"start": v(26.57, 13.93) * mm, "end": v(22.94, 13.93) * mm});
            skLineSegment(sketch, "E17.17.0.31", {"start": v(26.57, -4.07) * mm, "end": v(22.94, -4.07) * mm});
            skLineSegment(sketch, "E17.17.0.32", {"start": v(26.57, -17.57) * mm, "end": v(22.94, -17.57) * mm});
            skLineSegment(sketch, "E17.17.0.33", {"start": v(26.57, -27.44) * mm, "end": v(22.94, -27.44) * mm});
            skLineSegment(sketch, "E17.17.0.34", {"start": v(26.57, -35.57) * mm, "end": v(22.94, -35.57) * mm});
            skLineSegment(sketch, "E17.17.0.35", {"start": v(26.57, 0.43) * mm, "end": v(22.94, 0.43) * mm});
            skLineSegment(sketch, "E17.17.0.36", {"start": v(26.57, 13.93) * mm, "end": v(26.57, 17.56) * mm});
            skLineSegment(sketch, "E17.17.0.37", {"start": v(26.57, -22.07) * mm, "end": v(26.57, -18.44) * mm});
            skLineSegment(sketch, "E17.17.0.38", {"start": v(26.57, -17.57) * mm, "end": v(26.57, -13.94) * mm});
            skLineSegment(sketch, "E17.17.0.39", {"start": v(22.94, 4.93) * mm, "end": v(22.94, 8.56) * mm});
            skLineSegment(sketch, "E17.17.0.40", {"start": v(26.57, 26.56) * mm, "end": v(22.94, 26.56) * mm});
            skLineSegment(sketch, "E17.17.0.41", {"start": v(26.57, 9.43) * mm, "end": v(22.94, 9.43) * mm});
            skLineSegment(sketch, "E17.17.0.42", {"start": v(22.94, 22.93) * mm, "end": v(22.94, 26.56) * mm});
            skLineSegment(sketch, "E17.17.0.43", {"start": v(26.57, -13.94) * mm, "end": v(22.94, -13.94) * mm});
            skLineSegment(sketch, "E17.17.0.44", {"start": v(26.57, -31.94) * mm, "end": v(22.94, -31.94) * mm});
            skLineSegment(sketch, "E17.17.0.45", {"start": v(26.57, 22.06) * mm, "end": v(22.94, 22.06) * mm});
            skLineSegment(sketch, "E17.17.0.46", {"start": v(26.57, 4.06) * mm, "end": v(22.94, 4.06) * mm});
            skLineSegment(sketch, "E17.17.0.47", {"start": v(22.94, 0.43) * mm, "end": v(22.94, 4.06) * mm});
            skLineSegment(sketch, "E17.17.0.48", {"start": v(22.94, -35.57) * mm, "end": v(22.94, -31.94) * mm});
            skLineSegment(sketch, "E17.17.0.49", {"start": v(26.57, 0.43) * mm, "end": v(26.57, 4.06) * mm});
            skLineSegment(sketch, "E17.17.0.50", {"start": v(26.57, -26.57) * mm, "end": v(22.94, -26.57) * mm});
            skLineSegment(sketch, "E17.17.0.51", {"start": v(26.57, -35.57) * mm, "end": v(26.57, -31.94) * mm});
            skLineSegment(sketch, "E17.17.0.52", {"start": v(26.57, -4.07) * mm, "end": v(26.57, -0.44) * mm});
            skLineSegment(sketch, "E17.17.0.53", {"start": v(26.57, -22.07) * mm, "end": v(22.94, -22.07) * mm});
            skLineSegment(sketch, "E17.17.0.54", {"start": v(26.57, 18.43) * mm, "end": v(26.57, 22.06) * mm});
            skLineSegment(sketch, "E17.17.0.55", {"start": v(26.57, -18.44) * mm, "end": v(22.94, -18.44) * mm});
            skLineSegment(sketch, "E17.17.0.56", {"start": v(26.57, -8.57) * mm, "end": v(26.57, -4.94) * mm});
            skLineSegment(sketch, "E17.17.0.57", {"start": v(26.57, 18.43) * mm, "end": v(22.94, 18.43) * mm});
            skLineSegment(sketch, "E17.17.0.58", {"start": v(26.57, 35.56) * mm, "end": v(22.94, 35.56) * mm});
            skLineSegment(sketch, "E17.17.0.59", {"start": v(26.57, 4.93) * mm, "end": v(26.57, 8.56) * mm});
            skLineSegment(sketch, "E17.17.0.60", {"start": v(26.57, 27.43) * mm, "end": v(22.94, 27.43) * mm});
            skLineSegment(sketch, "E17.17.0.61", {"start": v(26.57, -8.57) * mm, "end": v(22.94, -8.57) * mm});
            skLineSegment(sketch, "E17.17.0.62", {"start": v(26.57, 8.56) * mm, "end": v(22.94, 8.56) * mm});
            skLineSegment(sketch, "E17.17.0.63", {"start": v(22.94, -17.57) * mm, "end": v(22.94, -13.94) * mm});
            skLineSegment(sketch, "E17.17.0.64", {"start": v(26.57, 22.93) * mm, "end": v(22.94, 22.93) * mm});
            skLineSegment(sketch, "E17.17.0.65", {"start": v(26.57, 22.93) * mm, "end": v(26.57, 26.56) * mm});
            skLineSegment(sketch, "E17.18.0.0", {"start": v(27.44, 27.43) * mm, "end": v(27.44, 31.06) * mm});
            skLineSegment(sketch, "E17.18.0.1", {"start": v(31.07, 27.43) * mm, "end": v(31.07, 31.06) * mm});
            skLineSegment(sketch, "E17.18.0.2", {"start": v(31.07, -13.07) * mm, "end": v(31.07, -9.44) * mm});
            skLineSegment(sketch, "E17.18.0.3", {"start": v(27.44, 9.43) * mm, "end": v(27.44, 13.06) * mm});
            skLineSegment(sketch, "E17.18.0.4", {"start": v(27.44, -13.07) * mm, "end": v(27.44, -9.44) * mm});
            skLineSegment(sketch, "E17.18.0.5", {"start": v(27.44, -31.07) * mm, "end": v(27.44, -27.44) * mm});
            skPoint(sketch, "E17.18.0.6", {"position": v(29.25, 33.75) * mm});
            skLineSegment(sketch, "E17.18.0.7", {"start": v(31.07, 9.43) * mm, "end": v(31.07, 13.06) * mm});
            skLineSegment(sketch, "E17.18.0.8", {"start": v(31.07, -31.07) * mm, "end": v(31.07, -27.44) * mm});
            skLineSegment(sketch, "E17.18.0.9", {"start": v(31.07, 31.93) * mm, "end": v(31.07, 27.43) * mm, "construction": true});
            skLineSegment(sketch, "E17.18.0.10", {"start": v(31.07, 31.06) * mm, "end": v(27.44, 31.06) * mm});
            skLineSegment(sketch, "E17.18.0.11", {"start": v(31.07, 4.93) * mm, "end": v(27.44, 4.93) * mm});
            skLineSegment(sketch, "E17.18.0.12", {"start": v(31.07, -13.07) * mm, "end": v(27.44, -13.07) * mm});
            skLineSegment(sketch, "E17.18.0.13", {"start": v(31.07, -31.07) * mm, "end": v(27.44, -31.07) * mm});
            skLineSegment(sketch, "E17.18.0.14", {"start": v(27.44, 31.93) * mm, "end": v(27.44, 35.56) * mm});
            skLineSegment(sketch, "E17.18.0.15", {"start": v(31.07, 31.93) * mm, "end": v(31.07, 35.56) * mm});
            skLineSegment(sketch, "E17.18.0.16", {"start": v(31.07, 31.93) * mm, "end": v(27.44, 31.93) * mm});
            skLineSegment(sketch, "E17.18.0.17", {"start": v(27.44, 18.43) * mm, "end": v(27.44, 22.06) * mm});
            skLineSegment(sketch, "E17.18.0.18", {"start": v(31.07, 13.06) * mm, "end": v(27.44, 13.06) * mm});
            skLineSegment(sketch, "E17.18.0.19", {"start": v(31.07, -4.94) * mm, "end": v(27.44, -4.94) * mm});
            skLineSegment(sketch, "E17.18.0.20", {"start": v(31.07, -22.94) * mm, "end": v(27.44, -22.94) * mm});
            skLineSegment(sketch, "E17.18.0.21", {"start": v(31.07, -26.57) * mm, "end": v(31.07, -22.94) * mm});
            skLineSegment(sketch, "E17.18.0.22", {"start": v(27.44, -8.57) * mm, "end": v(27.44, -4.94) * mm});
            skLineSegment(sketch, "E17.18.0.23", {"start": v(27.44, -26.57) * mm, "end": v(27.44, -22.94) * mm});
            skLineSegment(sketch, "E17.18.0.24", {"start": v(31.07, 17.56) * mm, "end": v(27.44, 17.56) * mm});
            skLineSegment(sketch, "E17.18.0.25", {"start": v(31.07, -0.44) * mm, "end": v(27.44, -0.44) * mm});
            skLineSegment(sketch, "E17.18.0.26", {"start": v(31.07, -9.44) * mm, "end": v(27.44, -9.44) * mm});
            skLineSegment(sketch, "E17.18.0.27", {"start": v(27.44, -22.07) * mm, "end": v(27.44, -18.44) * mm});
            skLineSegment(sketch, "E17.18.0.28", {"start": v(27.44, 13.93) * mm, "end": v(27.44, 17.56) * mm});
            skLineSegment(sketch, "E17.18.0.29", {"start": v(27.44, -4.07) * mm, "end": v(27.44, -0.44) * mm});
            skLineSegment(sketch, "E17.18.0.30", {"start": v(31.07, 13.93) * mm, "end": v(27.44, 13.93) * mm});
            skLineSegment(sketch, "E17.18.0.31", {"start": v(31.07, -4.07) * mm, "end": v(27.44, -4.07) * mm});
            skLineSegment(sketch, "E17.18.0.32", {"start": v(31.07, -17.57) * mm, "end": v(27.44, -17.57) * mm});
            skLineSegment(sketch, "E17.18.0.33", {"start": v(31.07, -27.44) * mm, "end": v(27.44, -27.44) * mm});
            skLineSegment(sketch, "E17.18.0.34", {"start": v(31.07, -35.57) * mm, "end": v(27.44, -35.57) * mm});
            skLineSegment(sketch, "E17.18.0.35", {"start": v(31.07, 0.43) * mm, "end": v(27.44, 0.43) * mm});
            skLineSegment(sketch, "E17.18.0.36", {"start": v(31.07, 13.93) * mm, "end": v(31.07, 17.56) * mm});
            skLineSegment(sketch, "E17.18.0.37", {"start": v(31.07, -22.07) * mm, "end": v(31.07, -18.44) * mm});
            skLineSegment(sketch, "E17.18.0.38", {"start": v(31.07, -17.57) * mm, "end": v(31.07, -13.94) * mm});
            skLineSegment(sketch, "E17.18.0.39", {"start": v(27.44, 4.93) * mm, "end": v(27.44, 8.56) * mm});
            skLineSegment(sketch, "E17.18.0.40", {"start": v(31.07, 26.56) * mm, "end": v(27.44, 26.56) * mm});
            skLineSegment(sketch, "E17.18.0.41", {"start": v(31.07, 9.43) * mm, "end": v(27.44, 9.43) * mm});
            skLineSegment(sketch, "E17.18.0.42", {"start": v(27.44, 22.93) * mm, "end": v(27.44, 26.56) * mm});
            skLineSegment(sketch, "E17.18.0.43", {"start": v(31.07, -13.94) * mm, "end": v(27.44, -13.94) * mm});
            skLineSegment(sketch, "E17.18.0.44", {"start": v(31.07, -31.94) * mm, "end": v(27.44, -31.94) * mm});
            skLineSegment(sketch, "E17.18.0.45", {"start": v(31.07, 22.06) * mm, "end": v(27.44, 22.06) * mm});
            skLineSegment(sketch, "E17.18.0.46", {"start": v(31.07, 4.06) * mm, "end": v(27.44, 4.06) * mm});
            skLineSegment(sketch, "E17.18.0.47", {"start": v(27.44, 0.43) * mm, "end": v(27.44, 4.06) * mm});
            skLineSegment(sketch, "E17.18.0.48", {"start": v(27.44, -35.57) * mm, "end": v(27.44, -31.94) * mm});
            skLineSegment(sketch, "E17.18.0.49", {"start": v(31.07, 0.43) * mm, "end": v(31.07, 4.06) * mm});
            skLineSegment(sketch, "E17.18.0.50", {"start": v(31.07, -26.57) * mm, "end": v(27.44, -26.57) * mm});
            skLineSegment(sketch, "E17.18.0.51", {"start": v(31.07, -35.57) * mm, "end": v(31.07, -31.94) * mm});
            skLineSegment(sketch, "E17.18.0.52", {"start": v(31.07, -4.07) * mm, "end": v(31.07, -0.44) * mm});
            skLineSegment(sketch, "E17.18.0.53", {"start": v(31.07, -22.07) * mm, "end": v(27.44, -22.07) * mm});
            skLineSegment(sketch, "E17.18.0.54", {"start": v(31.07, 18.43) * mm, "end": v(31.07, 22.06) * mm});
            skLineSegment(sketch, "E17.18.0.55", {"start": v(31.07, -18.44) * mm, "end": v(27.44, -18.44) * mm});
            skLineSegment(sketch, "E17.18.0.56", {"start": v(31.07, -8.57) * mm, "end": v(31.07, -4.94) * mm});
            skLineSegment(sketch, "E17.18.0.57", {"start": v(31.07, 18.43) * mm, "end": v(27.44, 18.43) * mm});
            skLineSegment(sketch, "E17.18.0.58", {"start": v(31.07, 35.56) * mm, "end": v(27.44, 35.56) * mm});
            skLineSegment(sketch, "E17.18.0.59", {"start": v(31.07, 4.93) * mm, "end": v(31.07, 8.56) * mm});
            skLineSegment(sketch, "E17.18.0.60", {"start": v(31.07, 27.43) * mm, "end": v(27.44, 27.43) * mm});
            skLineSegment(sketch, "E17.18.0.61", {"start": v(31.07, -8.57) * mm, "end": v(27.44, -8.57) * mm});
            skLineSegment(sketch, "E17.18.0.62", {"start": v(31.07, 8.56) * mm, "end": v(27.44, 8.56) * mm});
            skLineSegment(sketch, "E17.18.0.63", {"start": v(27.44, -17.57) * mm, "end": v(27.44, -13.94) * mm});
            skLineSegment(sketch, "E17.18.0.64", {"start": v(31.07, 22.93) * mm, "end": v(27.44, 22.93) * mm});
            skLineSegment(sketch, "E17.18.0.65", {"start": v(31.07, 22.93) * mm, "end": v(31.07, 26.56) * mm});
            skLineSegment(sketch, "E17.19.0.0", {"start": v(31.94, 27.43) * mm, "end": v(31.94, 31.06) * mm});
            skLineSegment(sketch, "E17.19.0.1", {"start": v(35.57, 27.43) * mm, "end": v(35.57, 31.06) * mm});
            skLineSegment(sketch, "E17.19.0.2", {"start": v(35.57, -13.07) * mm, "end": v(35.57, -9.44) * mm});
            skLineSegment(sketch, "E17.19.0.3", {"start": v(31.94, 9.43) * mm, "end": v(31.94, 13.06) * mm});
            skLineSegment(sketch, "E17.19.0.4", {"start": v(31.94, -13.07) * mm, "end": v(31.94, -9.44) * mm});
            skLineSegment(sketch, "E17.19.0.5", {"start": v(31.94, -31.07) * mm, "end": v(31.94, -27.44) * mm});
            skPoint(sketch, "E17.19.0.6", {"position": v(33.75, 33.75) * mm});
            skLineSegment(sketch, "E17.19.0.7", {"start": v(35.57, 9.43) * mm, "end": v(35.57, 13.06) * mm});
            skLineSegment(sketch, "E17.19.0.8", {"start": v(35.57, -31.07) * mm, "end": v(35.57, -27.44) * mm});
            skLineSegment(sketch, "E17.19.0.9", {"start": v(35.57, 31.93) * mm, "end": v(35.57, 27.43) * mm, "construction": true});
            skLineSegment(sketch, "E17.19.0.10", {"start": v(35.57, 31.06) * mm, "end": v(31.94, 31.06) * mm});
            skLineSegment(sketch, "E17.19.0.11", {"start": v(35.57, 4.93) * mm, "end": v(31.94, 4.93) * mm});
            skLineSegment(sketch, "E17.19.0.12", {"start": v(35.57, -13.07) * mm, "end": v(31.94, -13.07) * mm});
            skLineSegment(sketch, "E17.19.0.13", {"start": v(35.57, -31.07) * mm, "end": v(31.94, -31.07) * mm});
            skLineSegment(sketch, "E17.19.0.14", {"start": v(31.94, 31.93) * mm, "end": v(31.94, 35.56) * mm});
            skLineSegment(sketch, "E17.19.0.15", {"start": v(35.57, 31.93) * mm, "end": v(35.57, 35.56) * mm});
            skLineSegment(sketch, "E17.19.0.16", {"start": v(35.57, 31.93) * mm, "end": v(31.94, 31.93) * mm});
            skLineSegment(sketch, "E17.19.0.17", {"start": v(31.94, 18.43) * mm, "end": v(31.94, 22.06) * mm});
            skLineSegment(sketch, "E17.19.0.18", {"start": v(35.57, 13.06) * mm, "end": v(31.94, 13.06) * mm});
            skLineSegment(sketch, "E17.19.0.19", {"start": v(35.57, -4.94) * mm, "end": v(31.94, -4.94) * mm});
            skLineSegment(sketch, "E17.19.0.20", {"start": v(35.57, -22.94) * mm, "end": v(31.94, -22.94) * mm});
            skLineSegment(sketch, "E17.19.0.21", {"start": v(35.57, -26.57) * mm, "end": v(35.57, -22.94) * mm});
            skLineSegment(sketch, "E17.19.0.22", {"start": v(31.94, -8.57) * mm, "end": v(31.94, -4.94) * mm});
            skLineSegment(sketch, "E17.19.0.23", {"start": v(31.94, -26.57) * mm, "end": v(31.94, -22.94) * mm});
            skLineSegment(sketch, "E17.19.0.24", {"start": v(35.57, 17.56) * mm, "end": v(31.94, 17.56) * mm});
            skLineSegment(sketch, "E17.19.0.25", {"start": v(35.57, -0.44) * mm, "end": v(31.94, -0.44) * mm});
            skLineSegment(sketch, "E17.19.0.26", {"start": v(35.57, -9.44) * mm, "end": v(31.94, -9.44) * mm});
            skLineSegment(sketch, "E17.19.0.27", {"start": v(31.94, -22.07) * mm, "end": v(31.94, -18.44) * mm});
            skLineSegment(sketch, "E17.19.0.28", {"start": v(31.94, 13.93) * mm, "end": v(31.94, 17.56) * mm});
            skLineSegment(sketch, "E17.19.0.29", {"start": v(31.94, -4.07) * mm, "end": v(31.94, -0.44) * mm});
            skLineSegment(sketch, "E17.19.0.30", {"start": v(35.57, 13.93) * mm, "end": v(31.94, 13.93) * mm});
            skLineSegment(sketch, "E17.19.0.31", {"start": v(35.57, -4.07) * mm, "end": v(31.94, -4.07) * mm});
            skLineSegment(sketch, "E17.19.0.32", {"start": v(35.57, -17.57) * mm, "end": v(31.94, -17.57) * mm});
            skLineSegment(sketch, "E17.19.0.33", {"start": v(35.57, -27.44) * mm, "end": v(31.94, -27.44) * mm});
            skLineSegment(sketch, "E17.19.0.34", {"start": v(35.57, -35.57) * mm, "end": v(31.94, -35.57) * mm});
            skLineSegment(sketch, "E17.19.0.35", {"start": v(35.57, 0.43) * mm, "end": v(31.94, 0.43) * mm});
            skLineSegment(sketch, "E17.19.0.36", {"start": v(35.57, 13.93) * mm, "end": v(35.57, 17.56) * mm});
            skLineSegment(sketch, "E17.19.0.37", {"start": v(35.57, -22.07) * mm, "end": v(35.57, -18.44) * mm});
            skLineSegment(sketch, "E17.19.0.38", {"start": v(35.57, -17.57) * mm, "end": v(35.57, -13.94) * mm});
            skLineSegment(sketch, "E17.19.0.39", {"start": v(31.94, 4.93) * mm, "end": v(31.94, 8.56) * mm});
            skLineSegment(sketch, "E17.19.0.40", {"start": v(35.57, 26.56) * mm, "end": v(31.94, 26.56) * mm});
            skLineSegment(sketch, "E17.19.0.41", {"start": v(35.57, 9.43) * mm, "end": v(31.94, 9.43) * mm});
            skLineSegment(sketch, "E17.19.0.42", {"start": v(31.94, 22.93) * mm, "end": v(31.94, 26.56) * mm});
            skLineSegment(sketch, "E17.19.0.43", {"start": v(35.57, -13.94) * mm, "end": v(31.94, -13.94) * mm});
            skLineSegment(sketch, "E17.19.0.44", {"start": v(35.57, -31.94) * mm, "end": v(31.94, -31.94) * mm});
            skLineSegment(sketch, "E17.19.0.45", {"start": v(35.57, 22.06) * mm, "end": v(31.94, 22.06) * mm});
            skLineSegment(sketch, "E17.19.0.46", {"start": v(35.57, 4.06) * mm, "end": v(31.94, 4.06) * mm});
            skLineSegment(sketch, "E17.19.0.47", {"start": v(31.94, 0.43) * mm, "end": v(31.94, 4.06) * mm});
            skLineSegment(sketch, "E17.19.0.48", {"start": v(31.94, -35.57) * mm, "end": v(31.94, -31.94) * mm});
            skLineSegment(sketch, "E17.19.0.49", {"start": v(35.57, 0.43) * mm, "end": v(35.57, 4.06) * mm});
            skLineSegment(sketch, "E17.19.0.50", {"start": v(35.57, -26.57) * mm, "end": v(31.94, -26.57) * mm});
            skLineSegment(sketch, "E17.19.0.51", {"start": v(35.57, -35.57) * mm, "end": v(35.57, -31.94) * mm});
            skLineSegment(sketch, "E17.19.0.52", {"start": v(35.57, -4.07) * mm, "end": v(35.57, -0.44) * mm});
            skLineSegment(sketch, "E17.19.0.53", {"start": v(35.57, -22.07) * mm, "end": v(31.94, -22.07) * mm});
            skLineSegment(sketch, "E17.19.0.54", {"start": v(35.57, 18.43) * mm, "end": v(35.57, 22.06) * mm});
            skLineSegment(sketch, "E17.19.0.55", {"start": v(35.57, -18.44) * mm, "end": v(31.94, -18.44) * mm});
            skLineSegment(sketch, "E17.19.0.56", {"start": v(35.57, -8.57) * mm, "end": v(35.57, -4.94) * mm});
            skLineSegment(sketch, "E17.19.0.57", {"start": v(35.57, 18.43) * mm, "end": v(31.94, 18.43) * mm});
            skLineSegment(sketch, "E17.19.0.58", {"start": v(35.57, 35.56) * mm, "end": v(31.94, 35.56) * mm});
            skLineSegment(sketch, "E17.19.0.59", {"start": v(35.57, 4.93) * mm, "end": v(35.57, 8.56) * mm});
            skLineSegment(sketch, "E17.19.0.60", {"start": v(35.57, 27.43) * mm, "end": v(31.94, 27.43) * mm});
            skLineSegment(sketch, "E17.19.0.61", {"start": v(35.57, -8.57) * mm, "end": v(31.94, -8.57) * mm});
            skLineSegment(sketch, "E17.19.0.62", {"start": v(35.57, 8.56) * mm, "end": v(31.94, 8.56) * mm});
            skLineSegment(sketch, "E17.19.0.63", {"start": v(31.94, -17.57) * mm, "end": v(31.94, -13.94) * mm});
            skLineSegment(sketch, "E17.19.0.64", {"start": v(35.57, 22.93) * mm, "end": v(31.94, 22.93) * mm});
            skLineSegment(sketch, "E17.19.0.65", {"start": v(35.57, 22.93) * mm, "end": v(35.57, 26.56) * mm});
            skLineSegment(sketch, "E17.20.0.0", {"start": v(36.44, 27.43) * mm, "end": v(36.44, 31.06) * mm});
            skLineSegment(sketch, "E17.20.0.1", {"start": v(40.07, 27.43) * mm, "end": v(40.07, 31.06) * mm});
            skLineSegment(sketch, "E17.20.0.2", {"start": v(40.07, -13.07) * mm, "end": v(40.07, -9.44) * mm});
            skLineSegment(sketch, "E17.20.0.3", {"start": v(36.44, 9.43) * mm, "end": v(36.44, 13.06) * mm});
            skLineSegment(sketch, "E17.20.0.4", {"start": v(36.44, -13.07) * mm, "end": v(36.44, -9.44) * mm});
            skLineSegment(sketch, "E17.20.0.5", {"start": v(36.44, -31.07) * mm, "end": v(36.44, -27.44) * mm});
            skPoint(sketch, "E17.20.0.6", {"position": v(38.25, 33.75) * mm});
            skLineSegment(sketch, "E17.20.0.7", {"start": v(40.07, 9.43) * mm, "end": v(40.07, 13.06) * mm});
            skLineSegment(sketch, "E17.20.0.8", {"start": v(40.07, -31.07) * mm, "end": v(40.07, -27.44) * mm});
            skLineSegment(sketch, "E17.20.0.9", {"start": v(40.07, 31.93) * mm, "end": v(40.07, 27.43) * mm, "construction": true});
            skLineSegment(sketch, "E17.20.0.10", {"start": v(40.07, 31.06) * mm, "end": v(36.44, 31.06) * mm});
            skLineSegment(sketch, "E17.20.0.11", {"start": v(40.07, 4.93) * mm, "end": v(36.44, 4.93) * mm});
            skLineSegment(sketch, "E17.20.0.12", {"start": v(40.07, -13.07) * mm, "end": v(36.44, -13.07) * mm});
            skLineSegment(sketch, "E17.20.0.13", {"start": v(40.07, -31.07) * mm, "end": v(36.44, -31.07) * mm});
            skLineSegment(sketch, "E17.20.0.14", {"start": v(36.44, 31.93) * mm, "end": v(36.44, 35.56) * mm});
            skLineSegment(sketch, "E17.20.0.15", {"start": v(40.07, 31.93) * mm, "end": v(40.07, 35.56) * mm});
            skLineSegment(sketch, "E17.20.0.16", {"start": v(40.07, 31.93) * mm, "end": v(36.44, 31.93) * mm});
            skLineSegment(sketch, "E17.20.0.17", {"start": v(36.44, 18.43) * mm, "end": v(36.44, 22.06) * mm});
            skLineSegment(sketch, "E17.20.0.18", {"start": v(40.07, 13.06) * mm, "end": v(36.44, 13.06) * mm});
            skLineSegment(sketch, "E17.20.0.19", {"start": v(40.07, -4.94) * mm, "end": v(36.44, -4.94) * mm});
            skLineSegment(sketch, "E17.20.0.20", {"start": v(40.07, -22.94) * mm, "end": v(36.44, -22.94) * mm});
            skLineSegment(sketch, "E17.20.0.21", {"start": v(40.07, -26.57) * mm, "end": v(40.07, -22.94) * mm});
            skLineSegment(sketch, "E17.20.0.22", {"start": v(36.44, -8.57) * mm, "end": v(36.44, -4.94) * mm});
            skLineSegment(sketch, "E17.20.0.23", {"start": v(36.44, -26.57) * mm, "end": v(36.44, -22.94) * mm});
            skLineSegment(sketch, "E17.20.0.24", {"start": v(40.07, 17.56) * mm, "end": v(36.44, 17.56) * mm});
            skLineSegment(sketch, "E17.20.0.25", {"start": v(40.07, -0.44) * mm, "end": v(36.44, -0.44) * mm});
            skLineSegment(sketch, "E17.20.0.26", {"start": v(40.07, -9.44) * mm, "end": v(36.44, -9.44) * mm});
            skLineSegment(sketch, "E17.20.0.27", {"start": v(36.44, -22.07) * mm, "end": v(36.44, -18.44) * mm});
            skLineSegment(sketch, "E17.20.0.28", {"start": v(36.44, 13.93) * mm, "end": v(36.44, 17.56) * mm});
            skLineSegment(sketch, "E17.20.0.29", {"start": v(36.44, -4.07) * mm, "end": v(36.44, -0.44) * mm});
            skLineSegment(sketch, "E17.20.0.30", {"start": v(40.07, 13.93) * mm, "end": v(36.44, 13.93) * mm});
            skLineSegment(sketch, "E17.20.0.31", {"start": v(40.07, -4.07) * mm, "end": v(36.44, -4.07) * mm});
            skLineSegment(sketch, "E17.20.0.32", {"start": v(40.07, -17.57) * mm, "end": v(36.44, -17.57) * mm});
            skLineSegment(sketch, "E17.20.0.33", {"start": v(40.07, -27.44) * mm, "end": v(36.44, -27.44) * mm});
            skLineSegment(sketch, "E17.20.0.34", {"start": v(40.07, -35.57) * mm, "end": v(36.44, -35.57) * mm});
            skLineSegment(sketch, "E17.20.0.35", {"start": v(40.07, 0.43) * mm, "end": v(36.44, 0.43) * mm});
            skLineSegment(sketch, "E17.20.0.36", {"start": v(40.07, 13.93) * mm, "end": v(40.07, 17.56) * mm});
            skLineSegment(sketch, "E17.20.0.37", {"start": v(40.07, -22.07) * mm, "end": v(40.07, -18.44) * mm});
            skLineSegment(sketch, "E17.20.0.38", {"start": v(40.07, -17.57) * mm, "end": v(40.07, -13.94) * mm});
            skLineSegment(sketch, "E17.20.0.39", {"start": v(36.44, 4.93) * mm, "end": v(36.44, 8.56) * mm});
            skLineSegment(sketch, "E17.20.0.40", {"start": v(40.07, 26.56) * mm, "end": v(36.44, 26.56) * mm});
            skLineSegment(sketch, "E17.20.0.41", {"start": v(40.07, 9.43) * mm, "end": v(36.44, 9.43) * mm});
            skLineSegment(sketch, "E17.20.0.42", {"start": v(36.44, 22.93) * mm, "end": v(36.44, 26.56) * mm});
            skLineSegment(sketch, "E17.20.0.43", {"start": v(40.07, -13.94) * mm, "end": v(36.44, -13.94) * mm});
            skLineSegment(sketch, "E17.20.0.44", {"start": v(40.07, -31.94) * mm, "end": v(36.44, -31.94) * mm});
            skLineSegment(sketch, "E17.20.0.45", {"start": v(40.07, 22.06) * mm, "end": v(36.44, 22.06) * mm});
            skLineSegment(sketch, "E17.20.0.46", {"start": v(40.07, 4.06) * mm, "end": v(36.44, 4.06) * mm});
            skLineSegment(sketch, "E17.20.0.47", {"start": v(36.44, 0.43) * mm, "end": v(36.44, 4.06) * mm});
            skLineSegment(sketch, "E17.20.0.48", {"start": v(36.44, -35.57) * mm, "end": v(36.44, -31.94) * mm});
            skLineSegment(sketch, "E17.20.0.49", {"start": v(40.07, 0.43) * mm, "end": v(40.07, 4.06) * mm});
            skLineSegment(sketch, "E17.20.0.50", {"start": v(40.07, -26.57) * mm, "end": v(36.44, -26.57) * mm});
            skLineSegment(sketch, "E17.20.0.51", {"start": v(40.07, -35.57) * mm, "end": v(40.07, -31.94) * mm});
            skLineSegment(sketch, "E17.20.0.52", {"start": v(40.07, -4.07) * mm, "end": v(40.07, -0.44) * mm});
            skLineSegment(sketch, "E17.20.0.53", {"start": v(40.07, -22.07) * mm, "end": v(36.44, -22.07) * mm});
            skLineSegment(sketch, "E17.20.0.54", {"start": v(40.07, 18.43) * mm, "end": v(40.07, 22.06) * mm});
            skLineSegment(sketch, "E17.20.0.55", {"start": v(40.07, -18.44) * mm, "end": v(36.44, -18.44) * mm});
            skLineSegment(sketch, "E17.20.0.56", {"start": v(40.07, -8.57) * mm, "end": v(40.07, -4.94) * mm});
            skLineSegment(sketch, "E17.20.0.57", {"start": v(40.07, 18.43) * mm, "end": v(36.44, 18.43) * mm});
            skLineSegment(sketch, "E17.20.0.58", {"start": v(40.07, 35.56) * mm, "end": v(36.44, 35.56) * mm});
            skLineSegment(sketch, "E17.20.0.59", {"start": v(40.07, 4.93) * mm, "end": v(40.07, 8.56) * mm});
            skLineSegment(sketch, "E17.20.0.60", {"start": v(40.07, 27.43) * mm, "end": v(36.44, 27.43) * mm});
            skLineSegment(sketch, "E17.20.0.61", {"start": v(40.07, -8.57) * mm, "end": v(36.44, -8.57) * mm});
            skLineSegment(sketch, "E17.20.0.62", {"start": v(40.07, 8.56) * mm, "end": v(36.44, 8.56) * mm});
            skLineSegment(sketch, "E17.20.0.63", {"start": v(36.44, -17.57) * mm, "end": v(36.44, -13.94) * mm});
            skLineSegment(sketch, "E17.20.0.64", {"start": v(40.07, 22.93) * mm, "end": v(36.44, 22.93) * mm});
            skLineSegment(sketch, "E17.20.0.65", {"start": v(40.07, 22.93) * mm, "end": v(40.07, 26.56) * mm});
            skLineSegment(sketch, "E17.21.0.0", {"start": v(40.94, 27.43) * mm, "end": v(40.94, 31.06) * mm});
            skLineSegment(sketch, "E17.21.0.1", {"start": v(44.57, 27.43) * mm, "end": v(44.57, 31.06) * mm});
            skLineSegment(sketch, "E17.21.0.2", {"start": v(44.57, -13.07) * mm, "end": v(44.57, -9.44) * mm});
            skLineSegment(sketch, "E17.21.0.3", {"start": v(40.94, 9.43) * mm, "end": v(40.94, 13.06) * mm});
            skLineSegment(sketch, "E17.21.0.4", {"start": v(40.94, -13.07) * mm, "end": v(40.94, -9.44) * mm});
            skLineSegment(sketch, "E17.21.0.5", {"start": v(40.94, -31.07) * mm, "end": v(40.94, -27.44) * mm});
            skPoint(sketch, "E17.21.0.6", {"position": v(42.75, 33.75) * mm});
            skLineSegment(sketch, "E17.21.0.7", {"start": v(44.57, 9.43) * mm, "end": v(44.57, 13.06) * mm});
            skLineSegment(sketch, "E17.21.0.8", {"start": v(44.57, -31.07) * mm, "end": v(44.57, -27.44) * mm});
            skLineSegment(sketch, "E17.21.0.9", {"start": v(44.57, 31.93) * mm, "end": v(44.57, 27.43) * mm, "construction": true});
            skLineSegment(sketch, "E17.21.0.10", {"start": v(44.57, 31.06) * mm, "end": v(40.94, 31.06) * mm});
            skLineSegment(sketch, "E17.21.0.11", {"start": v(44.57, 4.93) * mm, "end": v(40.94, 4.93) * mm});
            skLineSegment(sketch, "E17.21.0.12", {"start": v(44.57, -13.07) * mm, "end": v(40.94, -13.07) * mm});
            skLineSegment(sketch, "E17.21.0.13", {"start": v(44.57, -31.07) * mm, "end": v(40.94, -31.07) * mm});
            skLineSegment(sketch, "E17.21.0.14", {"start": v(40.94, 31.93) * mm, "end": v(40.94, 35.56) * mm});
            skLineSegment(sketch, "E17.21.0.15", {"start": v(44.57, 31.93) * mm, "end": v(44.57, 35.56) * mm});
            skLineSegment(sketch, "E17.21.0.16", {"start": v(44.57, 31.93) * mm, "end": v(40.94, 31.93) * mm});
            skLineSegment(sketch, "E17.21.0.17", {"start": v(40.94, 18.43) * mm, "end": v(40.94, 22.06) * mm});
            skLineSegment(sketch, "E17.21.0.18", {"start": v(44.57, 13.06) * mm, "end": v(40.94, 13.06) * mm});
            skLineSegment(sketch, "E17.21.0.19", {"start": v(44.57, -4.94) * mm, "end": v(40.94, -4.94) * mm});
            skLineSegment(sketch, "E17.21.0.20", {"start": v(44.57, -22.94) * mm, "end": v(40.94, -22.94) * mm});
            skLineSegment(sketch, "E17.21.0.21", {"start": v(44.57, -26.57) * mm, "end": v(44.57, -22.94) * mm});
            skLineSegment(sketch, "E17.21.0.22", {"start": v(40.94, -8.57) * mm, "end": v(40.94, -4.94) * mm});
            skLineSegment(sketch, "E17.21.0.23", {"start": v(40.94, -26.57) * mm, "end": v(40.94, -22.94) * mm});
            skLineSegment(sketch, "E17.21.0.24", {"start": v(44.57, 17.56) * mm, "end": v(40.94, 17.56) * mm});
            skLineSegment(sketch, "E17.21.0.25", {"start": v(44.57, -0.44) * mm, "end": v(40.94, -0.44) * mm});
            skLineSegment(sketch, "E17.21.0.26", {"start": v(44.57, -9.44) * mm, "end": v(40.94, -9.44) * mm});
            skLineSegment(sketch, "E17.21.0.27", {"start": v(40.94, -22.07) * mm, "end": v(40.94, -18.44) * mm});
            skLineSegment(sketch, "E17.21.0.28", {"start": v(40.94, 13.93) * mm, "end": v(40.94, 17.56) * mm});
            skLineSegment(sketch, "E17.21.0.29", {"start": v(40.94, -4.07) * mm, "end": v(40.94, -0.44) * mm});
            skLineSegment(sketch, "E17.21.0.30", {"start": v(44.57, 13.93) * mm, "end": v(40.94, 13.93) * mm});
            skLineSegment(sketch, "E17.21.0.31", {"start": v(44.57, -4.07) * mm, "end": v(40.94, -4.07) * mm});
            skLineSegment(sketch, "E17.21.0.32", {"start": v(44.57, -17.57) * mm, "end": v(40.94, -17.57) * mm});
            skLineSegment(sketch, "E17.21.0.33", {"start": v(44.57, -27.44) * mm, "end": v(40.94, -27.44) * mm});
            skLineSegment(sketch, "E17.21.0.34", {"start": v(44.57, -35.57) * mm, "end": v(40.94, -35.57) * mm});
            skLineSegment(sketch, "E17.21.0.35", {"start": v(44.57, 0.43) * mm, "end": v(40.94, 0.43) * mm});
            skLineSegment(sketch, "E17.21.0.36", {"start": v(44.57, 13.93) * mm, "end": v(44.57, 17.56) * mm});
            skLineSegment(sketch, "E17.21.0.37", {"start": v(44.57, -22.07) * mm, "end": v(44.57, -18.44) * mm});
            skLineSegment(sketch, "E17.21.0.38", {"start": v(44.57, -17.57) * mm, "end": v(44.57, -13.94) * mm});
            skLineSegment(sketch, "E17.21.0.39", {"start": v(40.94, 4.93) * mm, "end": v(40.94, 8.56) * mm});
            skLineSegment(sketch, "E17.21.0.40", {"start": v(44.57, 26.56) * mm, "end": v(40.94, 26.56) * mm});
            skLineSegment(sketch, "E17.21.0.41", {"start": v(44.57, 9.43) * mm, "end": v(40.94, 9.43) * mm});
            skLineSegment(sketch, "E17.21.0.42", {"start": v(40.94, 22.93) * mm, "end": v(40.94, 26.56) * mm});
            skLineSegment(sketch, "E17.21.0.43", {"start": v(44.57, -13.94) * mm, "end": v(40.94, -13.94) * mm});
            skLineSegment(sketch, "E17.21.0.44", {"start": v(44.57, -31.94) * mm, "end": v(40.94, -31.94) * mm});
            skLineSegment(sketch, "E17.21.0.45", {"start": v(44.57, 22.06) * mm, "end": v(40.94, 22.06) * mm});
            skLineSegment(sketch, "E17.21.0.46", {"start": v(44.57, 4.06) * mm, "end": v(40.94, 4.06) * mm});
            skLineSegment(sketch, "E17.21.0.47", {"start": v(40.94, 0.43) * mm, "end": v(40.94, 4.06) * mm});
            skLineSegment(sketch, "E17.21.0.48", {"start": v(40.94, -35.57) * mm, "end": v(40.94, -31.94) * mm});
            skLineSegment(sketch, "E17.21.0.49", {"start": v(44.57, 0.43) * mm, "end": v(44.57, 4.06) * mm});
            skLineSegment(sketch, "E17.21.0.50", {"start": v(44.57, -26.57) * mm, "end": v(40.94, -26.57) * mm});
            skLineSegment(sketch, "E17.21.0.51", {"start": v(44.57, -35.57) * mm, "end": v(44.57, -31.94) * mm});
            skLineSegment(sketch, "E17.21.0.52", {"start": v(44.57, -4.07) * mm, "end": v(44.57, -0.44) * mm});
            skLineSegment(sketch, "E17.21.0.53", {"start": v(44.57, -22.07) * mm, "end": v(40.94, -22.07) * mm});
            skLineSegment(sketch, "E17.21.0.54", {"start": v(44.57, 18.43) * mm, "end": v(44.57, 22.06) * mm});
            skLineSegment(sketch, "E17.21.0.55", {"start": v(44.57, -18.44) * mm, "end": v(40.94, -18.44) * mm});
            skLineSegment(sketch, "E17.21.0.56", {"start": v(44.57, -8.57) * mm, "end": v(44.57, -4.94) * mm});
            skLineSegment(sketch, "E17.21.0.57", {"start": v(44.57, 18.43) * mm, "end": v(40.94, 18.43) * mm});
            skLineSegment(sketch, "E17.21.0.58", {"start": v(44.57, 35.56) * mm, "end": v(40.94, 35.56) * mm});
            skLineSegment(sketch, "E17.21.0.59", {"start": v(44.57, 4.93) * mm, "end": v(44.57, 8.56) * mm});
            skLineSegment(sketch, "E17.21.0.60", {"start": v(44.57, 27.43) * mm, "end": v(40.94, 27.43) * mm});
            skLineSegment(sketch, "E17.21.0.61", {"start": v(44.57, -8.57) * mm, "end": v(40.94, -8.57) * mm});
            skLineSegment(sketch, "E17.21.0.62", {"start": v(44.57, 8.56) * mm, "end": v(40.94, 8.56) * mm});
            skLineSegment(sketch, "E17.21.0.63", {"start": v(40.94, -17.57) * mm, "end": v(40.94, -13.94) * mm});
            skLineSegment(sketch, "E17.21.0.64", {"start": v(44.57, 22.93) * mm, "end": v(40.94, 22.93) * mm});
            skLineSegment(sketch, "E17.21.0.65", {"start": v(44.57, 22.93) * mm, "end": v(44.57, 26.56) * mm});
            skLineSegment(sketch, "E17.22.0.0", {"start": v(45.44, 27.43) * mm, "end": v(45.44, 31.06) * mm});
            skLineSegment(sketch, "E17.22.0.1", {"start": v(49.07, 27.43) * mm, "end": v(49.07, 31.06) * mm});
            skLineSegment(sketch, "E17.22.0.2", {"start": v(49.07, -13.07) * mm, "end": v(49.07, -9.44) * mm});
            skLineSegment(sketch, "E17.22.0.3", {"start": v(45.44, 9.43) * mm, "end": v(45.44, 13.06) * mm});
            skLineSegment(sketch, "E17.22.0.4", {"start": v(45.44, -13.07) * mm, "end": v(45.44, -9.44) * mm});
            skLineSegment(sketch, "E17.22.0.5", {"start": v(45.44, -31.07) * mm, "end": v(45.44, -27.44) * mm});
            skPoint(sketch, "E17.22.0.6", {"position": v(47.25, 33.75) * mm});
            skLineSegment(sketch, "E17.22.0.7", {"start": v(49.07, 9.43) * mm, "end": v(49.07, 13.06) * mm});
            skLineSegment(sketch, "E17.22.0.8", {"start": v(49.07, -31.07) * mm, "end": v(49.07, -27.44) * mm});
            skLineSegment(sketch, "E17.22.0.9", {"start": v(49.07, 31.93) * mm, "end": v(49.07, 27.43) * mm, "construction": true});
            skLineSegment(sketch, "E17.22.0.10", {"start": v(49.07, 31.06) * mm, "end": v(45.44, 31.06) * mm});
            skLineSegment(sketch, "E17.22.0.11", {"start": v(49.07, 4.93) * mm, "end": v(45.44, 4.93) * mm});
            skLineSegment(sketch, "E17.22.0.12", {"start": v(49.07, -13.07) * mm, "end": v(45.44, -13.07) * mm});
            skLineSegment(sketch, "E17.22.0.13", {"start": v(49.07, -31.07) * mm, "end": v(45.44, -31.07) * mm});
            skLineSegment(sketch, "E17.22.0.14", {"start": v(45.44, 31.93) * mm, "end": v(45.44, 35.56) * mm});
            skLineSegment(sketch, "E17.22.0.15", {"start": v(49.07, 31.93) * mm, "end": v(49.07, 35.56) * mm});
            skLineSegment(sketch, "E17.22.0.16", {"start": v(49.07, 31.93) * mm, "end": v(45.44, 31.93) * mm});
            skLineSegment(sketch, "E17.22.0.17", {"start": v(45.44, 18.43) * mm, "end": v(45.44, 22.06) * mm});
            skLineSegment(sketch, "E17.22.0.18", {"start": v(49.07, 13.06) * mm, "end": v(45.44, 13.06) * mm});
            skLineSegment(sketch, "E17.22.0.19", {"start": v(49.07, -4.94) * mm, "end": v(45.44, -4.94) * mm});
            skLineSegment(sketch, "E17.22.0.20", {"start": v(49.07, -22.94) * mm, "end": v(45.44, -22.94) * mm});
            skLineSegment(sketch, "E17.22.0.21", {"start": v(49.07, -26.57) * mm, "end": v(49.07, -22.94) * mm});
            skLineSegment(sketch, "E17.22.0.22", {"start": v(45.44, -8.57) * mm, "end": v(45.44, -4.94) * mm});
            skLineSegment(sketch, "E17.22.0.23", {"start": v(45.44, -26.57) * mm, "end": v(45.44, -22.94) * mm});
            skLineSegment(sketch, "E17.22.0.24", {"start": v(49.07, 17.56) * mm, "end": v(45.44, 17.56) * mm});
            skLineSegment(sketch, "E17.22.0.25", {"start": v(49.07, -0.44) * mm, "end": v(45.44, -0.44) * mm});
            skLineSegment(sketch, "E17.22.0.26", {"start": v(49.07, -9.44) * mm, "end": v(45.44, -9.44) * mm});
            skLineSegment(sketch, "E17.22.0.27", {"start": v(45.44, -22.07) * mm, "end": v(45.44, -18.44) * mm});
            skLineSegment(sketch, "E17.22.0.28", {"start": v(45.44, 13.93) * mm, "end": v(45.44, 17.56) * mm});
            skLineSegment(sketch, "E17.22.0.29", {"start": v(45.44, -4.07) * mm, "end": v(45.44, -0.44) * mm});
            skLineSegment(sketch, "E17.22.0.30", {"start": v(49.07, 13.93) * mm, "end": v(45.44, 13.93) * mm});
            skLineSegment(sketch, "E17.22.0.31", {"start": v(49.07, -4.07) * mm, "end": v(45.44, -4.07) * mm});
            skLineSegment(sketch, "E17.22.0.32", {"start": v(49.07, -17.57) * mm, "end": v(45.44, -17.57) * mm});
            skLineSegment(sketch, "E17.22.0.33", {"start": v(49.07, -27.44) * mm, "end": v(45.44, -27.44) * mm});
            skLineSegment(sketch, "E17.22.0.34", {"start": v(49.07, -35.57) * mm, "end": v(45.44, -35.57) * mm});
            skLineSegment(sketch, "E17.22.0.35", {"start": v(49.07, 0.43) * mm, "end": v(45.44, 0.43) * mm});
            skLineSegment(sketch, "E17.22.0.36", {"start": v(49.07, 13.93) * mm, "end": v(49.07, 17.56) * mm});
            skLineSegment(sketch, "E17.22.0.37", {"start": v(49.07, -22.07) * mm, "end": v(49.07, -18.44) * mm});
            skLineSegment(sketch, "E17.22.0.38", {"start": v(49.07, -17.57) * mm, "end": v(49.07, -13.94) * mm});
            skLineSegment(sketch, "E17.22.0.39", {"start": v(45.44, 4.93) * mm, "end": v(45.44, 8.56) * mm});
            skLineSegment(sketch, "E17.22.0.40", {"start": v(49.07, 26.56) * mm, "end": v(45.44, 26.56) * mm});
            skLineSegment(sketch, "E17.22.0.41", {"start": v(49.07, 9.43) * mm, "end": v(45.44, 9.43) * mm});
            skLineSegment(sketch, "E17.22.0.42", {"start": v(45.44, 22.93) * mm, "end": v(45.44, 26.56) * mm});
            skLineSegment(sketch, "E17.22.0.43", {"start": v(49.07, -13.94) * mm, "end": v(45.44, -13.94) * mm});
            skLineSegment(sketch, "E17.22.0.44", {"start": v(49.07, -31.94) * mm, "end": v(45.44, -31.94) * mm});
            skLineSegment(sketch, "E17.22.0.45", {"start": v(49.07, 22.06) * mm, "end": v(45.44, 22.06) * mm});
            skLineSegment(sketch, "E17.22.0.46", {"start": v(49.07, 4.06) * mm, "end": v(45.44, 4.06) * mm});
            skLineSegment(sketch, "E17.22.0.47", {"start": v(45.44, 0.43) * mm, "end": v(45.44, 4.06) * mm});
            skLineSegment(sketch, "E17.22.0.48", {"start": v(45.44, -35.57) * mm, "end": v(45.44, -31.94) * mm});
            skLineSegment(sketch, "E17.22.0.49", {"start": v(49.07, 0.43) * mm, "end": v(49.07, 4.06) * mm});
            skLineSegment(sketch, "E17.22.0.50", {"start": v(49.07, -26.57) * mm, "end": v(45.44, -26.57) * mm});
            skLineSegment(sketch, "E17.22.0.51", {"start": v(49.07, -35.57) * mm, "end": v(49.07, -31.94) * mm});
            skLineSegment(sketch, "E17.22.0.52", {"start": v(49.07, -4.07) * mm, "end": v(49.07, -0.44) * mm});
            skLineSegment(sketch, "E17.22.0.53", {"start": v(49.07, -22.07) * mm, "end": v(45.44, -22.07) * mm});
            skLineSegment(sketch, "E17.22.0.54", {"start": v(49.07, 18.43) * mm, "end": v(49.07, 22.06) * mm});
            skLineSegment(sketch, "E17.22.0.55", {"start": v(49.07, -18.44) * mm, "end": v(45.44, -18.44) * mm});
            skLineSegment(sketch, "E17.22.0.56", {"start": v(49.07, -8.57) * mm, "end": v(49.07, -4.94) * mm});
            skLineSegment(sketch, "E17.22.0.57", {"start": v(49.07, 18.43) * mm, "end": v(45.44, 18.43) * mm});
            skLineSegment(sketch, "E17.22.0.58", {"start": v(49.07, 35.56) * mm, "end": v(45.44, 35.56) * mm});
            skLineSegment(sketch, "E17.22.0.59", {"start": v(49.07, 4.93) * mm, "end": v(49.07, 8.56) * mm});
            skLineSegment(sketch, "E17.22.0.60", {"start": v(49.07, 27.43) * mm, "end": v(45.44, 27.43) * mm});
            skLineSegment(sketch, "E17.22.0.61", {"start": v(49.07, -8.57) * mm, "end": v(45.44, -8.57) * mm});
            skLineSegment(sketch, "E17.22.0.62", {"start": v(49.07, 8.56) * mm, "end": v(45.44, 8.56) * mm});
            skLineSegment(sketch, "E17.22.0.63", {"start": v(45.44, -17.57) * mm, "end": v(45.44, -13.94) * mm});
            skLineSegment(sketch, "E17.22.0.64", {"start": v(49.07, 22.93) * mm, "end": v(45.44, 22.93) * mm});
            skLineSegment(sketch, "E17.22.0.65", {"start": v(49.07, 22.93) * mm, "end": v(49.07, 26.56) * mm});
            skLineSegment(sketch, "E17.23.0.0", {"start": v(49.94, 27.43) * mm, "end": v(49.94, 31.06) * mm});
            skLineSegment(sketch, "E17.23.0.1", {"start": v(53.57, 27.43) * mm, "end": v(53.57, 31.06) * mm});
            skLineSegment(sketch, "E17.23.0.2", {"start": v(53.57, -13.07) * mm, "end": v(53.57, -9.44) * mm});
            skLineSegment(sketch, "E17.23.0.3", {"start": v(49.94, 9.43) * mm, "end": v(49.94, 13.06) * mm});
            skLineSegment(sketch, "E17.23.0.4", {"start": v(49.94, -13.07) * mm, "end": v(49.94, -9.44) * mm});
            skLineSegment(sketch, "E17.23.0.5", {"start": v(49.94, -31.07) * mm, "end": v(49.94, -27.44) * mm});
            skPoint(sketch, "E17.23.0.6", {"position": v(51.75, 33.75) * mm});
            skLineSegment(sketch, "E17.23.0.7", {"start": v(53.57, 9.43) * mm, "end": v(53.57, 13.06) * mm});
            skLineSegment(sketch, "E17.23.0.8", {"start": v(53.57, -31.07) * mm, "end": v(53.57, -27.44) * mm});
            skLineSegment(sketch, "E17.23.0.9", {"start": v(53.57, 31.93) * mm, "end": v(53.57, 27.43) * mm, "construction": true});
            skLineSegment(sketch, "E17.23.0.10", {"start": v(53.57, 31.06) * mm, "end": v(49.94, 31.06) * mm});
            skLineSegment(sketch, "E17.23.0.11", {"start": v(53.57, 4.93) * mm, "end": v(49.94, 4.93) * mm});
            skLineSegment(sketch, "E17.23.0.12", {"start": v(53.57, -13.07) * mm, "end": v(49.94, -13.07) * mm});
            skLineSegment(sketch, "E17.23.0.13", {"start": v(53.57, -31.07) * mm, "end": v(49.94, -31.07) * mm});
            skLineSegment(sketch, "E17.23.0.14", {"start": v(49.94, 31.93) * mm, "end": v(49.94, 35.56) * mm});
            skLineSegment(sketch, "E17.23.0.15", {"start": v(53.57, 31.93) * mm, "end": v(53.57, 35.56) * mm});
            skLineSegment(sketch, "E17.23.0.16", {"start": v(53.57, 31.93) * mm, "end": v(49.94, 31.93) * mm});
            skLineSegment(sketch, "E17.23.0.17", {"start": v(49.94, 18.43) * mm, "end": v(49.94, 22.06) * mm});
            skLineSegment(sketch, "E17.23.0.18", {"start": v(53.57, 13.06) * mm, "end": v(49.94, 13.06) * mm});
            skLineSegment(sketch, "E17.23.0.19", {"start": v(53.57, -4.94) * mm, "end": v(49.94, -4.94) * mm});
            skLineSegment(sketch, "E17.23.0.20", {"start": v(53.57, -22.94) * mm, "end": v(49.94, -22.94) * mm});
            skLineSegment(sketch, "E17.23.0.21", {"start": v(53.57, -26.57) * mm, "end": v(53.57, -22.94) * mm});
            skLineSegment(sketch, "E17.23.0.22", {"start": v(49.94, -8.57) * mm, "end": v(49.94, -4.94) * mm});
            skLineSegment(sketch, "E17.23.0.23", {"start": v(49.94, -26.57) * mm, "end": v(49.94, -22.94) * mm});
            skLineSegment(sketch, "E17.23.0.24", {"start": v(53.57, 17.56) * mm, "end": v(49.94, 17.56) * mm});
            skLineSegment(sketch, "E17.23.0.25", {"start": v(53.57, -0.44) * mm, "end": v(49.94, -0.44) * mm});
            skLineSegment(sketch, "E17.23.0.26", {"start": v(53.57, -9.44) * mm, "end": v(49.94, -9.44) * mm});
            skLineSegment(sketch, "E17.23.0.27", {"start": v(49.94, -22.07) * mm, "end": v(49.94, -18.44) * mm});
            skLineSegment(sketch, "E17.23.0.28", {"start": v(49.94, 13.93) * mm, "end": v(49.94, 17.56) * mm});
            skLineSegment(sketch, "E17.23.0.29", {"start": v(49.94, -4.07) * mm, "end": v(49.94, -0.44) * mm});
            skLineSegment(sketch, "E17.23.0.30", {"start": v(53.57, 13.93) * mm, "end": v(49.94, 13.93) * mm});
            skLineSegment(sketch, "E17.23.0.31", {"start": v(53.57, -4.07) * mm, "end": v(49.94, -4.07) * mm});
            skLineSegment(sketch, "E17.23.0.32", {"start": v(53.57, -17.57) * mm, "end": v(49.94, -17.57) * mm});
            skLineSegment(sketch, "E17.23.0.33", {"start": v(53.57, -27.44) * mm, "end": v(49.94, -27.44) * mm});
            skLineSegment(sketch, "E17.23.0.34", {"start": v(53.57, -35.57) * mm, "end": v(49.94, -35.57) * mm});
            skLineSegment(sketch, "E17.23.0.35", {"start": v(53.57, 0.43) * mm, "end": v(49.94, 0.43) * mm});
            skLineSegment(sketch, "E17.23.0.36", {"start": v(53.57, 13.93) * mm, "end": v(53.57, 17.56) * mm});
            skLineSegment(sketch, "E17.23.0.37", {"start": v(53.57, -22.07) * mm, "end": v(53.57, -18.44) * mm});
            skLineSegment(sketch, "E17.23.0.38", {"start": v(53.57, -17.57) * mm, "end": v(53.57, -13.94) * mm});
            skLineSegment(sketch, "E17.23.0.39", {"start": v(49.94, 4.93) * mm, "end": v(49.94, 8.56) * mm});
            skLineSegment(sketch, "E17.23.0.40", {"start": v(53.57, 26.56) * mm, "end": v(49.94, 26.56) * mm});
            skLineSegment(sketch, "E17.23.0.41", {"start": v(53.57, 9.43) * mm, "end": v(49.94, 9.43) * mm});
            skLineSegment(sketch, "E17.23.0.42", {"start": v(49.94, 22.93) * mm, "end": v(49.94, 26.56) * mm});
            skLineSegment(sketch, "E17.23.0.43", {"start": v(53.57, -13.94) * mm, "end": v(49.94, -13.94) * mm});
            skLineSegment(sketch, "E17.23.0.44", {"start": v(53.57, -31.94) * mm, "end": v(49.94, -31.94) * mm});
            skLineSegment(sketch, "E17.23.0.45", {"start": v(53.57, 22.06) * mm, "end": v(49.94, 22.06) * mm});
            skLineSegment(sketch, "E17.23.0.46", {"start": v(53.57, 4.06) * mm, "end": v(49.94, 4.06) * mm});
            skLineSegment(sketch, "E17.23.0.47", {"start": v(49.94, 0.43) * mm, "end": v(49.94, 4.06) * mm});
            skLineSegment(sketch, "E17.23.0.48", {"start": v(49.94, -35.57) * mm, "end": v(49.94, -31.94) * mm});
            skLineSegment(sketch, "E17.23.0.49", {"start": v(53.57, 0.43) * mm, "end": v(53.57, 4.06) * mm});
            skLineSegment(sketch, "E17.23.0.50", {"start": v(53.57, -26.57) * mm, "end": v(49.94, -26.57) * mm});
            skLineSegment(sketch, "E17.23.0.51", {"start": v(53.57, -35.57) * mm, "end": v(53.57, -31.94) * mm});
            skLineSegment(sketch, "E17.23.0.52", {"start": v(53.57, -4.07) * mm, "end": v(53.57, -0.44) * mm});
            skLineSegment(sketch, "E17.23.0.53", {"start": v(53.57, -22.07) * mm, "end": v(49.94, -22.07) * mm});
            skLineSegment(sketch, "E17.23.0.54", {"start": v(53.57, 18.43) * mm, "end": v(53.57, 22.06) * mm});
            skLineSegment(sketch, "E17.23.0.55", {"start": v(53.57, -18.44) * mm, "end": v(49.94, -18.44) * mm});
            skLineSegment(sketch, "E17.23.0.56", {"start": v(53.57, -8.57) * mm, "end": v(53.57, -4.94) * mm});
            skLineSegment(sketch, "E17.23.0.57", {"start": v(53.57, 18.43) * mm, "end": v(49.94, 18.43) * mm});
            skLineSegment(sketch, "E17.23.0.58", {"start": v(53.57, 35.56) * mm, "end": v(49.94, 35.56) * mm});
            skLineSegment(sketch, "E17.23.0.59", {"start": v(53.57, 4.93) * mm, "end": v(53.57, 8.56) * mm});
            skLineSegment(sketch, "E17.23.0.60", {"start": v(53.57, 27.43) * mm, "end": v(49.94, 27.43) * mm});
            skLineSegment(sketch, "E17.23.0.61", {"start": v(53.57, -8.57) * mm, "end": v(49.94, -8.57) * mm});
            skLineSegment(sketch, "E17.23.0.62", {"start": v(53.57, 8.56) * mm, "end": v(49.94, 8.56) * mm});
            skLineSegment(sketch, "E17.23.0.63", {"start": v(49.94, -17.57) * mm, "end": v(49.94, -13.94) * mm});
            skLineSegment(sketch, "E17.23.0.64", {"start": v(53.57, 22.93) * mm, "end": v(49.94, 22.93) * mm});
            skLineSegment(sketch, "E17.23.0.65", {"start": v(53.57, 22.93) * mm, "end": v(53.57, 26.56) * mm});
            skLineSegment(sketch, "E17.direction1", {"start": v(-53.57, 27.43) * mm, "end": v(-49.07, 27.43) * mm, "construction": true});
            skSolve(sketch);
        }
        {
            var Q0;
            Q0=qSketchRegion(id+"F4",true);
            extrude(context, id + "F5", {"entities" : qUnion([Q0]), "operationType" : NewBodyOperationType.REMOVE, "oppositeDirection" : true, "depth" : 12.54 * mm});
        }
    });
